FCSTD DOCUMENT  (FreeCAD 1.0R39319 (Git))
Label: MainAssembly
License: All rights reserved
LicenseURL: https://en.wikipedia.org/wiki/All_rights_reserved
objects: App::Link×59, App::FeaturePython×30, Assembly::AssemblyLink×1, App::DocumentObjectGroup×1, Assembly::JointGroup×1, Assembly::AssemblyObject×1
EXTERNAL_REF file=../Parts/Chassis.FCStd obj=Part
EXTERNAL_REF file=../Parts/MotorPlate.FCStd obj=Part
EXTERNAL_REF file=../Parts/MotorHolder.FCStd obj=Part
EXTERNAL_REF file=../Parts/N20Motor.FCStd obj=Part
EXTERNAL_REF file=../Parts/MotorGear.FCStd obj=Part
EXTERNAL_REF file=../Parts/AxleHolder.FCStd obj=Part
EXTERNAL_REF file=../Parts/LegoDifferentialGear.FCStd obj=Part
EXTERNAL_REF file=../Parts/LegoBevelGear.FCStd obj=Part
EXTERNAL_REF file=../Parts/BackWheelAxle.FCStd obj=Part
EXTERNAL_REF file=../Parts/BackWheelStopper.FCStd obj=Part
EXTERNAL_REF file=../Parts/BackWheelConnector.FCStd obj=Part
EXTERNAL_REF file=../Parts/Wheel.FCStd obj=Part
EXTERNAL_REF file=FrontAssembly.FCStd obj=Assembly
EXTERNAL_REF file=FrontAssembly.FCStd obj=FrontCoverPart
EXTERNAL_REF file=FrontAssembly.FCStd obj=WheelLinkageTopLeftBody
EXTERNAL_REF file=FrontAssembly.FCStd obj=WheelLinkageBottomLeftPart
EXTERNAL_REF file=FrontAssembly.FCStd obj=WheelLinkageTopRightPart
EXTERNAL_REF file=FrontAssembly.FCStd obj=WheelLinkageBottomRightPart
EXTERNAL_REF file=FrontAssembly.FCStd obj=FrontWheelAxleLeftPart
EXTERNAL_REF file=FrontAssembly.FCStd obj=FrontWheelAxleRightPart
EXTERNAL_REF file=FrontAssembly.FCStd obj=S0004mPart
EXTERNAL_REF file=FrontAssembly.FCStd obj=TBoneLinkageTopPart
EXTERNAL_REF file=FrontAssembly.FCStd obj=TBoneLinkageBottomPart
EXTERNAL_REF file=FrontAssembly.FCStd obj=TransferLinkageLeftPart
EXTERNAL_REF file=FrontAssembly.FCStd obj=TransferLinkageRightPart
EXTERNAL_REF file=FrontAssembly.FCStd obj=FrontWheelStopperPart
EXTERNAL_REF file=FrontAssembly.FCStd obj=FrontWheelStopperPart001
EXTERNAL_REF file=FrontAssembly.FCStd obj=WheelPart
EXTERNAL_REF file=FrontAssembly.FCStd obj=WheelPart001
EXTERNAL_REF file=FrontAssembly.FCStd obj=RpiCameraPart
EXTERNAL_REF file=../Parts/LidarPlate.FCStd obj=Part
EXTERNAL_REF file=../Parts/Chassis.FCStd obj=Body
EXTERNAL_REF file=../Parts/MotorPlate.FCStd obj=Body
EXTERNAL_REF file=../Parts/MotorHolder.FCStd obj=Body
EXTERNAL_REF file=../Parts/MotorGear.FCStd obj=Body
EXTERNAL_REF file=../Parts/AxleHolder.FCStd obj=Body
EXTERNAL_REF file=../Parts/BackWheelAxle.FCStd obj=Body
EXTERNAL_REF file=../Parts/BackWheelStopper.FCStd obj=Body
EXTERNAL_REF file=../Parts/BackWheelConnector.FCStd obj=Body
EXTERNAL_REF file=../Parts/LidarPlate.FCStd obj=Body
EXTERNAL_REF file=../Parts/FrontCover.FCStd obj=Body
EXTERNAL_REF file=../Parts/WheelLinkage/WheelLinkageBottomLeft.FCStd obj=Body
EXTERNAL_REF file=../Parts/WheelLinkage/WheelLinkageTopRight.FCStd obj=Part__Mirroring
EXTERNAL_REF file=../Parts/WheelLinkage/WheelLinkageBottomRight.FCStd obj=Part__Mirroring
EXTERNAL_REF file=../Parts/FrontWheelAxle/FrontWheelAxleLeft.FCStd obj=Body
EXTERNAL_REF file=../Parts/FrontWheelAxle/FrontWheelAxleRight.FCStd obj=Part__Mirroring
EXTERNAL_REF file=../Parts/TBoneLinkage/TBoneLinkageTop.FCStd obj=Body
EXTERNAL_REF file=../Parts/TBoneLinkage/TBoneLinkageBottom.FCStd obj=Body
EXTERNAL_REF file=../Parts/TransferLinkage/TransferLinkageLeft.FCStd obj=Body
EXTERNAL_REF file=../Parts/TransferLinkage/TransferLinkageRight.FCStd obj=Part__Mirroring
EXTERNAL_REF file=../Parts/FrontWheelStopper.FCStd obj=Body

FEATURE [App::Link] ChassisPart
  LinkedObject = -> <external ../Parts/Chassis.FCStd>#Part
FEATURE [App::FeaturePython] GroundedJoint  # Assembly grounded joint (typed FeaturePython)
  ObjectToGround = -> ChassisPart
FEATURE [App::Link] MotorPlatePart
  LinkPlacement = pos=(-5e-16,-200,64) rot=(0,0,1;0rad)
  LinkedObject = -> <external ../Parts/MotorPlate.FCStd>#Part
  Placement = pos=(-5e-16,-200,64) rot=(0,0,1;0rad)
FEATURE [App::Link] MotorHolderPart
  LinkPlacement = pos=(5,-200,64) rot=(0,0,1;0rad)
  LinkedObject = -> <external ../Parts/MotorHolder.FCStd>#Part
  Placement = pos=(5,-200,64) rot=(0,0,1;0rad)
FEATURE [App::Link] N20MotorPart
  LinkPlacement = pos=(3,-194,44) rot=(0,0,1;0rad)
  LinkedObject = -> <external ../Parts/N20Motor.FCStd>#Part
  Placement = pos=(3,-194,44) rot=(0,0,1;0rad)
FEATURE [App::Link] MotorGearPart
  LinkPlacement = pos=(-12.15,-194.077,44) rot=(0.57735,0.57735,0.57735;2.0944rad)
  LinkedObject = -> <external ../Parts/MotorGear.FCStd>#Part
  Placement = pos=(-12.15,-194.077,44) rot=(0.57735,0.57735,0.57735;2.0944rad)
FEATURE [App::FeaturePython] Joint  label="Fixed"  # Assembly joint (typed FeaturePython)
  Activated = true
  AngleMax = 0
  AngleMin = 0
  Detach1 = false
  Detach2 = false
  Distance = 0
  Distance2 = 0
  EnableAngleMax = false
  EnableAngleMin = false
  EnableLengthMax = false
  EnableLengthMin = false
  JointType = 0 (Fixed)
  LengthMax = 0
  LengthMin = 0
  Placement1 = pos=(19.5,-19,-5) rot=(0,0,1;0rad)
  Placement2 = pos=(19.5,-219,59) rot=(0,0,1;0rad)
  Reference1 = -> Assembly [MotorPlatePart.Body.Edge35,MotorPlatePart.Body.Edge35]
  Reference2 = -> Assembly [ChassisPart.Body.Edge276,ChassisPart.Body.Edge276]
FEATURE [App::FeaturePython] Joint001  label="Fixed001"  # Assembly joint (typed FeaturePython)
  Activated = true
  AngleMax = 0
  AngleMin = 0
  Detach1 = false
  Detach2 = false
  Distance = 0
  Distance2 = 0
  EnableAngleMax = false
  EnableAngleMin = false
  EnableLengthMax = false
  EnableLengthMin = false
  JointType = 0 (Fixed)
  LengthMax = 0
  LengthMin = 0
  Offset2 = pos=(0,0,0) rot=(0,0,1;1.5708rad)
  Placement1 = pos=(5,-6,-15) rot=(0,0,-1;1.5708rad)
  Placement2 = pos=(10,-6,-15) rot=(0.707107,-0.707107,0;3.14159rad)
  Reference1 = -> Assembly [MotorHolderPart.Body.Edge5,MotorHolderPart.Body.Edge5]
  Reference2 = -> Assembly [MotorPlatePart.Body.Edge43,MotorPlatePart.Body.Edge43]
FEATURE [App::FeaturePython] Joint002  label="Distance"  # Assembly joint (typed FeaturePython)
  Activated = true
  AngleMax = 0
  AngleMin = 0
  Detach1 = false
  Detach2 = false
  Distance = 0
  Distance2 = 0
  EnableAngleMax = false
  EnableAngleMin = false
  EnableLengthMax = false
  EnableLengthMin = false
  JointType = 5 (Distance)
  LengthMax = 0
  LengthMin = 0
  Placement1 = pos=(-7.38622,1.78864e-06,5) rot=(0,0,-1;3.14159rad)
  Placement2 = pos=(10,6,-15) rot=(0,0,1;0rad)
  Reference1 = -> Assembly [N20MotorPart.Compound.Face176,N20MotorPart.Compound.Vertex330]
  Reference2 = -> Assembly [MotorPlatePart.Body.Face8,MotorPlatePart.Body.Face8]
FEATURE [App::FeaturePython] Joint003  label="Distance001"  # Assembly joint (typed FeaturePython)
  Activated = true
  AngleMax = 0
  AngleMin = 0
  Detach1 = false
  Detach2 = false
  Distance = 0
  Distance2 = 0
  EnableAngleMax = false
  EnableAngleMin = false
  EnableLengthMax = false
  EnableLengthMin = false
  JointType = 5 (Distance)
  LengthMax = 0
  LengthMin = 0
  Placement1 = pos=(5,12,-20) rot=(0.57735,-0.57735,0.57735;2.0944rad)
  Placement2 = pos=(-7.4,2.6e-15,-1.9e-15) rot=(0.57735,-0.57735,-0.57735;2.0944rad)
  Reference1 = -> Assembly [MotorHolderPart.Body.Face9,MotorHolderPart.Body.Face9]
  Reference2 = -> Assembly [N20MotorPart.Compound.Face175,N20MotorPart.Compound.Face175]
FEATURE [App::FeaturePython] Joint004  label="Fixed002"  # Assembly joint (typed FeaturePython)
  Activated = true
  AngleMax = 0
  AngleMin = 0
  Detach1 = false
  Detach2 = false
  Distance = 0
  Distance2 = 0
  EnableAngleMax = false
  EnableAngleMin = false
  EnableLengthMax = false
  EnableLengthMin = false
  JointType = 0 (Fixed)
  LengthMax = 0
  LengthMin = 0
  Offset2 = pos=(0,0,-7.7) rot=(0,0,1;0rad)
  Placement1 = pos=(0,0,3.85) rot=(1,0,0;3.14159rad)
  Placement2 = pos=(11.3,0.0768482,2.70398e-05) rot=(-0.57735,0.57735,-0.57735;2.0944rad)
  Reference1 = -> Assembly [MotorGearPart.Body.Edge5,MotorGearPart.Body.Edge5]
  Reference2 = -> Assembly [N20MotorPart.Compound.Face1277,N20MotorPart.Compound.Face1277]
FEATURE [App::Link] AxleHolderPart
  LinkPlacement = pos=(-23,-194,44) rot=(0.57735,0.57735,0.57735;2.0944rad)
  LinkedObject = -> <external ../Parts/AxleHolder.FCStd>#Part
  Placement = pos=(-23,-194,44) rot=(0.57735,0.57735,0.57735;2.0944rad)
FEATURE [App::Link] AxleHolderPart001
  LinkPlacement = pos=(-23,-194,20) rot=(0.57735,0.57735,0.57735;2.0944rad)
  LinkedObject = -> <external ../Parts/AxleHolder.FCStd>#Part
  Placement = pos=(-23,-194,20) rot=(0.57735,0.57735,0.57735;2.0944rad)
FEATURE [App::Link] AxleHolderPart002
  LinkPlacement = pos=(23,-194,20) rot=(-0.57735,0.57735,0.57735;4.18879rad)
  LinkedObject = -> <external ../Parts/AxleHolder.FCStd>#Part
  Placement = pos=(23,-194,20) rot=(-0.57735,0.57735,0.57735;4.18879rad)
FEATURE [App::FeaturePython] Joint006  label="Distance003"  # Assembly joint (typed FeaturePython)
  Activated = true
  AngleMax = 0
  AngleMin = 0
  Detach1 = false
  Detach2 = false
  Distance = 0.2
  Distance2 = 0
  EnableAngleMax = false
  EnableAngleMin = false
  EnableLengthMax = false
  EnableLengthMin = false
  JointType = 5 (Distance)
  LengthMax = 0
  LengthMin = 0
  Placement1 = pos=(-1e-16,-4.3,3.04723) rot=(-0.57735,-0.57735,0.57735;4.18879rad)
  Placement2 = pos=(-19.9444,-194,39.5) rot=(0,0,1;0rad)
  Reference1 = -> Assembly [AxleHolderPart.Body.Face9,AxleHolderPart.Body.Face9]
  Reference2 = -> Assembly [ChassisPart.Body.Face80,ChassisPart.Body.Vertex222]
FEATURE [App::FeaturePython] Joint007  label="Distance004"  # Assembly joint (typed FeaturePython)
  Activated = true
  AngleMax = 0
  AngleMin = 0
  Detach1 = false
  Detach2 = false
  Distance = -0.2
  Distance2 = 0
  EnableAngleMax = false
  EnableAngleMin = false
  EnableLengthMax = false
  EnableLengthMin = false
  JointType = 5 (Distance)
  LengthMax = 0
  LengthMin = 0
  Placement1 = pos=(-7.3,-1e-16,1.3) rot=(0.57735,-0.57735,0.57735;4.18879rad)
  Placement2 = pos=(-21.5,-201.5,44) rot=(-0.57735,0.57735,0.57735;2.0944rad)
  Reference1 = -> Assembly [AxleHolderPart.Body.Face3,AxleHolderPart.Body.Vertex8]
  Reference2 = -> Assembly [ChassisPart.Body.Face82,ChassisPart.Body.Vertex107]
FEATURE [App::FeaturePython] Joint008  label="Distance005"  # Assembly joint (typed FeaturePython)
  Activated = true
  AngleMax = 0
  AngleMin = 0
  Detach1 = false
  Detach2 = false
  Distance = 0
  Distance2 = 0
  EnableAngleMax = false
  EnableAngleMin = false
  EnableLengthMax = false
  EnableLengthMin = false
  JointType = 5 (Distance)
  LengthMax = 0
  LengthMin = 0
  Placement1 = pos=(-1e-16,0,0) rot=(0,0,1;0rad)
  Placement2 = pos=(-23,-201.464,33.8054) rot=(-0.707107,0,0.707107;3.14159rad)
  Reference1 = -> Assembly [AxleHolderPart.Body.Face2,AxleHolderPart.Body.Vertex6]
  Reference2 = -> Assembly [ChassisPart.Body.Face21,ChassisPart.Body.Vertex107]
FEATURE [App::FeaturePython] Joint009  label="Distance006"  # Assembly joint (typed FeaturePython)
  Activated = true
  AngleMax = 0
  AngleMin = 0
  Detach1 = false
  Detach2 = false
  Distance = 0.2
  Distance2 = 0
  EnableAngleMax = false
  EnableAngleMin = false
  EnableLengthMax = false
  EnableLengthMin = false
  JointType = 5 (Distance)
  LengthMax = 0
  LengthMin = 0
  Placement1 = pos=(-1e-16,-4.3,3.04723) rot=(-0.57735,-0.57735,0.57735;4.18879rad)
  Placement2 = pos=(-19.9444,-194,15.5) rot=(0,0,1;0rad)
  Reference1 = -> Assembly [AxleHolderPart001.Body.Face9,AxleHolderPart001.Body.Face9]
  Reference2 = -> Assembly [ChassisPart.Body.Face83,ChassisPart.Body.Face83]
FEATURE [App::FeaturePython] Joint010  label="Distance007"  # Assembly joint (typed FeaturePython)
  Activated = true
  AngleMax = 0
  AngleMin = 0
  Detach1 = false
  Detach2 = false
  Distance = -0.2
  Distance2 = 0
  EnableAngleMax = false
  EnableAngleMin = false
  EnableLengthMax = false
  EnableLengthMin = false
  JointType = 5 (Distance)
  LengthMax = 0
  LengthMin = 0
  Placement1 = pos=(-7.3,-1e-16,1.3) rot=(0.57735,-0.57735,0.57735;4.18879rad)
  Placement2 = pos=(-21.5,-201.5,20) rot=(0.57735,-0.57735,0.57735;2.0944rad)
  Reference1 = -> Assembly [AxleHolderPart001.Body.Face3,AxleHolderPart001.Body.Vertex6]
  Reference2 = -> Assembly [ChassisPart.Body.Face85,ChassisPart.Body.Face85]
FEATURE [App::FeaturePython] Joint011  label="Distance008"  # Assembly joint (typed FeaturePython)
  Activated = true
  AngleMax = 0
  AngleMin = 0
  Detach1 = false
  Detach2 = false
  Distance = 0
  Distance2 = 0
  EnableAngleMax = false
  EnableAngleMin = false
  EnableLengthMax = false
  EnableLengthMin = false
  JointType = 5 (Distance)
  LengthMax = 0
  LengthMin = 0
  Placement1 = pos=(-1e-16,0,0) rot=(0,0,1;0rad)
  Placement2 = pos=(-23,-201.464,33.8054) rot=(-0.707107,0,0.707107;3.14159rad)
  Reference1 = -> Assembly [AxleHolderPart001.Body.Face2,AxleHolderPart001.Body.Vertex6]
  Reference2 = -> Assembly [ChassisPart.Body.Face21,ChassisPart.Body.Vertex112]
FEATURE [App::FeaturePython] Joint012  label="Distance009"  # Assembly joint (typed FeaturePython)
  Activated = true
  AngleMax = 0
  AngleMin = 0
  Detach1 = false
  Detach2 = false
  Distance = 0.2
  Distance2 = 0
  EnableAngleMax = false
  EnableAngleMin = false
  EnableLengthMax = false
  EnableLengthMin = false
  JointType = 5 (Distance)
  LengthMax = 0
  LengthMin = 0
  Placement1 = pos=(-1e-16,-4.3,3.04723) rot=(-0.57735,-0.57735,0.57735;4.18879rad)
  Placement2 = pos=(19.9444,-194,15.5) rot=(0,0,1;0rad)
  Reference1 = -> Assembly [AxleHolderPart002.Body.Face9,AxleHolderPart002.Body.Face9]
  Reference2 = -> Assembly [ChassisPart.Body.Face99,ChassisPart.Body.Face99]
FEATURE [App::FeaturePython] Joint013  label="Distance010"  # Assembly joint (typed FeaturePython)
  Activated = true
  AngleMax = 0
  AngleMin = 0
  Detach1 = false
  Detach2 = false
  Distance = -0.2
  Distance2 = 0
  EnableAngleMax = false
  EnableAngleMin = false
  EnableLengthMax = false
  EnableLengthMin = false
  JointType = 5 (Distance)
  LengthMax = 0
  LengthMin = 0
  Placement1 = pos=(7.3,1e-16,1.3) rot=(-0.57735,-0.57735,0.57735;2.0944rad)
  Placement2 = pos=(21.5,-201.5,20) rot=(-0.57735,-0.57735,0.57735;4.18879rad)
  Reference1 = -> Assembly [AxleHolderPart002.Body.Face1,AxleHolderPart002.Body.Face1]
  Reference2 = -> Assembly [ChassisPart.Body.Face100,ChassisPart.Body.Face100]
FEATURE [App::FeaturePython] Joint014  label="Distance011"  # Assembly joint (typed FeaturePython)
  Activated = true
  AngleMax = 0
  AngleMin = 0
  Detach1 = false
  Detach2 = false
  Distance = 0
  Distance2 = 0
  EnableAngleMax = false
  EnableAngleMin = false
  EnableLengthMax = false
  EnableLengthMin = false
  JointType = 5 (Distance)
  LengthMax = 0
  LengthMin = 0
  Placement1 = pos=(-1e-16,0,0) rot=(0,0,1;0rad)
  Placement2 = pos=(23,-202.313,31.8764) rot=(0.707107,0,0.707107;3.14159rad)
  Reference1 = -> Assembly [AxleHolderPart002.Body.Face2,AxleHolderPart002.Body.Vertex7]
  Reference2 = -> Assembly [ChassisPart.Body.Face29,ChassisPart.Body.Edge197]
FEATURE [App::Link] LegoDifferentialGearPart
  LinkPlacement = pos=(3.13e-14,-194,20) rot=(0.552363,0.624332,-0.552363;4.25783rad)
  LinkedObject = -> <external ../Parts/LegoDifferentialGear.FCStd>#Part
  Placement = pos=(3.13e-14,-194,20) rot=(0.552363,0.624332,-0.552363;4.25783rad)
FEATURE [App::FeaturePython] Joint015  label="Fixed003"  # Assembly joint (typed FeaturePython)
  Activated = true
  AngleMax = 0
  AngleMin = 0
  Detach1 = false
  Detach2 = false
  Distance = 0
  Distance2 = 0
  EnableAngleMax = false
  EnableAngleMin = false
  EnableLengthMax = false
  EnableLengthMin = false
  JointType = 0 (Fixed)
  LengthMax = 0
  LengthMin = 0
  Offset2 = pos=(0,0,0) rot=(0,0,1;1.69297rad)
  Placement1 = pos=(0,-3.7e-15,16) rot=(0,0,-1;1.5708rad)
  Placement2 = pos=(0,0,7) rot=(0,0,1;1.69297rad)
  Reference1 = -> Assembly [LegoDifferentialGearPart.Solid.Edge333,LegoDifferentialGearPart.Solid.Edge333]
  Reference2 = -> Assembly [AxleHolderPart001.Body.Edge26,AxleHolderPart001.Body.Edge26]
FEATURE [App::Link] LegoBevelGearPart
  LinkPlacement = pos=(5.02e-14,-193.147,13.0522) rot=(0.599465,0.530362,0.599465;2.16631rad)
  LinkedObject = -> <external ../Parts/LegoBevelGear.FCStd>#Part
  Placement = pos=(5.02e-14,-193.147,13.0522) rot=(0.599465,0.530362,0.599465;2.16631rad)
FEATURE [App::Link] LegoBevelGearPart001
  LinkPlacement = pos=(-7.05,-194,20) rot=(0.187428,0.187428,-0.964231;1.60721rad)
  LinkedObject = -> <external ../Parts/LegoBevelGear.FCStd>#Part
  Placement = pos=(-7.05,-194,20) rot=(0.187428,0.187428,-0.964231;1.60721rad)
FEATURE [App::Link] LegoBevelGearPart002
  LinkPlacement = pos=(7.05,-194,20) rot=(0.187428,-0.187428,0.964231;1.60721rad)
  LinkedObject = -> <external ../Parts/LegoBevelGear.FCStd>#Part
  Placement = pos=(7.05,-194,20) rot=(0.187428,-0.187428,0.964231;1.60721rad)
FEATURE [App::FeaturePython] Joint016  label="Fixed004"  # Assembly joint (typed FeaturePython)
  Activated = true
  AngleMax = 0
  AngleMin = 0
  Detach1 = false
  Detach2 = false
  Distance = 0
  Distance2 = 0
  EnableAngleMax = false
  EnableAngleMin = false
  EnableLengthMax = false
  EnableLengthMin = false
  JointType = 0 (Fixed)
  LengthMax = 0
  LengthMin = 0
  Placement1 = pos=(4e-16,-1.2,0) rot=(-0.57735,-0.57735,-0.57735;2.0944rad)
  Placement2 = pos=(0,8.2,0) rot=(0.57735,0.57735,-0.57735;2.0944rad)
  Reference1 = -> Assembly [LegoBevelGearPart.Part__Feature.Edge4,LegoBevelGearPart.Part__Feature.Edge4]
  Reference2 = -> Assembly [LegoDifferentialGearPart.Solid.Edge734,LegoDifferentialGearPart.Solid.Edge734]
FEATURE [App::FeaturePython] Joint017  label="Fixed005"  # Assembly joint (typed FeaturePython)
  Activated = true
  AngleMax = 0
  AngleMin = 0
  Detach1 = false
  Detach2 = false
  Distance = 0
  Distance2 = 0
  EnableAngleMax = false
  EnableAngleMin = false
  EnableLengthMax = false
  EnableLengthMin = false
  JointType = 0 (Fixed)
  LengthMax = 0
  LengthMin = 0
  Offset2 = pos=(0,0,0) rot=(0,0,-1;0.261799rad)
  Placement1 = pos=(4e-16,-1.2,0) rot=(-0.57735,-0.57735,-0.57735;2.0944rad)
  Placement2 = pos=(0,-1.4e-15,8.25) rot=(0,0,-1;1.8326rad)
  Reference1 = -> Assembly [LegoBevelGearPart001.Part__Feature.Edge4,LegoBevelGearPart001.Part__Feature.Edge4]
  Reference2 = -> Assembly [LegoDifferentialGearPart.Solid.Edge334,LegoDifferentialGearPart.Solid.Edge334]
FEATURE [App::FeaturePython] Joint018  label="Fixed006"  # Assembly joint (typed FeaturePython)
  Activated = true
  AngleMax = 0
  AngleMin = 0
  Detach1 = false
  Detach2 = false
  Distance = 0
  Distance2 = 0
  EnableAngleMax = false
  EnableAngleMin = false
  EnableLengthMax = false
  EnableLengthMin = false
  JointType = 0 (Fixed)
  LengthMax = 0
  LengthMin = 0
  Offset1 = pos=(0,0,0) rot=(1,0,0;3.14159rad)
  Offset2 = pos=(0,0,0) rot=(0,0,-1;0.261799rad)
  Placement1 = pos=(4e-16,-1.2,0) rot=(0.57735,-0.57735,0.57735;2.0944rad)
  Placement2 = pos=(0,3.6e-15,-8.25) rot=(0,0,-1;1.8326rad)
  Reference1 = -> Assembly [LegoBevelGearPart002.Part__Feature.Edge4,LegoBevelGearPart002.Part__Feature.Edge4]
  Reference2 = -> Assembly [LegoDifferentialGearPart.Solid.Edge343,LegoDifferentialGearPart.Solid.Edge343]
FEATURE [App::Link] BackWheelAxlePart
  LinkPlacement = pos=(-3.1,-194,20) rot=(0.519988,0.677661,-0.519988;4.33274rad)
  LinkedObject = -> <external ../Parts/BackWheelAxle.FCStd>#Part
  Placement = pos=(-3.1,-194,20) rot=(0.519988,0.677661,-0.519988;4.33274rad)
FEATURE [App::Link] BackWheelAxlePart001
  LinkPlacement = pos=(3.1,-194,20) rot=(-0.519988,0.677661,-0.519988;1.95044rad)
  LinkedObject = -> <external ../Parts/BackWheelAxle.FCStd>#Part
  Placement = pos=(3.1,-194,20) rot=(-0.519988,0.677661,-0.519988;1.95044rad)
FEATURE [App::FeaturePython] Joint019  label="Fixed007"  # Assembly joint (typed FeaturePython)
  Activated = true
  AngleMax = 0
  AngleMin = 0
  Detach1 = false
  Detach2 = false
  Distance = 0
  Distance2 = 0
  EnableAngleMax = false
  EnableAngleMin = false
  EnableLengthMax = false
  EnableLengthMin = false
  JointType = 0 (Fixed)
  LengthMax = 0
  LengthMin = 0
  Offset2 = pos=(0,0,0) rot=(0,0,1;0.261799rad)
  Placement1 = pos=(0,0,19.9) rot=(0,0,1;0rad)
  Placement2 = pos=(0,0,0) rot=(0,0,1;0.261799rad)
  Reference1 = -> Assembly [BackWheelAxlePart.Body.Edge26,BackWheelAxlePart.Body.Edge26]
  Reference2 = -> Assembly [AxleHolderPart001.Body.Edge8,AxleHolderPart001.Body.Edge8]
FEATURE [App::FeaturePython] Joint020  label="Fixed008"  # Assembly joint (typed FeaturePython)
  Activated = true
  AngleMax = 0
  AngleMin = 0
  Detach1 = false
  Detach2 = false
  Distance = 0
  Distance2 = 0
  EnableAngleMax = false
  EnableAngleMin = false
  EnableLengthMax = false
  EnableLengthMin = false
  JointType = 0 (Fixed)
  LengthMax = 0
  LengthMin = 0
  Offset2 = pos=(0,0,0) rot=(0,0,-1;0.261799rad)
  Placement1 = pos=(0,0,19.9) rot=(0,0,1;0rad)
  Placement2 = pos=(0,0,0) rot=(0,0,-1;0.261799rad)
  Reference1 = -> Assembly [BackWheelAxlePart001.Body.Edge26,BackWheelAxlePart001.Body.Edge26]
  Reference2 = -> Assembly [AxleHolderPart002.Body.Edge8,AxleHolderPart002.Body.Edge8]
FEATURE [App::Link] BackWheelStopperPart
  LinkPlacement = pos=(-26.6,-194,20) rot=(0.57735,-0.57735,0.57735;4.18879rad)
  LinkedObject = -> <external ../Parts/BackWheelStopper.FCStd>#Part
  Placement = pos=(-26.6,-194,20) rot=(0.57735,-0.57735,0.57735;4.18879rad)
FEATURE [App::Link] BackWheelStopperPart001
  LinkPlacement = pos=(26.6,-194,20) rot=(0.57735,0.57735,-0.57735;4.18879rad)
  LinkedObject = -> <external ../Parts/BackWheelStopper.FCStd>#Part
  Placement = pos=(26.6,-194,20) rot=(0.57735,0.57735,-0.57735;4.18879rad)
FEATURE [App::FeaturePython] Joint021  label="Fixed009"  # Assembly joint (typed FeaturePython)
  Activated = true
  AngleMax = 0
  AngleMin = 0
  Detach1 = false
  Detach2 = false
  Distance = 0
  Distance2 = 0
  EnableAngleMax = false
  EnableAngleMin = false
  EnableLengthMax = false
  EnableLengthMin = false
  JointType = 0 (Fixed)
  LengthMax = 0
  LengthMin = 0
  Placement1 = pos=(11,0,3.6) rot=(0,0,1;0rad)
  Placement2 = pos=(-23,-205,20) rot=(-0.57735,0.57735,0.57735;4.18879rad)
  Reference1 = -> Assembly [BackWheelStopperPart.Body.Edge35,BackWheelStopperPart.Body.Edge35]
  Reference2 = -> Assembly [ChassisPart.Body.Edge133,ChassisPart.Body.Edge133]
FEATURE [App::FeaturePython] Joint022  label="Fixed010"  # Assembly joint (typed FeaturePython)
  Activated = true
  AngleMax = 0
  AngleMin = 0
  Detach1 = false
  Detach2 = false
  Distance = 0
  Distance2 = 0
  EnableAngleMax = false
  EnableAngleMin = false
  EnableLengthMax = false
  EnableLengthMin = false
  JointType = 0 (Fixed)
  LengthMax = 0
  LengthMin = 0
  Placement1 = pos=(-11,0,3.6) rot=(0,0,1;0rad)
  Placement2 = pos=(23,-205,20) rot=(0.57735,0.57735,0.57735;2.0944rad)
  Reference1 = -> Assembly [BackWheelStopperPart001.Body.Edge37,BackWheelStopperPart001.Body.Edge37]
  Reference2 = -> Assembly [ChassisPart.Body.Edge161,ChassisPart.Body.Edge161]
FEATURE [App::Link] BackWheelConnectorPart
  LinkPlacement = pos=(-43,-194,20) rot=(0.621515,-0.476905,-0.621515;2.25159rad)
  LinkedObject = -> <external ../Parts/BackWheelConnector.FCStd>#Part
  Placement = pos=(-43,-194,20) rot=(0.621515,-0.476905,-0.621515;2.25159rad)
FEATURE [App::Link] BackWheelConnectorPart001
  LinkPlacement = pos=(43,-194,20) rot=(0.621515,0.476905,0.621515;2.25159rad)
  LinkedObject = -> <external ../Parts/BackWheelConnector.FCStd>#Part
  Placement = pos=(43,-194,20) rot=(0.621515,0.476905,0.621515;2.25159rad)
FEATURE [App::FeaturePython] Joint023  label="Fixed011"  # Assembly joint (typed FeaturePython)
  Activated = true
  AngleMax = 0
  AngleMin = 0
  Detach1 = false
  Detach2 = false
  Distance = 0
  Distance2 = 0
  EnableAngleMax = false
  EnableAngleMin = false
  EnableLengthMax = false
  EnableLengthMin = false
  JointType = 0 (Fixed)
  LengthMax = 0
  LengthMin = 0
  Offset2 = pos=(0,0,0.4) rot=(0,0,1;0rad)
  Placement1 = pos=(2.5,1.9,-3.5) rot=(0,0.707107,0.707107;3.14159rad)
  Placement2 = pos=(-2.5,-1.9,36.4) rot=(1,0,0;1.5708rad)
  Reference1 = -> Assembly [BackWheelConnectorPart.Body.Edge66,BackWheelConnectorPart.Body.Edge66]
  Reference2 = -> Assembly [BackWheelAxlePart.Body.Edge9,BackWheelAxlePart.Body.Edge9]
FEATURE [App::FeaturePython] Joint024  label="Fixed012"  # Assembly joint (typed FeaturePython)
  Activated = true
  AngleMax = 0
  AngleMin = 0
  Detach1 = false
  Detach2 = false
  Distance = 0
  Distance2 = 0
  EnableAngleMax = false
  EnableAngleMin = false
  EnableLengthMax = false
  EnableLengthMin = false
  JointType = 0 (Fixed)
  LengthMax = 0
  LengthMin = 0
  Offset2 = pos=(0,0,0.4) rot=(0,0,1;0rad)
  Placement1 = pos=(-2.5,1.9,-3.5) rot=(0,0.707107,0.707107;3.14159rad)
  Placement2 = pos=(2.5,-1.9,36.4) rot=(1,0,0;1.5708rad)
  Reference1 = -> Assembly [BackWheelConnectorPart001.Body.Edge67,BackWheelConnectorPart001.Body.Edge67]
  Reference2 = -> Assembly [BackWheelAxlePart001.Body.Edge10,BackWheelAxlePart001.Body.Edge10]
FEATURE [App::Link] WheelPart
  LinkPlacement = pos=(-35,-194,20) rot=(1,0,0;0.261799rad)
  LinkedObject = -> <external ../Parts/Wheel.FCStd>#Part
  Placement = pos=(-35,-194,20) rot=(1,0,0;0.261799rad)
FEATURE [App::Link] WheelPart001
  LinkPlacement = pos=(35,-194,20) rot=(0,-0.130526,0.991445;3.14159rad)
  LinkedObject = -> <external ../Parts/Wheel.FCStd>#Part
  Placement = pos=(35,-194,20) rot=(0,-0.130526,0.991445;3.14159rad)
FEATURE [App::FeaturePython] Joint025  label="Fixed013"  # Assembly joint (typed FeaturePython)
  Activated = true
  AngleMax = 0
  AngleMin = 0
  Detach1 = false
  Detach2 = false
  Distance = 0
  Distance2 = 0
  EnableAngleMax = false
  EnableAngleMin = false
  EnableLengthMax = false
  EnableLengthMin = false
  JointType = 0 (Fixed)
  LengthMax = 0
  LengthMin = 0
  Offset2 = pos=(0,0,0) rot=(0,0,1;3.14159rad)
  Placement1 = pos=(-11,7.8e-15,-3.9e-15) rot=(0.57735,0.57735,0.57735;2.0944rad)
  Placement2 = pos=(0,0,3) rot=(0,0,1;3.14159rad)
  Reference1 = -> Assembly [WheelPart.Body.Edge25,WheelPart.Body.Edge25]
  Reference2 = -> Assembly [BackWheelConnectorPart.Body.Edge3,BackWheelConnectorPart.Body.Edge3]
FEATURE [App::FeaturePython] Joint026  label="Fixed014"  # Assembly joint (typed FeaturePython)
  Activated = true
  AngleMax = 0
  AngleMin = 0
  Detach1 = false
  Detach2 = false
  Distance = 0
  Distance2 = 0
  EnableAngleMax = false
  EnableAngleMin = false
  EnableLengthMax = false
  EnableLengthMin = false
  JointType = 0 (Fixed)
  LengthMax = 0
  LengthMin = 0
  Offset2 = pos=(0,0,0) rot=(0,0,1;3.14159rad)
  Placement1 = pos=(-11,7.8e-15,-3.9e-15) rot=(0.57735,0.57735,0.57735;2.0944rad)
  Placement2 = pos=(0,0,3) rot=(0,0,1;3.14159rad)
  Reference1 = -> Assembly [WheelPart001.Body.Edge25,WheelPart001.Body.Edge25]
  Reference2 = -> Assembly [BackWheelConnectorPart001.Body.Edge3,BackWheelConnectorPart001.Body.Edge3]
FEATURE [App::Link] FrontCoverPart
  LinkedObject = -> <external FrontAssembly.FCStd>#FrontCoverPart
FEATURE [App::Link] WheelLinkageTopLeftBody
  LinkPlacement = pos=(-34,-2e-16,0) rot=(0,0,1;0.017527rad)
  LinkedObject = -> <external FrontAssembly.FCStd>#WheelLinkageTopLeftBody
  Placement = pos=(-34,-2e-16,0) rot=(0,0,1;0.017527rad)
FEATURE [App::Link] WheelLinkageBottomLeftPart
  LinkPlacement = pos=(-34,-2e-16,-7) rot=(0,0,1;0.017527rad)
  LinkedObject = -> <external FrontAssembly.FCStd>#WheelLinkageBottomLeftPart
  Placement = pos=(-34,-2e-16,-7) rot=(0,0,1;0.017527rad)
FEATURE [App::Link] WheelLinkageTopRightPart
  LinkPlacement = pos=(34,0,0) rot=(0,0,1;0.017627rad)
  LinkedObject = -> <external FrontAssembly.FCStd>#WheelLinkageTopRightPart
  Placement = pos=(34,0,0) rot=(0,0,1;0.017627rad)
FEATURE [App::Link] WheelLinkageBottomRightPart
  LinkPlacement = pos=(34,0,-7) rot=(0,0,1;0.017627rad)
  LinkedObject = -> <external FrontAssembly.FCStd>#WheelLinkageBottomRightPart
  Placement = pos=(34,0,-7) rot=(0,0,1;0.017627rad)
FEATURE [App::Link] FrontWheelAxleLeftPart
  LinkPlacement = pos=(-31.0005,0.0525794,-3.5) rot=(0,0,1;0.017527rad)
  LinkedObject = -> <external FrontAssembly.FCStd>#FrontWheelAxleLeftPart
  Placement = pos=(-31.0005,0.0525794,-3.5) rot=(0,0,1;0.017527rad)
FEATURE [App::Link] FrontWheelAxleRightPart
  LinkPlacement = pos=(31.0005,-0.0528788,-3.5) rot=(0,0,1;0.017627rad)
  LinkedObject = -> <external FrontAssembly.FCStd>#FrontWheelAxleRightPart
  Placement = pos=(31.0005,-0.0528788,-3.5) rot=(0,0,1;0.017627rad)
FEATURE [App::Link] S0004mPart
  LinkPlacement = pos=(0,-9.55,24.5) rot=(1,0,0;3.14159rad)
  LinkedObject = -> <external FrontAssembly.FCStd>#S0004mPart
  Placement = pos=(0,-9.55,24.5) rot=(1,0,0;3.14159rad)
FEATURE [App::Link] TBoneLinkageTopPart
  LinkPlacement = pos=(0,-4,1e-16) rot=(0,0,1;0.016716rad)
  LinkedObject = -> <external FrontAssembly.FCStd>#TBoneLinkageTopPart
  Placement = pos=(0,-4,1e-16) rot=(0,0,1;0.016716rad)
FEATURE [App::Link] TBoneLinkageBottomPart
  LinkPlacement = pos=(2e-16,-4,-7) rot=(0,0,1;0.016716rad)
  LinkedObject = -> <external FrontAssembly.FCStd>#TBoneLinkageBottomPart
  Placement = pos=(2e-16,-4,-7) rot=(0,0,1;0.016716rad)
FEATURE [App::Link] TransferLinkageLeftPart
  LinkPlacement = pos=(-4.79872,-16.0819,-4.5) rot=(0,0,-1;0.136224rad)
  LinkedObject = -> <external FrontAssembly.FCStd>#TransferLinkageLeftPart
  Placement = pos=(-4.79872,-16.0819,-4.5) rot=(0,0,-1;0.136224rad)
FEATURE [App::Link] TransferLinkageRightPart
  LinkPlacement = pos=(5.19989,-15.9147,-4.5) rot=(0,0,1;0.133954rad)
  LinkedObject = -> <external FrontAssembly.FCStd>#TransferLinkageRightPart
  Placement = pos=(5.19989,-15.9147,-4.5) rot=(0,0,1;0.133954rad)
FEATURE [App::Link] FrontWheelStopperPart
  LinkPlacement = pos=(-42.9986,-0.157738,-3.5) rot=(0,0,1;0.017527rad)
  LinkedObject = -> <external FrontAssembly.FCStd>#FrontWheelStopperPart
  Placement = pos=(-42.9986,-0.157738,-3.5) rot=(0,0,1;0.017527rad)
FEATURE [App::Link] FrontWheelStopperPart001
  LinkPlacement = pos=(42.9986,0.158636,-3.5) rot=(0,0,1;3.15922rad)
  LinkedObject = -> <external FrontAssembly.FCStd>#FrontWheelStopperPart001
  Placement = pos=(42.9986,0.158636,-3.5) rot=(0,0,1;3.15922rad)
FEATURE [App::Link] WheelPart002
  LinkPlacement = pos=(-35.9997,-0.035053,-3.5) rot=(0,0,1;0.017527rad)
  LinkedObject = -> <external FrontAssembly.FCStd>#WheelPart
  Placement = pos=(-35.9997,-0.035053,-3.5) rot=(0,0,1;0.017527rad)
FEATURE [App::Link] WheelPart003
  LinkPlacement = pos=(35.9997,0.0352525,-3.5) rot=(0,0,1;3.15922rad)
  LinkedObject = -> <external FrontAssembly.FCStd>#WheelPart001
  Placement = pos=(35.9997,0.0352525,-3.5) rot=(0,0,1;3.15922rad)
FEATURE [App::Link] RpiCameraPart
  LinkPlacement = pos=(-3.5e-15,11.25,15.75) rot=(0,0,1;0rad)
  LinkedObject = -> <external FrontAssembly.FCStd>#RpiCameraPart
  Placement = pos=(-3.5e-15,11.25,15.75) rot=(0,0,1;0rad)
FEATURE [Assembly::AssemblyLink] FrontAssembly
  Group = -> [FrontCoverPart,WheelLinkageTopLeftBody,WheelLinkageBottomLeftPart,WheelLinkageTopRightPart,WheelLinkageBottomRightPart,FrontWheelAxleLeftPart,FrontWheelAxleRightPart,S0004mPart,TBoneLinkageTopPart,TBoneLinkageBottomPart,TransferLinkageLeftPart,TransferLinkageRightPart,FrontWheelStopperPart,FrontWheelStopperPart001,WheelPart002,WheelPart003,RpiCameraPart]
  LinkedObject = -> <external FrontAssembly.FCStd>#Assembly
  Origin = -> Origin001
  Placement = pos=(0,0,23.5) rot=(0,0,1;0rad)
  Rigid = true
FEATURE [App::FeaturePython] Joint027  label="Fixed015"  # Assembly joint (typed FeaturePython)
  Activated = true
  AngleMax = 0
  AngleMin = 0
  Detach1 = false
  Detach2 = false
  Distance = 0
  Distance2 = 0
  EnableAngleMax = false
  EnableAngleMin = false
  EnableLengthMax = false
  EnableLengthMin = false
  JointType = 0 (Fixed)
  LengthMax = 0
  LengthMin = 0
  Placement1 = pos=(-11.3195,16,0) rot=(0,0,1;0rad)
  Placement2 = pos=(-11.3195,16,23.5) rot=(0,0,1;0rad)
  Reference1 = -> Assembly [FrontAssembly.FrontCoverPart.Body.Edge110,FrontAssembly.FrontCoverPart.Body.Edge110]
  Reference2 = -> Assembly [ChassisPart.Body.Edge253,ChassisPart.Body.Edge253]
FEATURE [App::Link] LidarPlatePart
  LinkPlacement = pos=(0,-135,42) rot=(0,0,1;0rad)
  LinkedObject = -> <external ../Parts/LidarPlate.FCStd>#Part
  Placement = pos=(0,-135,42) rot=(0,0,1;0rad)
FEATURE [App::Link] ChassisBody_export  label="Chassis_1x"
  LinkedObject = -> <external ../Parts/Chassis.FCStd>#Body
FEATURE [App::Link] MotorPlateBody_export  label="MotorPlate_1x"
  LinkedObject = -> <external ../Parts/MotorPlate.FCStd>#Body
FEATURE [App::Link] MotorHolderBody_export  label="MotorHolder_1x"
  LinkedObject = -> <external ../Parts/MotorHolder.FCStd>#Body
FEATURE [App::Link] MotorGearBody_export  label="MotorGear_1x"
  LinkedObject = -> <external ../Parts/MotorGear.FCStd>#Body
FEATURE [App::Link] AxleHolderBody_export  label="AxleHolder_3x"
  LinkedObject = -> <external ../Parts/AxleHolder.FCStd>#Body
FEATURE [App::Link] BackWheelAxleBody_export  label="BackWheelAxle_2x"
  LinkedObject = -> <external ../Parts/BackWheelAxle.FCStd>#Body
FEATURE [App::Link] BackWheelStopperBody_export  label="BackWheelStopper_2x"
  LinkedObject = -> <external ../Parts/BackWheelStopper.FCStd>#Body
FEATURE [App::Link] BackWheelConnectorBody_export  label="BackWheelConnector_2x"
  LinkedObject = -> <external ../Parts/BackWheelConnector.FCStd>#Body
FEATURE [App::Link] LidarPlateBody_export  label="LidarPlate_1x"
  LinkedObject = -> <external ../Parts/LidarPlate.FCStd>#Body
FEATURE [App::Link] FrontCoverBody_export  label="FrontCover_1x"
  LinkedObject = -> <external ../Parts/FrontCover.FCStd>#Body
FEATURE [App::Link] WheelLinkageTopLeftBody_export  label="WheelLinkageTopLeft_1x"
  LinkedObject = -> WheelLinkageTopLeftBody
FEATURE [App::Link] WheelLinkageBottomBody_export  label="WheelLinkageBottomLeft_1x"
  LinkedObject = -> <external ../Parts/WheelLinkage/WheelLinkageBottomLeft.FCStd>#Body
FEATURE [App::Link] WheelLinkageTopRightBody_export  label="WheelLinkageTopRight_1x"
  LinkedObject = -> <external ../Parts/WheelLinkage/WheelLinkageTopRight.FCStd>#Part__Mirroring
FEATURE [App::Link] WheelLinkageBottomRightBody_export  label="WheelLinkageBottomRight_1x"
  LinkedObject = -> <external ../Parts/WheelLinkage/WheelLinkageBottomRight.FCStd>#Part__Mirroring
FEATURE [App::Link] FrontWheelAxleLeftBody_export  label="FrontWheelAxleLeft_1x"
  LinkedObject = -> <external ../Parts/FrontWheelAxle/FrontWheelAxleLeft.FCStd>#Body
FEATURE [App::Link] FrontWheelAxleRightBody_export  label="FrontWheelAxleRight_1x"
  LinkedObject = -> <external ../Parts/FrontWheelAxle/FrontWheelAxleRight.FCStd>#Part__Mirroring
FEATURE [App::Link] TBoneLinkageTopBody_export  label="TBoneLinkageTop_1x"
  LinkedObject = -> <external ../Parts/TBoneLinkage/TBoneLinkageTop.FCStd>#Body
FEATURE [App::Link] TBoneLinkageBottomBody_export  label="TBoneLinkageBottom_1x"
  LinkedObject = -> <external ../Parts/TBoneLinkage/TBoneLinkageBottom.FCStd>#Body
FEATURE [App::Link] TransferLinkageLeftBody_export  label="TransferLinkageLeft_1x"
  LinkedObject = -> <external ../Parts/TransferLinkage/TransferLinkageLeft.FCStd>#Body
FEATURE [App::Link] TransferLinkageRightBody_export  label="TransferLinkageRight_1x"
  LinkedObject = -> <external ../Parts/TransferLinkage/TransferLinkageRight.FCStd>#Part__Mirroring
FEATURE [App::Link] FrontWheelStopperBody_export  label="FrontWheelStopper_2x"
  LinkedObject = -> <external ../Parts/FrontWheelStopper.FCStd>#Body
FEATURE [App::DocumentObjectGroup] mesh_input
  ExportSTL = true
  Group = -> [ChassisBody_export,MotorPlateBody_export,MotorHolderBody_export,MotorGearBody_export,AxleHolderBody_export,BackWheelAxleBody_export,BackWheelStopperBody_export,BackWheelConnectorBody_export,LidarPlateBody_export,FrontCoverBody_export,WheelLinkageTopLeftBody_export,WheelLinkageBottomBody_export,WheelLinkageTopRightBody_export,WheelLinkageBottomRightBody_export,FrontWheelAxleLeftBody_export,+6 more]
  MeshAngularDeflection = 0.05
  MeshLinearDeflection = 0.01
FEATURE [App::FeaturePython] Joint029  label="Distance012"  # Assembly joint (typed FeaturePython)
  Activated = true
  AngleMax = 0
  AngleMin = 0
  Detach1 = false
  Detach2 = false
  Distance = 0
  Distance2 = 0
  EnableAngleMax = false
  EnableAngleMin = false
  EnableLengthMax = false
  EnableLengthMin = false
  JointType = 5 (Distance)
  LengthMax = 0
  LengthMin = 0
  Placement1 = pos=(9e-16,-7e-16,-3.85) rot=(0,0,1;0rad)
  Placement2 = pos=(-16,-200.313,30.5508) rot=(0.707107,0,0.707107;3.14159rad)
  Reference1 = -> Assembly [MotorGearPart.Body.Face1455,MotorGearPart.Body.Edge1]
  Reference2 = -> Assembly [ChassisPart.Body.Face75,ChassisPart.Body.Vertex203]
FEATURE [App::FeaturePython] Joint030  label="Fixed016"  # Assembly joint (typed FeaturePython)
  Activated = true
  AngleMax = 0
  AngleMin = 0
  Detach1 = false
  Detach2 = false
  Distance = 0
  Distance2 = 0
  EnableAngleMax = false
  EnableAngleMin = false
  EnableLengthMax = false
  EnableLengthMin = false
  JointType = 0 (Fixed)
  LengthMax = 0
  LengthMin = 0
  Offset2 = pos=(0,0,30) rot=(0,0,1;0rad)
  Placement1 = pos=(40,-22,-4) rot=(1,0,0;3.14159rad)
  Placement2 = pos=(40,-157,38) rot=(0,0,1;0rad)
  Reference1 = -> Assembly [LidarPlatePart.Body.Edge57,LidarPlatePart.Body.Edge57]
  Reference2 = -> Assembly [ChassisPart.Body.Edge47,ChassisPart.Body.Edge47]
FEATURE [Assembly::JointGroup] Joints
  Group = -> [GroundedJoint,Joint,Joint001,Joint002,Joint003,Joint004,Joint006,Joint007,Joint008,Joint009,Joint010,Joint011,Joint012,Joint013,Joint014,Joint015,Joint016,Joint017,Joint018,Joint019,Joint020,Joint021,Joint022,Joint023,Joint024,Joint025,Joint026,Joint027,Joint029,Joint030]
FEATURE [Assembly::AssemblyObject] Assembly  label="MainAssembly"
  Group = -> [Joints,ChassisPart,GroundedJoint,MotorPlatePart,MotorHolderPart,N20MotorPart,MotorGearPart,Joint,Joint001,Joint002,Joint003,Joint004,AxleHolderPart,AxleHolderPart001,AxleHolderPart002,Joint006,Joint007,Joint008,Joint009,Joint010,Joint011,Joint012,Joint013,Joint014,LegoDifferentialGearPart,Joint015,LegoBevelGearPart,LegoBevelGearPart001,LegoBevelGearPart002,Joint016,Joint017,Joint018,+21 more]
  Origin = -> Origin
  Type = Assembly

RESOLVED EXTERNAL PARTS (link-assembly join: the EXTERNAL_REF files above that resolve inside this repo's crawl, each included once):
---- part ../Parts/AxleHolder.FCStd = doc fcstd_25b0f78b8c3b ----
FCSTD DOCUMENT  (FreeCAD 1.0R39109 (Git))
Label: AxleHolder
License: All rights reserved
LicenseURL: https://en.wikipedia.org/wiki/All_rights_reserved
objects: Sketcher::SketchObject×2, PartDesign::Pad×2, PartDesign::Body×1, App::Part×1
note: 11 computed .brp shape members not serialized (recipe doc carries the construction recipe); baked Part::Feature solids carry a one-line shape summary decoded from their .brp

FEATURE [Sketcher::SketchObject] Sketch
  ArcFitTolerance = 1e-06
  AttachmentSupport = -> [XY_Plane001]
  FullyConstrained = true
  MakeInternals = false
  MapMode = 5
  sketch-geometry (6):
    g0: LineSegment StartX=-7.3 StartY=-4.3 StartZ=0 EndX=7.3 EndY=-4.3 EndZ=0
    g1: LineSegment StartX=7.3 StartY=-4.3 StartZ=0 EndX=7.3 EndY=4.3 EndZ=0
    g2: LineSegment StartX=7.3 StartY=4.3 StartZ=0 EndX=-7.3 EndY=4.3 EndZ=0
    g3: LineSegment StartX=-7.3 StartY=4.3 StartZ=0 EndX=-7.3 EndY=-4.3 EndZ=0
    g4: GeomPoint [constr] X=0 Y=0 Z=0
    g5: Circle CenterX=0 CenterY=0 CenterZ=0 NormalX=0 NormalY=0 NormalZ=1 AngleXU=0 Radius=3.2
  constraints (14):
    c: Coincident(g0,g1)
    c: Coincident(g1,g2)
    c: Coincident(g2,g3)
    c: Coincident(g3,g0)
    c: Horizontal(g0)
    c: Horizontal(g2)
    c: Vertical(g1)
    c: Vertical(g3)
    c: Symmetric(g2,g0,g4)
    c: Distance(g1,g3) = 14.6
    c: Distance(g0,g2) = 8.6
    c: Coincident(g4,g-1)
    c: Diameter(g5) = 6.4
    c: Coincident(g5,g4)
FEATURE [PartDesign::Pad] Pad
  Direction = (0,0,1)
  Length = 2.6
  Length2 = 10
  Profile = -> Sketch
  ReferenceAxis = -> Sketch [N_Axis]
  Refine = true
  Suppressed = false
  Type = 0
FEATURE [Sketcher::SketchObject] Sketch001
  ArcFitTolerance = 1e-06
  AttachmentSupport = -> [Pad]
  ExternalGeometry = -> [Sketch]
  FullyConstrained = true
  MakeInternals = false
  MapMode = 5
  Placement = pos=(0,0,2.6) rot=(0,0,1;0rad)
  sketch-geometry (6):
    g0: Circle CenterX=0 CenterY=0 CenterZ=0 NormalX=0 NormalY=0 NormalZ=1 AngleXU=0 Radius=3.2
    g1: LineSegment StartX=-4.3 StartY=-4.3 StartZ=0 EndX=4.3 EndY=-4.3 EndZ=0
    g2: LineSegment StartX=4.3 StartY=-4.3 StartZ=0 EndX=4.3 EndY=4.3 EndZ=0
    g3: LineSegment StartX=4.3 StartY=4.3 StartZ=0 EndX=-4.3 EndY=4.3 EndZ=0
    g4: LineSegment StartX=-4.3 StartY=4.3 StartZ=0 EndX=-4.3 EndY=-4.3 EndZ=0
    g5: GeomPoint [constr] X=0 Y=0 Z=0
  constraints (14):
    c: Coincident(g0,g-1)
    c: Equal(g0,g-3)
    c: Coincident(g1,g2)
    c: Coincident(g2,g3)
    c: Coincident(g3,g4)
    c: Coincident(g4,g1)
    c: Horizontal(g1)
    c: Horizontal(g3)
    c: Vertical(g2)
    c: Vertical(g4)
    c: Symmetric(g3,g1,g5)
    c: Coincident(g5,g0)
    c: PointOnObject(g2,g-4)
    c: Equal(g3,g2)
FEATURE [PartDesign::Pad] Pad001
  BaseFeature = -> Pad
  Direction = (0,0,1)
  Length = 4.4
  Length2 = 10
  Profile = -> Sketch001
  ReferenceAxis = -> Sketch001 [N_Axis]
  Refine = true
  Suppressed = false
  Type = 0
FEATURE [PartDesign::Body] Body  label="AxleHolderBody"
  AllowCompound = false
  Group = -> [Sketch,Pad,Sketch001,Pad001]
  Origin = -> Origin001
  Tip = -> Pad001
FEATURE [App::Part] Part  label="AxleHolderPart"
  Group = -> [Body]
  Origin = -> Origin
---- part ../Parts/BackWheelAxle.FCStd = doc fcstd_1796f26ff270 ----
FCSTD DOCUMENT  (FreeCAD 1.0R39109 (Git))
Label: BackWheelAxle
License: All rights reserved
LicenseURL: https://en.wikipedia.org/wiki/All_rights_reserved
objects: Sketcher::SketchObject×6, PartDesign::Pad×5, PartDesign::Pocket×1, PartDesign::Body×1, App::Part×1
note: 31 computed .brp shape members not serialized (recipe doc carries the construction recipe); baked Part::Feature solids carry a one-line shape summary decoded from their .brp

FEATURE [Sketcher::SketchObject] Sketch
  ArcFitTolerance = 1e-06
  AttachmentSupport = -> [XY_Plane001]
  FullyConstrained = true
  MakeInternals = false
  MapMode = 5
  sketch-geometry (16):
    g0: ArcOfCircle CenterX=-1.3 CenterY=-1.3 CenterZ=0 NormalX=0 NormalY=0 NormalZ=1 AngleXU=0 Radius=0.5 StartAngle=0 EndAngle=1.5708
    g1: ArcOfCircle CenterX=1.3 CenterY=-1.3 CenterZ=0 NormalX=0 NormalY=0 NormalZ=1 AngleXU=0 Radius=0.5 StartAngle=1.5708 EndAngle=3.14159
    g2: ArcOfCircle CenterX=-1.3 CenterY=1.3 CenterZ=0 NormalX=0 NormalY=0 NormalZ=1 AngleXU=0 Radius=0.5 StartAngle=4.71239 EndAngle=6.28319
    g3: ArcOfCircle CenterX=1.3 CenterY=1.3 CenterZ=0 NormalX=0 NormalY=0 NormalZ=1 AngleXU=0 Radius=0.5 StartAngle=3.14159 EndAngle=4.71239
    g4: LineSegment StartX=-0.8 StartY=2.10297 StartZ=0 EndX=-0.8 EndY=1.3 EndZ=0
    g5: LineSegment StartX=-1.3 StartY=0.8 StartZ=0 EndX=-2.10297 EndY=0.8 EndZ=0
    g6: LineSegment StartX=-2.10297 StartY=-0.8 StartZ=0 EndX=-1.3 EndY=-0.8 EndZ=0
    g7: LineSegment StartX=-0.8 StartY=-1.3 StartZ=0 EndX=-0.8 EndY=-2.10297 EndZ=0
    g8: LineSegment StartX=0.8 StartY=-2.10297 StartZ=0 EndX=0.8 EndY=-1.3 EndZ=0
    g9: LineSegment StartX=1.3 StartY=-0.8 StartZ=0 EndX=2.10297 EndY=-0.8 EndZ=0
    g10: LineSegment StartX=2.10297 StartY=0.8 StartZ=0 EndX=1.3 EndY=0.8 EndZ=0
    g11: LineSegment StartX=0.8 StartY=1.3 StartZ=0 EndX=0.8 EndY=2.10297 EndZ=0
    g12: ArcOfCircle CenterX=0 CenterY=0 CenterZ=0 NormalX=0 NormalY=0 NormalZ=1 AngleXU=0 Radius=2.25 StartAngle=1.20729 EndAngle=1.9343
    g13: ArcOfCircle CenterX=0 CenterY=0 CenterZ=0 NormalX=0 NormalY=0 NormalZ=1 AngleXU=0 Radius=2.25 StartAngle=5.91968 EndAngle=6.64669
    g14: ArcOfCircle CenterX=0 CenterY=0 CenterZ=0 NormalX=0 NormalY=0 NormalZ=1 AngleXU=0 Radius=2.25 StartAngle=4.34888 EndAngle=5.0759
    g15: ArcOfCircle CenterX=0 CenterY=0 CenterZ=0 NormalX=0 NormalY=0 NormalZ=1 AngleXU=0 Radius=2.25 StartAngle=2.77808 EndAngle=3.5051
  constraints (44):
    c: Vertical(g4)
    c: Vertical(g11)
    c: Vertical(g7)
    c: Vertical(g8)
    c: Horizontal(g5)
    c: Horizontal(g10)
    c: Horizontal(g9)
    c: Horizontal(g6)
    c: Tangent(g5,g2) = 1.5708
    c: Tangent(g4,g2) = 1.5708
    c: Tangent(g11,g3) = 1.5708
    c: Tangent(g10,g3) = 1.5708
    c: Tangent(g6,g0) = 1.5708
    c: Tangent(g7,g0) = 1.5708
    c: Tangent(g8,g1) = 1.5708
    c: Tangent(g9,g1) = 1.5708
    c: Radius(g2) = 0.5
    c: Equal(g2,g3)
    c: Equal(g2,g1)
    c: Equal(g2,g0)
    c: Coincident(g12,g-1)
    c: Coincident(g12,g4)
    c: Coincident(g12,g11)
    c: Coincident(g13,g12)
    c: Coincident(g13,g10)
    c: Coincident(g13,g9)
    c: Coincident(g14,g12)
    c: Coincident(g14,g8)
    c: Coincident(g14,g7)
    c: Coincident(g15,g12)
    c: Coincident(g15,g6)
    c: Coincident(g15,g5)
    c: Diameter(g12) = 4.5
    c: Equal(g12,g13)
    c: Equal(g12,g14)
    c: Equal(g12,g15)
    c: Equal(g4,g11)
    c: Equal(g4,g8)
    c: Equal(g4,g7)
    c: Equal(g5,g10)
    c: Equal(g5,g6)
    c: Equal(g5,g9)
    c: DistanceY(g6,g5) = 1.6
    c: DistanceX(g4,g11) = 1.6
FEATURE [PartDesign::Pad] Pad
  Direction = (0,0,1)
  Length = 13
  Length2 = 10
  Profile = -> Sketch
  ReferenceAxis = -> Sketch [N_Axis]
  Refine = true
  Suppressed = false
  Type = 0
FEATURE [Sketcher::SketchObject] Sketch001
  ArcFitTolerance = 1e-06
  AttachmentSupport = -> [Pad]
  FullyConstrained = true
  MakeInternals = false
  MapMode = 5
  Placement = pos=(0,0,13) rot=(0,0,1;0rad)
  sketch-geometry (1):
    g0: Circle CenterX=0 CenterY=0 CenterZ=0 NormalX=0 NormalY=0 NormalZ=1 AngleXU=0 Radius=2.9
  constraints (2):
    c: Diameter(g0) = 5.8
    c: Coincident(g0,g-1)
FEATURE [PartDesign::Pad] Pad001
  BaseFeature = -> Pad
  Direction = (0,0,1)
  Length = 6.9
  Length2 = 10
  Profile = -> Sketch001
  ReferenceAxis = -> Sketch001 [N_Axis]
  Refine = true
  Suppressed = false
  Type = 0
FEATURE [Sketcher::SketchObject] Sketch002
  ArcFitTolerance = 1e-06
  AttachmentSupport = -> [Pad001]
  FullyConstrained = true
  MakeInternals = false
  MapMode = 5
  Placement = pos=(0,0,19.9) rot=(0,0,1;0rad)
  sketch-geometry (1):
    g0: Circle CenterX=0 CenterY=0 CenterZ=0 NormalX=0 NormalY=0 NormalZ=1 AngleXU=0 Radius=7
  constraints (2):
    c: Diameter(g0) = 14
    c: Coincident(g0,g-1)
FEATURE [PartDesign::Pad] Pad002
  BaseFeature = -> Pad001
  Direction = (0,0,1)
  Length = 2
  Length2 = 10
  Profile = -> Sketch002
  ReferenceAxis = -> Sketch002 [N_Axis]
  Refine = true
  Suppressed = false
  Type = 0
FEATURE [Sketcher::SketchObject] Sketch003
  ArcFitTolerance = 1e-06
  AttachmentSupport = -> [Pad002]
  FullyConstrained = true
  MakeInternals = false
  MapMode = 5
  Placement = pos=(0,0,21.9) rot=(0,0,1;0rad)
  sketch-geometry (1):
    g0: Circle CenterX=0 CenterY=0 CenterZ=0 NormalX=0 NormalY=0 NormalZ=1 AngleXU=0 Radius=5.5
  constraints (2):
    c: Diameter(g0) = 11
    c: Coincident(g0,g-1)
FEATURE [PartDesign::Pad] Pad003
  BaseFeature = -> Pad002
  Direction = (0,0,1)
  Length = 11
  Length2 = 10
  Profile = -> Sketch003
  ReferenceAxis = -> Sketch003 [N_Axis]
  Refine = true
  Suppressed = false
  Type = 0
FEATURE [Sketcher::SketchObject] Sketch004
  ArcFitTolerance = 1e-06
  AttachmentSupport = -> [Pad003]
  ExternalGeometry = -> [Sketch003]
  FullyConstrained = true
  MakeInternals = false
  MapMode = 5
  Placement = pos=(0,0,32.9) rot=(0,0,1;0rad)
  sketch-geometry (4):
    g0: LineSegment StartX=-5.2915 StartY=-1.5 StartZ=0 EndX=5.2915 EndY=-1.5 EndZ=0
    g1: LineSegment StartX=-5.2915 StartY=1.5 StartZ=0 EndX=5.2915 EndY=1.5 EndZ=0
    g2: ArcOfCircle CenterX=-3e-16 CenterY=-4e-16 CenterZ=0 NormalX=0 NormalY=0 NormalZ=1 AngleXU=0 Radius=5.5 StartAngle=2.86537 EndAngle=3.41782
    g3: ArcOfCircle CenterX=-2.19999e-05 CenterY=8e-16 CenterZ=0 NormalX=0 NormalY=0 NormalZ=1 AngleXU=0 Radius=5.50002 StartAngle=6.00696 EndAngle=6.55941
  constraints (13):
    c: Horizontal(g1)
    c: Horizontal(g0)
    c: Distance(g0,g1) = 3
    c: PointOnObject(g0,g-3)
    c: PointOnObject(g0,g-3)
    c: PointOnObject(g1,g-3)
    c: PointOnObject(g1,g-3)
    c: Coincident(g2,g1)
    c: Coincident(g2,g0)
    c: Symmetric(g1,g0,g2)
    c: Coincident(g3,g0)
    c: Coincident(g3,g1)
    c: Tangent(g3,g-3)
FEATURE [PartDesign::Pad] Pad004
  BaseFeature = -> Pad003
  Direction = (0,0,1)
  Length = 7
  Length2 = 10
  Profile = -> Sketch004
  ReferenceAxis = -> Sketch004 [N_Axis]
  Refine = true
  Suppressed = false
  Type = 0
FEATURE [Sketcher::SketchObject] Sketch005
  ArcFitTolerance = 1e-06
  AttachmentSupport = -> [Pad004]
  ExternalGeometry = -> [Pad004]
  FullyConstrained = true
  MakeInternals = false
  MapMode = 5
  Placement = pos=(0,-1.5,0) rot=(1,0,0;1.5708rad)
  sketch-geometry (2):
    g0: Circle CenterX=2.5 CenterY=36.4 CenterZ=0 NormalX=0 NormalY=0 NormalZ=1 AngleXU=0 Radius=1.5
    g1: Circle CenterX=-2.5 CenterY=36.4 CenterZ=0 NormalX=0 NormalY=0 NormalZ=1 AngleXU=0 Radius=1.5
  constraints (5):
    c: Diameter(g0) = 3
    c: Equal(g0,g1)
    c: Symmetric(g0,g1,g-2)
    c: DistanceX(g1,g0) = 5
    c: Distance(g0,g-3) = 3.5
FEATURE [PartDesign::Pocket] Pocket
  BaseFeature = -> Pad004
  Direction = (0,1,-2e-16)
  Length = 0
  Length2 = 5
  Profile = -> Sketch005
  ReferenceAxis = -> Sketch005 [N_Axis]
  Refine = true
  Suppressed = false
  Type = 3
  UpToFace = -> Pad004 [Face4]
FEATURE [PartDesign::Body] Body  label="BackWheelAxleBody"
  AllowCompound = false
  Group = -> [Sketch,Pad,Sketch001,Pad001,Sketch002,Pad002,Sketch003,Pad003,Sketch004,Pad004,Sketch005,Pocket]
  Origin = -> Origin001
  Tip = -> Pocket
FEATURE [App::Part] Part  label="BackWheelAxlePart"
  Group = -> [Body]
  Origin = -> Origin
---- part ../Parts/BackWheelConnector.FCStd = doc fcstd_118d4a09c716 ----
FCSTD DOCUMENT  (FreeCAD 1.0R39109 (Git))
Label: BackWheelConnector
License: All rights reserved
LicenseURL: https://en.wikipedia.org/wiki/All_rights_reserved
objects: Sketcher::SketchObject×5, PartDesign::Pad×4, PartDesign::Pocket×1, PartDesign::Chamfer×1, PartDesign::Body×1, App::Part×1
note: 29 computed .brp shape members not serialized (recipe doc carries the construction recipe); baked Part::Feature solids carry a one-line shape summary decoded from their .brp

FEATURE [Sketcher::SketchObject] Sketch
  ArcFitTolerance = 1e-06
  AttachmentSupport = -> [XY_Plane001]
  FullyConstrained = true
  MakeInternals = false
  MapMode = 5
  sketch-geometry (13):
    g0: LineSegment [constr] StartX=0 StartY=10 StartZ=0 EndX=-8.66025 EndY=-5 EndZ=0
    g1: LineSegment [constr] StartX=-8.66025 StartY=-5 StartZ=0 EndX=8.66025 EndY=-5 EndZ=0
    g2: LineSegment [constr] StartX=8.66025 StartY=-5 StartZ=0 EndX=0 EndY=10 EndZ=0
    g3: Circle [constr] CenterX=0 CenterY=0 CenterZ=0 NormalX=0 NormalY=0 NormalZ=1 AngleXU=0 Radius=10
    g4: Circle CenterX=0 CenterY=10 CenterZ=0 NormalX=0 NormalY=0 NormalZ=1 AngleXU=0 Radius=1.45
    g5: Circle CenterX=8.66025 CenterY=-5 CenterZ=0 NormalX=0 NormalY=0 NormalZ=1 AngleXU=0 Radius=1.45
    g6: Circle CenterX=-8.66025 CenterY=-5 CenterZ=0 NormalX=0 NormalY=0 NormalZ=1 AngleXU=0 Radius=1.45
    g7: ArcOfCircle CenterX=0 CenterY=10 CenterZ=0 NormalX=0 NormalY=0 NormalZ=1 AngleXU=0 Radius=3.5 StartAngle=0.523599 EndAngle=2.61799
    g8: ArcOfCircle CenterX=8.66025 CenterY=-5 CenterZ=0 NormalX=0 NormalY=0 NormalZ=1 AngleXU=0 Radius=3.5 StartAngle=4.71239 EndAngle=6.80678
    g9: ArcOfCircle CenterX=-8.66025 CenterY=-5 CenterZ=0 NormalX=0 NormalY=0 NormalZ=1 AngleXU=0 Radius=3.5 StartAngle=2.61799 EndAngle=4.71239
    g10: LineSegment StartX=3.03109 StartY=11.75 StartZ=0 EndX=11.6913 EndY=-3.25 EndZ=0
    g11: LineSegment StartX=8.66025 StartY=-8.5 StartZ=0 EndX=-8.66025 EndY=-8.5 EndZ=0
    g12: LineSegment StartX=-11.6913 StartY=-3.25 StartZ=0 EndX=-3.03109 EndY=11.75 EndZ=0
  constraints (29):
    c: Coincident(g0,g1)
    c: Coincident(g1,g2)
    c: Coincident(g2,g0)
    c: Equal(g0,g1)
    c: Equal(g0,g2)
    c: PointOnObject(g0,g3)
    c: PointOnObject(g1,g3)
    c: PointOnObject(g2,g3)
    c: Radius(g3) = 10
    c: Coincident(g3,g-1)
    c: PointOnObject(g2,g-2)
    c: Diameter(g4) = 2.9
    c: Coincident(g4,g0)
    c: Coincident(g5,g1)
    c: Coincident(g6,g0)
    c: Equal(g4,g5)
    c: Equal(g5,g6)
    c: Coincident(g7,g0)
    c: Coincident(g8,g1)
    c: Coincident(g9,g0)
    c: Tangent(g10,g7) = 1.5708
    c: Tangent(g10,g8) = 1.5708
    c: Tangent(g11,g9) = 1.5708
    c: Tangent(g11,g8) = 1.5708
    c: Tangent(g12,g9) = 1.5708
    c: Tangent(g12,g7) = 1.5708
    c: Equal(g7,g8)
    c: Equal(g8,g9)
    c: Radius(g7) = 3.5
FEATURE [PartDesign::Pad] Pad
  Direction = (0,0,1)
  Length = 3
  Length2 = 10
  Profile = -> Sketch
  ReferenceAxis = -> Sketch [N_Axis]
  Refine = true
  Suppressed = false
  Type = 0
FEATURE [Sketcher::SketchObject] Sketch001
  ArcFitTolerance = 1e-06
  AttachmentSupport = -> [Pad]
  FullyConstrained = true
  MakeInternals = false
  MapMode = 5
  Placement = pos=(0,0,0) rot=(1,0,0;3.14159rad)
  sketch-geometry (10):
    g0: LineSegment StartX=-5.5 StartY=1.9 StartZ=0 EndX=5.5 EndY=1.9 EndZ=0
    g1: LineSegment StartX=5.5 StartY=1.9 StartZ=0 EndX=5.5 EndY=4.9 EndZ=0
    g2: LineSegment StartX=5.5 StartY=4.9 StartZ=0 EndX=-5.5 EndY=4.9 EndZ=0
    g3: LineSegment StartX=-5.5 StartY=4.9 StartZ=0 EndX=-5.5 EndY=1.9 EndZ=0
    g4: GeomPoint [constr] X=0 Y=3.4 Z=0
    g5: LineSegment StartX=-5.5 StartY=-4.9 StartZ=0 EndX=5.5 EndY=-4.9 EndZ=0
    g6: LineSegment StartX=5.5 StartY=-4.9 StartZ=0 EndX=5.5 EndY=-1.9 EndZ=0
    g7: LineSegment StartX=5.5 StartY=-1.9 StartZ=0 EndX=-5.5 EndY=-1.9 EndZ=0
    g8: LineSegment StartX=-5.5 StartY=-1.9 StartZ=0 EndX=-5.5 EndY=-4.9 EndZ=0
    g9: GeomPoint [constr] X=0 Y=-3.4 Z=0
  constraints (25):
    c: Coincident(g0,g1)
    c: Coincident(g1,g2)
    c: Coincident(g2,g3)
    c: Coincident(g3,g0)
    c: Horizontal(g0)
    c: Horizontal(g2)
    c: Vertical(g1)
    c: Vertical(g3)
    c: Symmetric(g2,g0,g4)
    c: Distance(g1,g3) = 11
    c: Distance(g0,g2) = 3
    c: PointOnObject(g4,g-2)
    c: Coincident(g5,g6)
    c: Coincident(g6,g7)
    c: Coincident(g7,g8)
    c: Coincident(g8,g5)
    c: Horizontal(g5)
    c: Horizontal(g7)
    c: Vertical(g6)
    c: Vertical(g8)
    c: Symmetric(g7,g5,g9)
    c: PointOnObject(g9,g-2)
    c: Equal(g3,g8)
    c: Symmetric(g7,g0,g-1)
    c: Distance(g7,g0) = 3.8
FEATURE [PartDesign::Pad] Pad001
  BaseFeature = -> Pad
  Direction = (0,0,-1)
  Length = 7
  Length2 = 10
  Profile = -> Sketch001
  ReferenceAxis = -> Sketch001 [N_Axis]
  Refine = true
  Suppressed = false
  Type = 0
FEATURE [Sketcher::SketchObject] Sketch002
  ArcFitTolerance = 1e-06
  AttachmentSupport = -> [Pad001]
  ExternalGeometry = -> [Pad001]
  FullyConstrained = true
  MakeInternals = false
  MapMode = 5
  Placement = pos=(0,4.9,0) rot=(0,0.707107,0.707107;3.14159rad)
  sketch-geometry (2):
    g0: Circle CenterX=-2.5 CenterY=-3.5 CenterZ=0 NormalX=0 NormalY=0 NormalZ=1 AngleXU=0 Radius=1.5
    g1: Circle CenterX=2.5 CenterY=-3.5 CenterZ=0 NormalX=0 NormalY=0 NormalZ=1 AngleXU=0 Radius=1.5
  constraints (5):
    c: Diameter(g0) = 3
    c: Equal(g0,g1)
    c: Symmetric(g0,g1,g-2)
    c: Distance(g0,g-3) = 3.5
    c: DistanceX(g0,g1) = 5
FEATURE [PartDesign::Pocket] Pocket
  BaseFeature = -> Pad001
  Direction = (0,-1,2e-16)
  Length = 0
  Length2 = 5
  Profile = -> Sketch002
  ReferenceAxis = -> Sketch002 [N_Axis]
  Refine = true
  Suppressed = false
  Type = 3
  UpToFace = -> Pad001 [Face11]
FEATURE [Sketcher::SketchObject] Sketch003
  ArcFitTolerance = 1e-06
  AttachmentSupport = -> [Pocket]
  ExternalGeometry = -> [Sketch]
  FullyConstrained = true
  MakeInternals = false
  MapMode = 5
  Placement = pos=(0,0,3) rot=(0,0,1;0rad)
  sketch-geometry (6):
    g0: Circle CenterX=0 CenterY=10 CenterZ=0 NormalX=0 NormalY=0 NormalZ=1 AngleXU=0 Radius=1.45
    g1: Circle CenterX=8.66025 CenterY=-5 CenterZ=0 NormalX=0 NormalY=0 NormalZ=1 AngleXU=0 Radius=1.45
    g2: Circle CenterX=-8.66025 CenterY=-5 CenterZ=0 NormalX=0 NormalY=0 NormalZ=1 AngleXU=0 Radius=1.45
    g3: Circle CenterX=0 CenterY=10 CenterZ=0 NormalX=0 NormalY=0 NormalZ=1 AngleXU=0 Radius=3.5
    g4: Circle CenterX=8.66025 CenterY=-5 CenterZ=0 NormalX=0 NormalY=0 NormalZ=1 AngleXU=0 Radius=3.5
    g5: Circle CenterX=-8.66025 CenterY=-5 CenterZ=0 NormalX=0 NormalY=0 NormalZ=1 AngleXU=0 Radius=3.5
  constraints (12):
    c: Coincident(g0,g-6)
    c: Coincident(g1,g-7)
    c: Coincident(g2,g-8)
    c: Equal(g0,g-3)
    c: Equal(g1,g-4)
    c: Equal(g2,g-5)
    c: Coincident(g3,g0)
    c: PointOnObject(g-6,g3)
    c: Coincident(g4,g1)
    c: PointOnObject(g-7,g4)
    c: Coincident(g5,g2)
    c: PointOnObject(g-8,g5)
FEATURE [PartDesign::Pad] Pad002
  BaseFeature = -> Pocket
  Direction = (0,0,1)
  Length = 2
  Length2 = 10
  Profile = -> Sketch003
  ReferenceAxis = -> Sketch003 [N_Axis]
  Refine = true
  Suppressed = false
  Type = 0
FEATURE [Sketcher::SketchObject] Sketch004
  ArcFitTolerance = 1e-06
  AttachmentSupport = -> [Pad002]
  FullyConstrained = true
  MakeInternals = false
  MapMode = 5
  Placement = pos=(0,0,3) rot=(0,0,1;0rad)
  sketch-geometry (1):
    g0: Circle CenterX=0 CenterY=0 CenterZ=0 NormalX=0 NormalY=0 NormalZ=1 AngleXU=0 Radius=4.525
  constraints (2):
    c: Diameter(g0) = 9.05
    c: Coincident(g0,g-1)
FEATURE [PartDesign::Pad] Pad003
  BaseFeature = -> Pad002
  Direction = (0,0,1)
  Length = 10
  Length2 = 10
  Profile = -> Sketch004
  ReferenceAxis = -> Sketch004 [N_Axis]
  Refine = true
  Suppressed = false
  Type = 0
FEATURE [PartDesign::Chamfer] Chamfer
  Angle = 20
  Base = -> Pad003 [Edge71]
  BaseFeature = -> Pad003
  ChamferType = 2
  FlipDirection = false
  Refine = true
  Size = 2
  Size2 = 1
  SupportTransform = false
  Suppressed = false
  UseAllEdges = false
FEATURE [PartDesign::Body] Body  label="BackWheelConnectorBody"
  AllowCompound = false
  Group = -> [Sketch,Pad,Sketch001,Pad001,Sketch002,Pocket,Sketch003,Pad002,Sketch004,Pad003,Chamfer]
  Origin = -> Origin001
  Tip = -> Chamfer
FEATURE [App::Part] Part  label="BackWheelConnectorPart"
  Group = -> [Body]
  Origin = -> Origin
---- part ../Parts/BackWheelStopper.FCStd = doc fcstd_dda1a90d7023 ----
FCSTD DOCUMENT  (FreeCAD 1.0R39285 (Git))
Label: BackWheelStopper
License: All rights reserved
LicenseURL: https://en.wikipedia.org/wiki/All_rights_reserved
objects: Sketcher::SketchObject×2, PartDesign::Pad×2, PartDesign::Fillet×1, PartDesign::Body×1, App::Part×1
note: 14 computed .brp shape members not serialized (recipe doc carries the construction recipe); baked Part::Feature solids carry a one-line shape summary decoded from their .brp

FEATURE [Sketcher::SketchObject] Sketch
  ArcFitTolerance = 1e-06
  AttachmentSupport = -> [XY_Plane001]
  FullyConstrained = true
  MakeInternals = false
  MapMode = 5
  sketch-geometry (8):
    g0: LineSegment StartX=-14 StartY=-7.5 StartZ=0 EndX=14 EndY=-7.5 EndZ=0
    g1: LineSegment StartX=14 StartY=-7.5 StartZ=0 EndX=14 EndY=7.5 EndZ=0
    g2: LineSegment StartX=14 StartY=7.5 StartZ=0 EndX=-14 EndY=7.5 EndZ=0
    g3: LineSegment StartX=-14 StartY=7.5 StartZ=0 EndX=-14 EndY=-7.5 EndZ=0
    g4: GeomPoint [constr] X=0 Y=0 Z=0
    g5: Circle CenterX=0 CenterY=0 CenterZ=0 NormalX=0 NormalY=0 NormalZ=1 AngleXU=0 Radius=5.9
    g6: Circle CenterX=-11 CenterY=0 CenterZ=0 NormalX=0 NormalY=0 NormalZ=1 AngleXU=0 Radius=1.64
    g7: Circle CenterX=11 CenterY=0 CenterZ=0 NormalX=0 NormalY=0 NormalZ=1 AngleXU=0 Radius=1.64
  constraints (19):
    c: Coincident(g0,g1)
    c: Coincident(g1,g2)
    c: Coincident(g2,g3)
    c: Coincident(g3,g0)
    c: Horizontal(g0)
    c: Horizontal(g2)
    c: Vertical(g1)
    c: Vertical(g3)
    c: Symmetric(g2,g0,g4)
    c: Distance(g1,g3) = 28
    c: Distance(g0,g2) = 15
    c: Coincident(g4,g-1)
    c: Diameter(g5) = 11.8
    c: Coincident(g5,g4)
    c: Diameter(g6) = 3.28
    c: PointOnObject(g6,g-1)
    c: Equal(g6,g7)
    c: DistanceX(g6,g4) = 11
    c: Symmetric(g6,g7,g4)
FEATURE [PartDesign::Pad] Pad
  Direction = (0,0,1)
  Length = 2
  Length2 = 10
  Profile = -> Sketch
  ReferenceAxis = -> Sketch [N_Axis]
  Refine = true
  Suppressed = false
  Type = 0
FEATURE [Sketcher::SketchObject] Sketch001
  ArcFitTolerance = 1e-06
  AttachmentSupport = -> [Pad]
  ExternalGeometry = -> [Sketch]
  FullyConstrained = true
  MakeInternals = false
  MapMode = 5
  Placement = pos=(0,0,2) rot=(0,0,1;0rad)
  sketch-geometry (4):
    g0: Circle CenterX=-11 CenterY=0 CenterZ=0 NormalX=0 NormalY=0 NormalZ=1 AngleXU=0 Radius=1.64
    g1: Circle CenterX=11 CenterY=0 CenterZ=0 NormalX=0 NormalY=0 NormalZ=1 AngleXU=0 Radius=1.64
    g2: Circle CenterX=-11 CenterY=0 CenterZ=0 NormalX=0 NormalY=0 NormalZ=1 AngleXU=0 Radius=3
    g3: Circle CenterX=11 CenterY=0 CenterZ=0 NormalX=0 NormalY=0 NormalZ=1 AngleXU=0 Radius=3
  constraints (8):
    c: Coincident(g0,g-3)
    c: Coincident(g1,g-4)
    c: Equal(g0,g-3)
    c: Equal(g1,g-4)
    c: Diameter(g2) = 6
    c: Coincident(g2,g0)
    c: Coincident(g3,g1)
    c: Equal(g2,g3)
FEATURE [PartDesign::Pad] Pad001
  BaseFeature = -> Pad
  Direction = (0,0,1)
  Length = 1.6
  Length2 = 10
  Profile = -> Sketch001
  ReferenceAxis = -> Sketch001 [N_Axis]
  Refine = true
  Suppressed = false
  Type = 0
FEATURE [PartDesign::Fillet] Fillet
  Base = -> Pad001 [Edge2,Edge9,Edge5,Edge1]
  BaseFeature = -> Pad001
  Radius = 4
  Refine = true
  SupportTransform = false
  Suppressed = false
  UseAllEdges = false
FEATURE [PartDesign::Body] Body  label="BackWheelStopperBody"
  AllowCompound = false
  Group = -> [Sketch,Pad,Sketch001,Pad001,Fillet]
  Origin = -> Origin001
  Tip = -> Fillet
FEATURE [App::Part] Part  label="BackWheelStopperPart"
  Group = -> [Body]
  Origin = -> Origin
---- part ../Parts/Chassis.FCStd = doc fcstd_131cc8b1b5c8 ----
FCSTD DOCUMENT  (FreeCAD 1.0R39319 (Git))
Label: Chassis
License: All rights reserved
LicenseURL: https://en.wikipedia.org/wiki/All_rights_reserved
objects: Sketcher::SketchObject×18, PartDesign::Pocket×11, PartDesign::Pad×7, PartDesign::Fillet×2, App::Link×1, PartDesign::SubShapeBinder×1, PartDesign::Body×1, App::Part×1
note: 98 computed .brp shape members not serialized (recipe doc carries the construction recipe); baked Part::Feature solids carry a one-line shape summary decoded from their .brp
EXTERNAL_REF file=../Models/SteeringAckermannModel.FCStd obj=Spreadsheet
EXTERNAL_REF file=../Models/SteeringAckermannModel.FCStd obj=Part

FEATURE [App::Link] Link  label="SteeringAckermannSpreadsheet"
  LinkedObject = -> <external ../Models/SteeringAckermannModel.FCStd>#Spreadsheet
FEATURE [PartDesign::SubShapeBinder] Binder  label="SteeringAckermannModel"
  BindCopyOnChange = 0
  BindMode = 0
  ClaimChildren = false
  Context = -> Part [Body.Binder.]
  Fuse = false
  MakeFace = true
  OffsetFill = false
  OffsetIntersection = false
  OffsetJoinType = 0
  OffsetOpenResult = false
  PartialLoad = false
  Refine = true
  Relative = true
  Support = -> [<external ../Models/SteeringAckermannModel.FCStd>#Part[Sketch001.]]
  _Version = 2
FEATURE [Sketcher::SketchObject] Sketch
  ArcFitTolerance = 1e-06
  AttachmentSupport = -> [XY_Plane001]
  ExternalGeometry = -> [Binder]
  FullyConstrained = true
  MakeInternals = false
  MapMode = 5
  expr: Constraints[31] = <<SteeringAckermannSpreadsheet>>.wheeldepth / 2 + 4
  expr: Constraints[33] = <<SteeringAckermannSpreadsheet>>.wheeldia / 2 + 2
  expr: Constraints[34] = <<SteeringAckermannSpreadsheet>>.wheeldia / 2
  expr: Constraints[43] = <<SteeringAckermannSpreadsheet>>.bodywidth
  sketch-geometry (22):
    g0: LineSegment StartX=-26 StartY=4 StartZ=0 EndX=-26 EndY=-4 EndZ=0
    g1: LineSegment StartX=-26 StartY=4 StartZ=0 EndX=-10 EndY=22 EndZ=0
    g2: LineSegment StartX=-10 StartY=22 StartZ=0 EndX=10 EndY=22 EndZ=0
    g3: LineSegment StartX=-26 StartY=-4 StartZ=0 EndX=-14 EndY=-13 EndZ=0
    g4: LineSegment StartX=-14 StartY=-13 StartZ=0 EndX=-14 EndY=-41 EndZ=0
    g5: LineSegment StartX=10 StartY=22 StartZ=0 EndX=26 EndY=4 EndZ=0
    g6: LineSegment StartX=26 StartY=4 StartZ=0 EndX=26 EndY=-4 EndZ=0
    g7: LineSegment StartX=26 StartY=-4 StartZ=0 EndX=14 EndY=-13 EndZ=0
    g8: LineSegment StartX=14 StartY=-13 StartZ=0 EndX=14 EndY=-41 EndZ=0
    g9: LineSegment StartX=-14 StartY=-41 StartZ=0 EndX=-60 EndY=-41 EndZ=0
    g10: LineSegment StartX=-60 StartY=-41 StartZ=0 EndX=-60 EndY=-164 EndZ=0
    g11: LineSegment StartX=-60 StartY=-164 StartZ=0 EndX=-32 EndY=-164 EndZ=0
    g12: LineSegment StartX=-32 StartY=-164 StartZ=0 EndX=-32 EndY=-222 EndZ=0
    g13: LineSegment StartX=-32 StartY=-222 StartZ=0 EndX=32 EndY=-222 EndZ=0
    g14: LineSegment StartX=14 StartY=-41 StartZ=0 EndX=60 EndY=-41 EndZ=0
    g15: LineSegment StartX=60 StartY=-41 StartZ=0 EndX=60 EndY=-164 EndZ=0
    g16: LineSegment StartX=60 StartY=-164 StartZ=0 EndX=32 EndY=-164 EndZ=0
    g17: LineSegment StartX=32 StartY=-164 StartZ=0 EndX=32 EndY=-222 EndZ=0
    g18: Circle CenterX=-22 CenterY=0 CenterZ=0 NormalX=0 NormalY=0 NormalZ=1 AngleXU=0 Radius=1.5
    g19: Circle CenterX=22 CenterY=0 CenterZ=0 NormalX=0 NormalY=0 NormalZ=1 AngleXU=0 Radius=1.5
    g20: Circle CenterX=-11.3195 CenterY=16 CenterZ=0 NormalX=0 NormalY=0 NormalZ=1 AngleXU=0 Radius=1.5
    g21: Circle CenterX=11.3195 CenterY=16 CenterZ=0 NormalX=0 NormalY=0 NormalZ=1 AngleXU=0 Radius=1.5
  constraints (54):
    c: Distance(g0,g0) = 8
    c: Symmetric(g0,g0,g-1)
    c: Distance(g-3,g0) = 8
    c: Coincident(g1,g0)
    c: Coincident(g2,g1)
    c: DistanceX(g2,g2) = 20
    c: Distance(g-1,g2) = 22
    c: Symmetric(g1,g2,g-2)
    c: Coincident(g3,g0)
    c: Coincident(g4,g3)
    c: Vertical(g4)
    c: DistanceY(g4,g4) = 28
    c: Coincident(g5,g2)
    c: Coincident(g6,g5)
    c: Coincident(g7,g6)
    c: Coincident(g8,g7)
    c: Symmetric(g0,g5,g-2)
    c: Symmetric(g0,g6,g-2)
    c: Symmetric(g3,g7,g-2)
    c: Symmetric(g4,g8,g-2)
    c: Distance(g8,g4) = 28
    c: Coincident(g9,g4)
    c: Horizontal(g9)
    c: Coincident(g10,g9)
    c: Vertical(g10)
    c: Coincident(g11,g10)
    c: Horizontal(g11)
    c: Coincident(g12,g11)
    c: Vertical(g12)
    c: Coincident(g13,g12)
    c: DistanceY(g10,g10) = 123
    c: Distance(g-5,g12) = 16
    c: Symmetric(g12,g13,g-2)
    c: DistanceY(g-7,g11) = 30
    c: DistanceY(g12,g-7) = 28
    c: Coincident(g14,g8)
    c: Coincident(g15,g14)
    c: Coincident(g16,g15)
    c: Coincident(g17,g16)
    c: Coincident(g17,g13)
    c: Symmetric(g9,g14,g-2)
    c: Symmetric(g10,g15,g-2)
    c: Symmetric(g11,g16,g-2)
    c: Distance(g15,g10) = 120
    c: Diameter(g18) = 3
    c: PointOnObject(g18,g-1)
    c: Distance(g18,g0) = 4
    c: Symmetric(g18,g19,g-2)
    c: Diameter(g20) = 3
    c: Equal(g18,g19)
    c: Distance(g20,g1) = 3
    c: DistanceY(g20,g1) = 6
    c: Symmetric(g20,g21,g-2)
    c: Equal(g20,g21)
FEATURE [PartDesign::Pad] Pad
  Direction = (0,0,1)
  Length = 8
  Length2 = 10
  Profile = -> Sketch
  ReferenceAxis = -> Sketch [N_Axis]
  Refine = true
  Suppressed = false
  Type = 0
FEATURE [Sketcher::SketchObject] Sketch001
  ArcFitTolerance = 1e-06
  AttachmentSupport = -> [Pad]
  ExternalGeometry = -> [Sketch]
  FullyConstrained = true
  MakeInternals = false
  MapMode = 5
  Placement = pos=(0,0,8) rot=(0,0,1;0rad)
  sketch-geometry (16):
    g0: LineSegment StartX=-26 StartY=-4 StartZ=0 EndX=-26 EndY=4 EndZ=0
    g1: LineSegment StartX=-26 StartY=4 StartZ=0 EndX=-10 EndY=22 EndZ=0
    g2: LineSegment StartX=10 StartY=22 StartZ=0 EndX=26 EndY=4 EndZ=0
    g3: LineSegment StartX=26 StartY=4 StartZ=0 EndX=26 EndY=-4 EndZ=0
    g4: Circle CenterX=-22 CenterY=0 CenterZ=0 NormalX=0 NormalY=0 NormalZ=1 AngleXU=0 Radius=1.5
    g5: Circle CenterX=-11.3195 CenterY=16 CenterZ=0 NormalX=0 NormalY=0 NormalZ=1 AngleXU=0 Radius=1.5
    g6: Circle CenterX=11.3195 CenterY=16 CenterZ=0 NormalX=0 NormalY=0 NormalZ=1 AngleXU=0 Radius=1.5
    g7: Circle CenterX=22 CenterY=0 CenterZ=0 NormalX=0 NormalY=0 NormalZ=1 AngleXU=0 Radius=1.5
    g8: LineSegment StartX=-10 StartY=22 StartZ=0 EndX=-8 EndY=22 EndZ=0
    g9: LineSegment StartX=-26 StartY=-4 StartZ=0 EndX=-11.3 EndY=-4 EndZ=0
    g10: LineSegment StartX=-11.3 StartY=-4 StartZ=0 EndX=-8 EndY=-2.75 EndZ=0
    g11: LineSegment StartX=-8 StartY=22 StartZ=0 EndX=-8 EndY=-2.75 EndZ=0
    g12: LineSegment StartX=10 StartY=22 StartZ=0 EndX=8 EndY=22 EndZ=0
    g13: LineSegment StartX=8 StartY=22 StartZ=0 EndX=8 EndY=-2.75 EndZ=0
    g14: LineSegment StartX=8 StartY=-2.75 StartZ=0 EndX=11.3 EndY=-4 EndZ=0
    g15: LineSegment StartX=11.3 StartY=-4 StartZ=0 EndX=26 EndY=-4 EndZ=0
  constraints (35):
    c: Coincident(g0,g-4)
    c: Coincident(g0,g-5)
    c: Coincident(g1,g0)
    c: Coincident(g1,g-6)
    c: Coincident(g2,g-8)
    c: Coincident(g3,g2)
    c: Coincident(g3,g-8)
    c: Coincident(g4,g-3)
    c: Equal(g4,g-3)
    c: Coincident(g5,g-9)
    c: Equal(g5,g-9)
    c: Coincident(g6,g-10)
    c: Equal(g6,g-10)
    c: Coincident(g7,g-11)
    c: Equal(g7,g-11)
    c: Coincident(g2,g-7)
    c: Coincident(g8,g1)
    c: PointOnObject(g8,g-6)
    c: Coincident(g9,g0)
    c: Horizontal(g9)
    c: Coincident(g10,g9)
    c: Coincident(g11,g8)
    c: Coincident(g11,g10)
    c: Vertical(g11)
    c: DistanceY(g11,g11) = 24.75
    c: DistanceX(g9,g9) = 14.7
    c: Coincident(g12,g2)
    c: Coincident(g13,g12)
    c: Coincident(g14,g13)
    c: Coincident(g15,g14)
    c: Coincident(g15,g3)
    c: Symmetric(g8,g12,g-2)
    c: Symmetric(g10,g13,g-2)
    c: Symmetric(g9,g14,g-2)
    c: DistanceX(g10,g13) = 16
FEATURE [PartDesign::Pad] Pad001
  BaseFeature = -> Pad
  Direction = (0,0,1)
  Length = 5.5
  Length2 = 10
  Profile = -> Sketch001
  ReferenceAxis = -> Sketch001 [N_Axis]
  Refine = true
  Suppressed = false
  Type = 0
  expr: Length = <<SteeringAckermannSpreadsheet>>.wheeldia / 2 - 8 - 8 - 3 - 7 / 2
FEATURE [Sketcher::SketchObject] Sketch002
  ArcFitTolerance = 1e-06
  AttachmentSupport = -> [Pad001]
  ExternalGeometry = -> [Sketch001,Binder]
  FullyConstrained = true
  MakeInternals = false
  MapMode = 5
  Placement = pos=(0,0,13.5) rot=(0,0,1;0rad)
  sketch-geometry (22):
    g0: LineSegment StartX=-26 StartY=4 StartZ=0 EndX=-10 EndY=22 EndZ=0
    g1: LineSegment StartX=-10 StartY=22 StartZ=0 EndX=-8 EndY=22 EndZ=0
    g2: LineSegment StartX=-8 StartY=22 StartZ=0 EndX=-8 EndY=-2.75 EndZ=0
    g3: LineSegment StartX=-8 StartY=-2.75 StartZ=0 EndX=-11.3 EndY=-4 EndZ=0
    g4: LineSegment StartX=-11.3 StartY=-4 StartZ=0 EndX=-26 EndY=-4 EndZ=0
    g5: LineSegment StartX=26 StartY=4 StartZ=0 EndX=10 EndY=22 EndZ=0
    g6: LineSegment StartX=10 StartY=22 StartZ=0 EndX=8 EndY=22 EndZ=0
    g7: LineSegment StartX=8 StartY=22 StartZ=0 EndX=8 EndY=-2.75 EndZ=0
    g8: LineSegment StartX=8 StartY=-2.75 StartZ=0 EndX=11.3 EndY=-4 EndZ=0
    g9: LineSegment StartX=11.3 StartY=-4 StartZ=0 EndX=26 EndY=-4 EndZ=0
    g10: Circle CenterX=-22 CenterY=0 CenterZ=0 NormalX=0 NormalY=0 NormalZ=1 AngleXU=0 Radius=1.5
    g11: Circle CenterX=-11.3195 CenterY=16 CenterZ=0 NormalX=0 NormalY=0 NormalZ=1 AngleXU=0 Radius=1.5
    g12: Circle CenterX=22 CenterY=0 CenterZ=0 NormalX=0 NormalY=0 NormalZ=1 AngleXU=0 Radius=1.5
    g13: Circle CenterX=11.3195 CenterY=16 CenterZ=0 NormalX=0 NormalY=0 NormalZ=1 AngleXU=0 Radius=1.5
    g14: Circle CenterX=-34 CenterY=0 CenterZ=0 NormalX=0 NormalY=0 NormalZ=1 AngleXU=0 Radius=1.5
    g15: Circle CenterX=34 CenterY=0 CenterZ=0 NormalX=0 NormalY=0 NormalZ=1 AngleXU=0 Radius=1.5
    g16: ArcOfCircle CenterX=-34 CenterY=0 CenterZ=0 NormalX=0 NormalY=0 NormalZ=1 AngleXU=0 Radius=4 StartAngle=1.5708 EndAngle=4.71239
    g17: LineSegment StartX=-26 StartY=-4 StartZ=0 EndX=-34 EndY=-4 EndZ=0
    g18: LineSegment StartX=-26 StartY=4 StartZ=0 EndX=-34 EndY=4 EndZ=0
    g19: ArcOfCircle CenterX=34 CenterY=0 CenterZ=0 NormalX=0 NormalY=0 NormalZ=1 AngleXU=0 Radius=4 StartAngle=4.71239 EndAngle=7.85398
    g20: LineSegment StartX=26 StartY=-4 StartZ=0 EndX=34 EndY=-4 EndZ=0
    g21: LineSegment StartX=26 StartY=4 StartZ=0 EndX=34 EndY=4 EndZ=0
  constraints (44):
    c: Coincident(g0,g-3)
    c: Coincident(g0,g-4)
    c: Coincident(g1,g0)
    c: Coincident(g1,g-5)
    c: Coincident(g2,g1)
    c: Coincident(g2,g-6)
    c: Coincident(g3,g2)
    c: Coincident(g3,g-7)
    c: Coincident(g4,g3)
    c: Coincident(g4,g-7)
    c: Coincident(g5,g-12)
    c: Coincident(g5,g-12)
    c: Coincident(g6,g5)
    c: Coincident(g6,g-11)
    c: Coincident(g7,g6)
    c: Coincident(g7,g-13)
    c: Coincident(g8,g7)
    c: Coincident(g8,g-14)
    c: Coincident(g9,g8)
    c: Coincident(g9,g-14)
    c: Coincident(g10,g-8)
    c: Equal(g10,g-8)
    c: Coincident(g11,g-9)
    c: Equal(g11,g-9)
    c: Coincident(g12,g-15)
    c: Equal(g12,g-15)
    c: Coincident(g13,g-16)
    c: Equal(g13,g-16)
    c: Diameter(g14) = 3
    c: Coincident(g14,g-17)
    c: Coincident(g15,g-18)
    c: Equal(g14,g15)
    c: Coincident(g16,g14)
    c: Coincident(g17,g4)
    c: Coincident(g18,g0)
    c: Tangent(g18,g16) = -1.5708
    c: Tangent(g17,g16) = 1.5708
    c: Horizontal(g17)
    c: Coincident(g19,g15)
    c: Coincident(g20,g9)
    c: Coincident(g21,g5)
    c: Tangent(g20,g19) = -1.5708
    c: Tangent(g21,g19) = 1.5708
    c: Horizontal(g20)
FEATURE [PartDesign::Pad] Pad002
  BaseFeature = -> Pad001
  Direction = (0,0,1)
  Length = 3
  Length2 = 10
  Profile = -> Sketch002
  ReferenceAxis = -> Sketch002 [N_Axis]
  Refine = true
  Suppressed = false
  Type = 0
FEATURE [Sketcher::SketchObject] Sketch003
  ArcFitTolerance = 1e-06
  AttachmentSupport = -> [Pad002]
  ExternalGeometry = -> [Sketch]
  FullyConstrained = true
  MakeInternals = false
  MapMode = 5
  Placement = pos=(0,0,16.5) rot=(0,0,1;0rad)
  expr: Constraints[24] = Sketch001.Constraints[24]
  expr: Constraints[25] = Sketch001.Constraints[25]
  expr: Constraints[34] = Sketch001.Constraints[34]
  sketch-geometry (16):
    g0: LineSegment StartX=-26 StartY=-4 StartZ=0 EndX=-26 EndY=4 EndZ=0
    g1: LineSegment StartX=-26 StartY=4 StartZ=0 EndX=-10 EndY=22 EndZ=0
    g2: LineSegment StartX=10 StartY=22 StartZ=0 EndX=26 EndY=4 EndZ=0
    g3: LineSegment StartX=26 StartY=4 StartZ=0 EndX=26 EndY=-4 EndZ=0
    g4: Circle CenterX=-22 CenterY=0 CenterZ=0 NormalX=0 NormalY=0 NormalZ=1 AngleXU=0 Radius=1.5
    g5: Circle CenterX=-11.3195 CenterY=16 CenterZ=0 NormalX=0 NormalY=0 NormalZ=1 AngleXU=0 Radius=1.5
    g6: Circle CenterX=11.3195 CenterY=16 CenterZ=0 NormalX=0 NormalY=0 NormalZ=1 AngleXU=0 Radius=1.5
    g7: Circle CenterX=22 CenterY=0 CenterZ=0 NormalX=0 NormalY=0 NormalZ=1 AngleXU=0 Radius=1.5
    g8: LineSegment StartX=-10 StartY=22 StartZ=0 EndX=-8 EndY=22 EndZ=0
    g9: LineSegment StartX=-26 StartY=-4 StartZ=0 EndX=-11.3 EndY=-4 EndZ=0
    g10: LineSegment StartX=-11.3 StartY=-4 StartZ=0 EndX=-8 EndY=-2.75 EndZ=0
    g11: LineSegment StartX=-8 StartY=22 StartZ=0 EndX=-8 EndY=-2.75 EndZ=0
    g12: LineSegment StartX=10 StartY=22 StartZ=0 EndX=8 EndY=22 EndZ=0
    g13: LineSegment StartX=8 StartY=22 StartZ=0 EndX=8 EndY=-2.75 EndZ=0
    g14: LineSegment StartX=8 StartY=-2.75 StartZ=0 EndX=11.3 EndY=-4 EndZ=0
    g15: LineSegment StartX=11.3 StartY=-4 StartZ=0 EndX=26 EndY=-4 EndZ=0
  constraints (35):
    c: Coincident(g0,g-4)
    c: Coincident(g0,g-5)
    c: Coincident(g1,g0)
    c: Coincident(g1,g-6)
    c: Coincident(g2,g-8)
    c: Coincident(g3,g2)
    c: Coincident(g3,g-8)
    c: Coincident(g4,g-3)
    c: Equal(g4,g-3)
    c: Coincident(g5,g-9)
    c: Equal(g5,g-9)
    c: Coincident(g6,g-10)
    c: Equal(g6,g-10)
    c: Coincident(g7,g-11)
    c: Equal(g7,g-11)
    c: Coincident(g2,g-7)
    c: Coincident(g8,g1)
    c: PointOnObject(g8,g-6)
    c: Coincident(g9,g0)
    c: Horizontal(g9)
    c: Coincident(g10,g9)
    c: Coincident(g11,g8)
    c: Coincident(g11,g10)
    c: Vertical(g11)
    c: DistanceY(g11,g11) = 24.75
    c: DistanceX(g9,g9) = 14.7
    c: Coincident(g12,g2)
    c: Coincident(g13,g12)
    c: Coincident(g14,g13)
    c: Coincident(g15,g14)
    c: Coincident(g15,g3)
    c: Symmetric(g8,g12,g-2)
    c: Symmetric(g10,g13,g-2)
    c: Symmetric(g9,g14,g-2)
    c: DistanceX(g10,g13) = 16
FEATURE [PartDesign::Pad] Pad003
  BaseFeature = -> Pad002
  Direction = (0,0,1)
  Length = 7
  Length2 = 10
  Profile = -> Sketch003
  ReferenceAxis = -> Sketch003 [N_Axis]
  Refine = true
  Suppressed = false
  Type = 0
FEATURE [Sketcher::SketchObject] Sketch004
  ArcFitTolerance = 1e-06
  AttachmentSupport = -> [Pad003]
  ExternalGeometry = -> [Binder,Pad003]
  FullyConstrained = true
  MakeInternals = false
  MapMode = 5
  Placement = pos=(0,0,8) rot=(0,0,1;0rad)
  sketch-geometry (14):
    g0: LineSegment StartX=-23 StartY=-179 StartZ=0 EndX=-23 EndY=-209 EndZ=0
    g1: LineSegment [constr] StartX=-23 StartY=-209 StartZ=0 EndX=-16 EndY=-209 EndZ=0
    g2: LineSegment StartX=-16 StartY=-209 StartZ=0 EndX=-16 EndY=-179 EndZ=0
    g3: LineSegment StartX=-16 StartY=-179 StartZ=0 EndX=-23 EndY=-179 EndZ=0
    g4: LineSegment StartX=-23 StartY=-222 StartZ=0 EndX=-16 EndY=-222 EndZ=0
    g5: LineSegment StartX=-23 StartY=-222 StartZ=0 EndX=-23 EndY=-209 EndZ=0
    g6: LineSegment StartX=-16 StartY=-222 StartZ=0 EndX=-16 EndY=-209 EndZ=0
    g7: LineSegment StartX=23 StartY=-179 StartZ=0 EndX=23 EndY=-209 EndZ=0
    g8: LineSegment [constr] StartX=23 StartY=-209 StartZ=0 EndX=16 EndY=-209 EndZ=0
    g9: LineSegment StartX=16 StartY=-209 StartZ=0 EndX=16 EndY=-179 EndZ=0
    g10: LineSegment StartX=16 StartY=-179 StartZ=0 EndX=23 EndY=-179 EndZ=0
    g11: LineSegment StartX=23 StartY=-222 StartZ=0 EndX=16 EndY=-222 EndZ=0
    g12: LineSegment StartX=23 StartY=-222 StartZ=0 EndX=23 EndY=-209 EndZ=0
    g13: LineSegment StartX=16 StartY=-222 StartZ=0 EndX=16 EndY=-209 EndZ=0
  constraints (33):
    c: Coincident(g0,g1)
    c: Coincident(g1,g2)
    c: Coincident(g2,g3)
    c: Coincident(g3,g0)
    c: Vertical(g2)
    c: Horizontal(g1)
    c: Horizontal(g3)
    c: Symmetric(g0,g0,g-3)
    c: PointOnObject(g4,g-4)
    c: PointOnObject(g4,g-4)
    c: Coincident(g5,g4)
    c: Coincident(g5,g0)
    c: Vertical(g5)
    c: Coincident(g6,g4)
    c: Coincident(g6,g1)
    c: Vertical(g6)
    c: DistanceY(g0,g0) = 30
    c: DistanceX(g3,g3) = 7
    c: Coincident(g7,g8)
    c: Coincident(g8,g9)
    c: Coincident(g9,g10)
    c: Coincident(g10,g7)
    c: Coincident(g12,g11)
    c: Coincident(g12,g7)
    c: Coincident(g13,g11)
    c: Coincident(g13,g8)
    c: Symmetric(g4,g11,g-2)
    c: Symmetric(g4,g11,g-2)
    c: Symmetric(g1,g8,g-2)
    c: Symmetric(g0,g7,g-2)
    c: Symmetric(g2,g9,g-2)
    c: Symmetric(g0,g7,g-2)
    c: DistanceX(g2,g9) = 32
FEATURE [PartDesign::Pad] Pad004
  BaseFeature = -> Pad003
  Direction = (0,0,1)
  Length = 51
  Length2 = 10
  Profile = -> Sketch004
  ReferenceAxis = -> Sketch004 [N_Axis]
  Refine = true
  Suppressed = false
  Type = 0
FEATURE [Sketcher::SketchObject] Sketch005
  ArcFitTolerance = 1e-06
  AttachmentSupport = -> [Pad004]
  ExternalGeometry = -> [Pad004,Sketch004]
  FullyConstrained = true
  MakeInternals = false
  MapMode = 5
  Placement = pos=(-23,0,0) rot=(0.57735,-0.57735,-0.57735;2.0944rad)
  expr: Constraints[3] = <<SteeringAckermannSpreadsheet>>.wheeldia / 2 - 8 - 8 + 24 / 2
  sketch-geometry (12):
    g0: LineSegment [constr] StartX=194 StartY=59 StartZ=0 EndX=194 EndY=8 EndZ=0
    g1: LineSegment [constr] StartX=179 StartY=32 StartZ=0 EndX=222 EndY=32 EndZ=0
    g2: LineSegment StartX=186.5 StartY=15.5 StartZ=0 EndX=201.5 EndY=15.5 EndZ=0
    g3: LineSegment StartX=201.5 StartY=15.5 StartZ=0 EndX=201.5 EndY=24.5 EndZ=0
    g4: LineSegment StartX=201.5 StartY=24.5 StartZ=0 EndX=186.5 EndY=24.5 EndZ=0
    g5: LineSegment StartX=186.5 StartY=24.5 StartZ=0 EndX=186.5 EndY=15.5 EndZ=0
    g6: GeomPoint [constr] X=194 Y=20 Z=0
    g7: LineSegment StartX=186.5 StartY=48.5 StartZ=0 EndX=201.5 EndY=48.5 EndZ=0
    g8: LineSegment StartX=201.5 StartY=48.5 StartZ=0 EndX=201.5 EndY=39.5 EndZ=0
    g9: LineSegment StartX=201.5 StartY=39.5 StartZ=0 EndX=186.5 EndY=39.5 EndZ=0
    g10: LineSegment StartX=186.5 StartY=39.5 StartZ=0 EndX=186.5 EndY=48.5 EndZ=0
    g11: LineSegment [constr] StartX=209 StartY=8 StartZ=0 EndX=209 EndY=59 EndZ=0
  constraints (30):
    c: PointOnObject(g1,g-5)
    c: PointOnObject(g1,g-6)
    c: Horizontal(g1)
    c: DistanceY(g-5,g1) = 24
    c: Coincident(g2,g3)
    c: Coincident(g3,g4)
    c: Coincident(g4,g5)
    c: Coincident(g5,g2)
    c: Horizontal(g2)
    c: Horizontal(g4)
    c: Vertical(g3)
    c: Vertical(g5)
    c: Symmetric(g4,g2,g6)
    c: PointOnObject(g6,g0)
    c: DistanceX(g2,g2) = 15
    c: DistanceY(g5,g5) = 9
    c: Distance(g6,g1) = 12
    c: Coincident(g7,g8)
    c: Coincident(g8,g9)
    c: Coincident(g9,g10)
    c: Coincident(g10,g7)
    c: Symmetric(g4,g9,g1)
    c: Symmetric(g7,g2,g1)
    c: Symmetric(g8,g3,g1)
    c: Symmetric(g7,g2,g1)
    c: Coincident(g11,g-7)
    c: PointOnObject(g11,g-4)
    c: Vertical(g11)
    c: Symmetric(g-5,g11,g0)
    c: Symmetric(g-5,g11,g0)
FEATURE [PartDesign::Pocket] Pocket
  BaseFeature = -> Pad004
  Direction = (1,0,0)
  Length = 3
  Length2 = 5
  Profile = -> Sketch005
  ReferenceAxis = -> Sketch005 [N_Axis]
  Refine = true
  Suppressed = false
  Type = 0
FEATURE [Sketcher::SketchObject] Sketch006
  ArcFitTolerance = 1e-06
  AttachmentSupport = -> [Pocket]
  ExternalGeometry = -> [Sketch005]
  FullyConstrained = true
  MakeInternals = false
  MapMode = 5
  Placement = pos=(-20,0,0) rot=(0.57735,-0.57735,-0.57735;2.0944rad)
  sketch-geometry (9):
    g0: LineSegment [constr] StartX=194 StartY=15.5 StartZ=0 EndX=194 EndY=48.5 EndZ=0
    g1: LineSegment StartX=189.5 StartY=15.5 StartZ=0 EndX=198.5 EndY=15.5 EndZ=0
    g2: LineSegment StartX=198.5 StartY=15.5 StartZ=0 EndX=198.5 EndY=24.5 EndZ=0
    g3: LineSegment StartX=198.5 StartY=24.5 StartZ=0 EndX=189.5 EndY=24.5 EndZ=0
    g4: LineSegment StartX=189.5 StartY=24.5 StartZ=0 EndX=189.5 EndY=15.5 EndZ=0
    g5: LineSegment StartX=189.5 StartY=48.5 StartZ=0 EndX=189.5 EndY=39.5 EndZ=0
    g6: LineSegment StartX=189.5 StartY=39.5 StartZ=0 EndX=198.5 EndY=39.5 EndZ=0
    g7: LineSegment StartX=198.5 StartY=39.5 StartZ=0 EndX=198.5 EndY=48.5 EndZ=0
    g8: LineSegment StartX=198.5 StartY=48.5 StartZ=0 EndX=189.5 EndY=48.5 EndZ=0
  constraints (24):
    c: Symmetric(g-3,g-3,g0)
    c: Symmetric(g-6,g-6,g0)
    c: Coincident(g1,g2)
    c: Coincident(g2,g3)
    c: Coincident(g3,g4)
    c: Coincident(g4,g1)
    c: Horizontal(g1)
    c: Vertical(g2)
    c: Vertical(g4)
    c: PointOnObject(g1,g-3)
    c: PointOnObject(g2,g-4)
    c: Symmetric(g3,g2,g0)
    c: Equal(g3,g4)
    c: Coincident(g5,g6)
    c: Coincident(g6,g7)
    c: Coincident(g7,g8)
    c: Coincident(g8,g5)
    c: Vertical(g5)
    c: Vertical(g7)
    c: Horizontal(g8)
    c: PointOnObject(g5,g-6)
    c: PointOnObject(g6,g-5)
    c: Symmetric(g5,g6,g0)
    c: Equal(g6,g5)
FEATURE [PartDesign::Pocket] Pocket001
  BaseFeature = -> Pocket
  Direction = (1,0,0)
  Length = 0
  Length2 = 5
  Profile = -> Sketch006
  ReferenceAxis = -> Sketch006 [N_Axis]
  Refine = true
  Suppressed = false
  Type = 3
  UpToFace = -> Pocket [Face35]
FEATURE [Sketcher::SketchObject] Sketch007
  ArcFitTolerance = 1e-06
  AttachmentSupport = -> [Pocket001]
  ExternalGeometry = -> [Sketch005]
  FullyConstrained = true
  MakeInternals = false
  MapMode = 5
  Placement = pos=(-23,0,0) rot=(0.57735,-0.57735,-0.57735;2.0944rad)
  sketch-geometry (6):
    g0: Circle CenterX=183 CenterY=20 CenterZ=0 NormalX=0 NormalY=0 NormalZ=1 AngleXU=0 Radius=1.45
    g1: Circle CenterX=205 CenterY=20 CenterZ=0 NormalX=0 NormalY=0 NormalZ=1 AngleXU=0 Radius=1.45
    g2: LineSegment [constr] StartX=183 StartY=20 StartZ=0 EndX=205 EndY=20 EndZ=0
    g3: GeomPoint X=186.5 Y=20 Z=0
    g4: GeomPoint X=201.5 Y=20 Z=0
    g5: GeomPoint X=194 Y=20 Z=0
  constraints (11):
    c: Diameter(g0) = 2.9
    c: Equal(g0,g1)
    c: Coincident(g2,g0)
    c: Coincident(g2,g1)
    c: Symmetric(g-3,g-3,g2)
    c: PointOnObject(g3,g2)
    c: PointOnObject(g3,g-3)
    c: PointOnObject(g4,g-4)
    c: Symmetric(g3,g4,g5)
    c: Symmetric(g0,g1,g5)
    c: Distance(g0,g-3) = 3.5
FEATURE [PartDesign::Pocket] Pocket002
  BaseFeature = -> Pocket001
  Direction = (1,0,0)
  Length = 0
  Length2 = 5
  Profile = -> Sketch007
  ReferenceAxis = -> Sketch007 [N_Axis]
  Refine = true
  Suppressed = false
  Type = 3
  UpToFace = -> Pocket001 [Face35]
FEATURE [Sketcher::SketchObject] Sketch008
  ArcFitTolerance = 1e-06
  AttachmentSupport = -> [Pocket002]
  ExternalGeometry = -> [Pad004,Sketch004]
  FullyConstrained = true
  MakeInternals = false
  MapMode = 5
  Placement = pos=(23,0,0) rot=(0.57735,0.57735,0.57735;2.0944rad)
  expr: Constraints[14] = Sketch005.Constraints[14]
  expr: Constraints[15] = Sketch005.Constraints[15]
  expr: Constraints[16] = Sketch005.Constraints[16]
  expr: Constraints[3] = Sketch005.Constraints[3]
  sketch-geometry (8):
    g0: LineSegment [constr] StartX=-194 StartY=59 StartZ=0 EndX=-194 EndY=8 EndZ=0
    g1: LineSegment [constr] StartX=-179 StartY=32 StartZ=0 EndX=-222 EndY=32 EndZ=0
    g2: LineSegment StartX=-201.5 StartY=15.5 StartZ=0 EndX=-186.5 EndY=15.5 EndZ=0
    g3: LineSegment StartX=-186.5 StartY=15.5 StartZ=0 EndX=-186.5 EndY=24.5 EndZ=0
    g4: LineSegment StartX=-186.5 StartY=24.5 StartZ=0 EndX=-201.5 EndY=24.5 EndZ=0
    g5: LineSegment StartX=-201.5 StartY=24.5 StartZ=0 EndX=-201.5 EndY=15.5 EndZ=0
    g6: GeomPoint [constr] X=-194 Y=20 Z=0
    g7: LineSegment [constr] StartX=-209 StartY=8 StartZ=0 EndX=-209 EndY=59 EndZ=0
  constraints (22):
    c: PointOnObject(g1,g-5)
    c: PointOnObject(g1,g-6)
    c: Horizontal(g1)
    c: DistanceY(g-5,g1) = 24
    c: Coincident(g2,g3)
    c: Coincident(g3,g4)
    c: Coincident(g4,g5)
    c: Coincident(g5,g2)
    c: Horizontal(g2)
    c: Horizontal(g4)
    c: Vertical(g3)
    c: Vertical(g5)
    c: Symmetric(g4,g2,g6)
    c: PointOnObject(g6,g0)
    c: DistanceX(g2,g2) = 15
    c: DistanceY(g5,g5) = 9
    c: Distance(g6,g1) = 12
    c: Coincident(g7,g-7)
    c: PointOnObject(g7,g-4)
    c: Vertical(g7)
    c: Symmetric(g-5,g7,g0)
    c: Symmetric(g-5,g7,g0)
FEATURE [PartDesign::Pocket] Pocket003
  BaseFeature = -> Pocket002
  Direction = (-1,0,0)
  Length = 3
  Length2 = 5
  Profile = -> Sketch008
  ReferenceAxis = -> Sketch008 [N_Axis]
  Refine = true
  Suppressed = false
  Type = 0
FEATURE [Sketcher::SketchObject] Sketch009
  ArcFitTolerance = 1e-06
  AttachmentSupport = -> [Pocket003]
  ExternalGeometry = -> [Sketch005]
  FullyConstrained = true
  MakeInternals = false
  MapMode = 5
  Placement = pos=(20,0,0) rot=(0.57735,0.57735,0.57735;2.0944rad)
  sketch-geometry (5):
    g0: LineSegment [constr] StartX=-194 StartY=15.5 StartZ=0 EndX=-194 EndY=48.5 EndZ=0
    g1: LineSegment StartX=-198.5 StartY=15.5 StartZ=0 EndX=-189.5 EndY=15.5 EndZ=0
    g2: LineSegment StartX=-189.5 StartY=15.5 StartZ=0 EndX=-189.5 EndY=24.5 EndZ=0
    g3: LineSegment StartX=-189.5 StartY=24.5 StartZ=0 EndX=-198.5 EndY=24.5 EndZ=0
    g4: LineSegment StartX=-198.5 StartY=24.5 StartZ=0 EndX=-198.5 EndY=15.5 EndZ=0
  constraints (13):
    c: Symmetric(g-3,g-3,g0)
    c: Symmetric(g-6,g-6,g0)
    c: Coincident(g1,g2)
    c: Coincident(g2,g3)
    c: Coincident(g3,g4)
    c: Coincident(g4,g1)
    c: Horizontal(g1)
    c: Vertical(g2)
    c: Vertical(g4)
    c: PointOnObject(g1,g-3)
    c: PointOnObject(g2,g-4)
    c: Symmetric(g3,g2,g0)
    c: Equal(g3,g4)
FEATURE [PartDesign::Pocket] Pocket004
  BaseFeature = -> Pocket003
  Direction = (-1,0,0)
  Length = 0
  Length2 = 5
  Profile = -> Sketch009
  ReferenceAxis = -> Sketch009 [N_Axis]
  Refine = true
  Suppressed = false
  Type = 3
  UpToFace = -> Pocket003 [Face34]
FEATURE [Sketcher::SketchObject] Sketch010
  ArcFitTolerance = 1e-06
  AttachmentSupport = -> [Pocket004]
  ExternalGeometry = -> [Sketch005]
  FullyConstrained = true
  MakeInternals = false
  MapMode = 5
  Placement = pos=(23,0,0) rot=(0.57735,0.57735,0.57735;2.0944rad)
  expr: Constraints[0] = Sketch007.Constraints[0]
  expr: Constraints[10] = Sketch007.Constraints[10]
  sketch-geometry (6):
    g0: Circle CenterX=-183 CenterY=20 CenterZ=0 NormalX=0 NormalY=0 NormalZ=1 AngleXU=0 Radius=1.45
    g1: Circle CenterX=-205 CenterY=20 CenterZ=0 NormalX=0 NormalY=0 NormalZ=1 AngleXU=0 Radius=1.45
    g2: LineSegment [constr] StartX=-183 StartY=20 StartZ=0 EndX=-205 EndY=20 EndZ=0
    g3: GeomPoint X=-186.5 Y=20 Z=0
    g4: GeomPoint X=-201.5 Y=20 Z=0
    g5: GeomPoint X=-194 Y=20 Z=0
  constraints (11):
    c: Diameter(g0) = 2.9
    c: Equal(g0,g1)
    c: Coincident(g2,g0)
    c: Coincident(g2,g1)
    c: Symmetric(g-3,g-3,g2)
    c: PointOnObject(g3,g2)
    c: PointOnObject(g3,g-3)
    c: PointOnObject(g4,g-4)
    c: Symmetric(g3,g4,g5)
    c: Symmetric(g0,g1,g5)
    c: Distance(g0,g-3) = 3.5
FEATURE [PartDesign::Pocket] Pocket005
  BaseFeature = -> Pocket004
  Direction = (-1,0,0)
  Length = 0
  Length2 = 5
  Profile = -> Sketch010
  ReferenceAxis = -> Sketch010 [N_Axis]
  Refine = true
  Suppressed = false
  Type = 3
  UpToFace = -> Pocket004 [Face34]
FEATURE [Sketcher::SketchObject] Sketch011
  ArcFitTolerance = 1e-06
  AttachmentSupport = -> [Pocket005]
  ExternalGeometry = -> [Pad004,Sketch004]
  FullyConstrained = true
  MakeInternals = false
  MapMode = 5
  Placement = pos=(23,0,0) rot=(0.57735,0.57735,0.57735;2.0944rad)
  expr: Constraints[3] = Sketch005.Constraints[3]
  sketch-geometry (8):
    g0: LineSegment [constr] StartX=-194 StartY=59 StartZ=0 EndX=-194 EndY=8 EndZ=0
    g1: LineSegment [constr] StartX=-179 StartY=32 StartZ=0 EndX=-222 EndY=32 EndZ=0
    g2: LineSegment [constr] StartX=-209 StartY=8 StartZ=0 EndX=-209 EndY=59 EndZ=0
    g3: GeomPoint X=-194 Y=44 Z=0
    g4: LineSegment StartX=-201.5 StartY=37 StartZ=0 EndX=-186.5 EndY=37 EndZ=0
    g5: LineSegment StartX=-186.5 StartY=37 StartZ=0 EndX=-186.5 EndY=59 EndZ=0
    g6: LineSegment StartX=-186.5 StartY=59 StartZ=0 EndX=-201.5 EndY=59 EndZ=0
    g7: LineSegment StartX=-201.5 StartY=59 StartZ=0 EndX=-201.5 EndY=37 EndZ=0
  constraints (21):
    c: PointOnObject(g1,g-5)
    c: PointOnObject(g1,g-6)
    c: Horizontal(g1)
    c: DistanceY(g-5,g1) = 24
    c: Coincident(g2,g-7)
    c: PointOnObject(g2,g-4)
    c: Vertical(g2)
    c: Symmetric(g-5,g2,g0)
    c: Symmetric(g-5,g2,g0)
    c: PointOnObject(g3,g0)
    c: Distance(g3,g1) = 12
    c: Coincident(g4,g5)
    c: Coincident(g5,g6)
    c: Coincident(g6,g7)
    c: Coincident(g7,g4)
    c: Vertical(g5)
    c: PointOnObject(g5,g-4)
    c: Symmetric(g4,g4,g0)
    c: Symmetric(g5,g6,g0)
    c: DistanceX(g4,g4) = 15
    c: Distance(g3,g4) = 7
FEATURE [PartDesign::Pocket] Pocket006
  BaseFeature = -> Pocket005
  Direction = (-1,0,0)
  Length = 0
  Length2 = 5
  Profile = -> Sketch011
  ReferenceAxis = -> Sketch011 [N_Axis]
  Refine = true
  Suppressed = false
  Type = 3
  UpToFace = -> Pocket005 [Face34]
FEATURE [Sketcher::SketchObject] Sketch012
  ArcFitTolerance = 1e-06
  AttachmentSupport = -> [Pocket006]
  ExternalGeometry = -> [Sketch004]
  FullyConstrained = true
  MakeInternals = false
  MapMode = 5
  Placement = pos=(0,0,59) rot=(0,0,1;0rad)
  sketch-geometry (6):
    g0: Circle CenterX=-19.5 CenterY=-182 CenterZ=0 NormalX=0 NormalY=0 NormalZ=1 AngleXU=0 Radius=1.5
    g1: Circle CenterX=-19.5 CenterY=-219 CenterZ=0 NormalX=0 NormalY=0 NormalZ=1 AngleXU=0 Radius=1.5
    g2: LineSegment [constr] StartX=-19.5 StartY=-179 StartZ=0 EndX=-19.5 EndY=-222 EndZ=0
    g3: GeomPoint X=-19.5 Y=-200.5 Z=0
    g4: Circle CenterX=19.5 CenterY=-182 CenterZ=0 NormalX=0 NormalY=0 NormalZ=1 AngleXU=0 Radius=1.5
    g5: Circle CenterX=19.5 CenterY=-219 CenterZ=0 NormalX=0 NormalY=0 NormalZ=1 AngleXU=0 Radius=1.5
  constraints (12):
    c: Diameter(g0) = 3
    c: Diameter(g1) = 3
    c: Symmetric(g-3,g-3,g2)
    c: Symmetric(g-8,g-8,g2)
    c: PointOnObject(g0,g2)
    c: Symmetric(g2,g2,g3)
    c: Symmetric(g0,g1,g3)
    c: Distance(g0,g-3) = 3
    c: Equal(g0,g4)
    c: Symmetric(g0,g4,g-2)
    c: Equal(g5,g1)
    c: Symmetric(g1,g5,g-2)
FEATURE [PartDesign::Pocket] Pocket007
  BaseFeature = -> Pocket006
  Direction = (0,0,-1)
  Length = 27
  Length2 = 5
  Profile = -> Sketch012
  ReferenceAxis = -> Sketch012 [N_Axis]
  Refine = true
  Suppressed = false
  Type = 0
FEATURE [Sketcher::SketchObject] Sketch013
  ArcFitTolerance = 1e-06
  AttachmentSupport = -> [Pocket007]
  ExternalGeometry = -> [Sketch004]
  FullyConstrained = true
  MakeInternals = false
  MapMode = 5
  Placement = pos=(0,0,8) rot=(0,0,1;0rad)
  sketch-geometry (4):
    g0: LineSegment StartX=16 StartY=-179 StartZ=0 EndX=-16 EndY=-179 EndZ=0
    g1: LineSegment StartX=-16 StartY=-179 StartZ=0 EndX=-16 EndY=-209 EndZ=0
    g2: LineSegment StartX=-16 StartY=-209 StartZ=0 EndX=16 EndY=-209 EndZ=0
    g3: LineSegment StartX=16 StartY=-209 StartZ=0 EndX=16 EndY=-179 EndZ=0
  constraints (10):
    c: Coincident(g0,g1)
    c: Coincident(g1,g2)
    c: Coincident(g2,g3)
    c: Coincident(g3,g0)
    c: Horizontal(g0)
    c: Horizontal(g2)
    c: Vertical(g1)
    c: Vertical(g3)
    c: Coincident(g0,g-4)
    c: Coincident(g1,g-3)
FEATURE [PartDesign::Pocket] Pocket008
  BaseFeature = -> Pocket007
  Direction = (0,0,-1)
  Length = 0
  Length2 = 5
  Profile = -> Sketch013
  ReferenceAxis = -> Sketch013 [N_Axis]
  Refine = true
  Suppressed = false
  Type = 3
  UpToFace = -> Pocket007 [Face4]
FEATURE [Sketcher::SketchObject] Sketch014
  ArcFitTolerance = 1e-06
  AttachmentSupport = -> [Pocket008]
  ExternalGeometry = -> [Pocket008]
  FullyConstrained = true
  MakeInternals = false
  MapMode = 5
  Placement = pos=(0,0,8) rot=(0,0,1;0rad)
  sketch-geometry (17):
    g0: LineSegment StartX=-39 StartY=-90.5 StartZ=0 EndX=-39 EndY=-48.5 EndZ=0
    g1: LineSegment StartX=39 StartY=-48.5 StartZ=0 EndX=39 EndY=-90.5 EndZ=0
    g2: GeomPoint [constr] X=0 Y=-69.5 Z=0
    g3: Circle CenterX=-22.5 CenterY=-94 CenterZ=0 NormalX=0 NormalY=0 NormalZ=1 AngleXU=0 Radius=1.5
    g4: Circle CenterX=35.5 CenterY=-94 CenterZ=0 NormalX=0 NormalY=0 NormalZ=1 AngleXU=0 Radius=1.5
    g5: LineSegment [constr] StartX=-22.5 StartY=-94 StartZ=0 EndX=35.5 EndY=-94 EndZ=0
    g6: Circle CenterX=-22.5 CenterY=-45 CenterZ=0 NormalX=0 NormalY=0 NormalZ=1 AngleXU=0 Radius=1.5
    g7: Circle CenterX=35.5 CenterY=-45 CenterZ=0 NormalX=0 NormalY=0 NormalZ=1 AngleXU=0 Radius=1.5
    g8: LineSegment [constr] StartX=-22.5 StartY=-94 StartZ=0 EndX=-22.5 EndY=-45 EndZ=0
    g9: LineSegment [constr] StartX=-22.5 StartY=-45 StartZ=0 EndX=35.5 EndY=-45 EndZ=0
    g10: LineSegment [constr] StartX=35.5 StartY=-94 StartZ=0 EndX=35.5 EndY=-45 EndZ=0
    g11: LineSegment StartX=-39 StartY=-90.5 StartZ=0 EndX=-15.5 EndY=-90.5 EndZ=0
    g12: LineSegment StartX=-15.5 StartY=-90.5 StartZ=0 EndX=-15.5 EndY=-97.5 EndZ=0
    g13: LineSegment StartX=-15.5 StartY=-97.5 StartZ=0 EndX=5 EndY=-97.5 EndZ=0
    g14: LineSegment StartX=5 StartY=-97.5 StartZ=0 EndX=5 EndY=-90.5 EndZ=0
    g15: LineSegment StartX=5 StartY=-90.5 StartZ=0 EndX=39 EndY=-90.5 EndZ=0
    g16: LineSegment StartX=-39 StartY=-48.5 StartZ=0 EndX=39 EndY=-48.5 EndZ=0
  constraints (45):
    c: Vertical(g0)
    c: Vertical(g1)
    c: Symmetric(g1,g0,g2)
    c: PointOnObject(g2,g-2)
    c: Distance(g0) = 42
    c: Equal(g0,g1)
    c: Diameter(g3) = 3
    c: DistanceY(g3,g0) = 3.5
    c: Equal(g3,g4)
    c: DistanceX(g3,g4) = 58
    c: Coincident(g5,g3)
    c: Coincident(g5,g4)
    c: Horizontal(g5)
    c: Equal(g3,g6)
    c: Equal(g6,g7)
    c: Coincident(g8,g3)
    c: Coincident(g8,g6)
    c: Vertical(g8)
    c: DistanceY(g3,g6) = 49
    c: Coincident(g9,g6)
    c: Coincident(g9,g7)
    c: Horizontal(g9)
    c: Coincident(g10,g4)
    c: Coincident(g10,g7)
    c: Vertical(g10)
    c: Distance(g6,g-3) = 4
    c: Coincident(g11,g0)
    c: Horizontal(g11)
    c: Coincident(g12,g11)
    c: Vertical(g12)
    c: Coincident(g13,g12)
    c: Horizontal(g13)
    c: Coincident(g14,g13)
    c: Vertical(g14)
    c: Coincident(g15,g14)
    c: Coincident(g15,g1)
    c: Horizontal(g15)
    c: DistanceX(g13,g13) = 20.5
    c: Coincident(g16,g0)
    c: Coincident(g16,g1)
    c: Horizontal(g16)
    c: DistanceX(g15,g15) = 34
    c: DistanceY(g12,g12) = 7
    c: DistanceX(g16,g16) = 78
    c: Distance(g0,g8) = 16.5
FEATURE [PartDesign::Pocket] Pocket009
  BaseFeature = -> Pocket008
  Direction = (0,0,-1)
  Length = 0
  Length2 = 5
  Profile = -> Sketch014
  ReferenceAxis = -> Sketch014 [N_Axis]
  Refine = true
  Suppressed = false
  Type = 3
  UpToFace = -> Pocket008 [Face4]
FEATURE [Sketcher::SketchObject] Sketch015
  ArcFitTolerance = 1e-06
  AttachmentSupport = -> [Pocket009]
  ExternalGeometry = -> [Pocket009]
  FullyConstrained = true
  MakeInternals = false
  MapMode = 5
  Placement = pos=(0,0,8) rot=(0,0,1;0rad)
  sketch-geometry (8):
    g0: LineSegment StartX=-25.5 StartY=-122 StartZ=0 EndX=-20.5 EndY=-122 EndZ=0
    g1: LineSegment StartX=-20.5 StartY=-122 StartZ=0 EndX=-20.5 EndY=-134 EndZ=0
    g2: LineSegment StartX=-20.5 StartY=-134 StartZ=0 EndX=-25.5 EndY=-134 EndZ=0
    g3: LineSegment StartX=-25.5 StartY=-134 StartZ=0 EndX=-25.5 EndY=-122 EndZ=0
    g4: LineSegment StartX=20.5 StartY=-122 StartZ=0 EndX=25.5 EndY=-122 EndZ=0
    g5: LineSegment StartX=25.5 StartY=-122 StartZ=0 EndX=25.5 EndY=-134 EndZ=0
    g6: LineSegment StartX=25.5 StartY=-134 StartZ=0 EndX=20.5 EndY=-134 EndZ=0
    g7: LineSegment StartX=20.5 StartY=-134 StartZ=0 EndX=20.5 EndY=-122 EndZ=0
  constraints (22):
    c: Coincident(g0,g1)
    c: Coincident(g1,g2)
    c: Coincident(g2,g3)
    c: Coincident(g3,g0)
    c: Horizontal(g0)
    c: Horizontal(g2)
    c: Vertical(g1)
    c: Vertical(g3)
    c: Distance(g3) = 12
    c: Distance(g0) = 5
    c: Coincident(g4,g5)
    c: Coincident(g5,g6)
    c: Coincident(g6,g7)
    c: Coincident(g7,g4)
    c: Horizontal(g4)
    c: Horizontal(g6)
    c: Vertical(g5)
    c: Vertical(g7)
    c: Symmetric(g0,g4,g-2)
    c: Symmetric(g1,g6,g-2)
    c: Distance(g2,g5) = 51
    c: DistanceY(g-3,g2) = 30
FEATURE [PartDesign::Pad] Pad005
  BaseFeature = -> Pocket009
  Direction = (0,0,1)
  Length = 19
  Length2 = 10
  Profile = -> Sketch015
  ReferenceAxis = -> Sketch015 [N_Axis]
  Refine = true
  Suppressed = false
  Type = 0
FEATURE [Sketcher::SketchObject] Sketch016
  ArcFitTolerance = 1e-06
  AttachmentSupport = -> [Pad005]
  ExternalGeometry = -> [Sketch015]
  FullyConstrained = true
  MakeInternals = false
  MapMode = 5
  Placement = pos=(0,0,27) rot=(0,0,1;0rad)
  sketch-geometry (4):
    g0: LineSegment StartX=25.5 StartY=-122 StartZ=0 EndX=-25.5 EndY=-122 EndZ=0
    g1: LineSegment StartX=-25.5 StartY=-122 StartZ=0 EndX=-25.5 EndY=-134 EndZ=0
    g2: LineSegment StartX=-25.5 StartY=-134 StartZ=0 EndX=25.5 EndY=-134 EndZ=0
    g3: LineSegment StartX=25.5 StartY=-134 StartZ=0 EndX=25.5 EndY=-122 EndZ=0
  constraints (10):
    c: Coincident(g0,g1)
    c: Coincident(g1,g2)
    c: Coincident(g2,g3)
    c: Coincident(g3,g0)
    c: Horizontal(g0)
    c: Horizontal(g2)
    c: Vertical(g1)
    c: Vertical(g3)
    c: Coincident(g0,g-4)
    c: Coincident(g1,g-3)
FEATURE [PartDesign::Pad] Pad006
  BaseFeature = -> Pad005
  Direction = (0,0,1)
  Length = 3
  Length2 = 10
  Profile = -> Sketch016
  ReferenceAxis = -> Sketch016 [N_Axis]
  Refine = true
  Suppressed = false
  Type = 0
FEATURE [Sketcher::SketchObject] Sketch017
  ArcFitTolerance = 1e-06
  AttachmentSupport = -> [Pad006]
  ExternalGeometry = -> [Pad006]
  FullyConstrained = true
  MakeInternals = false
  MapMode = 5
  Placement = pos=(0,0,8) rot=(0,0,1;0rad)
  sketch-geometry (5):
    g0: Circle CenterX=-40 CenterY=-114 CenterZ=0 NormalX=0 NormalY=0 NormalZ=1 AngleXU=0 Radius=1.3
    g1: Circle CenterX=40 CenterY=-114 CenterZ=0 NormalX=0 NormalY=0 NormalZ=1 AngleXU=0 Radius=1.3
    g2: Circle CenterX=-40 CenterY=-157 CenterZ=0 NormalX=0 NormalY=0 NormalZ=1 AngleXU=0 Radius=1.3
    g3: Circle CenterX=40 CenterY=-157 CenterZ=0 NormalX=0 NormalY=0 NormalZ=1 AngleXU=0 Radius=1.3
    g4: LineSegment [constr] StartX=-40 StartY=-114 StartZ=0 EndX=-40 EndY=-157 EndZ=0
  constraints (12):
    c: Diameter(g0) = 2.6
    c: Equal(g0,g1)
    c: Equal(g1,g2)
    c: Equal(g2,g3)
    c: Symmetric(g0,g1,g-2)
    c: Symmetric(g2,g3,g-2)
    c: Coincident(g4,g0)
    c: Coincident(g4,g2)
    c: Vertical(g4)
    c: DistanceX(g0,g1) = 80
    c: DistanceY(g2,g0) = 43
    c: DistanceY(g-3,g2) = 7
FEATURE [PartDesign::Pocket] Pocket010
  BaseFeature = -> Pad006
  Direction = (0,0,-1)
  Length = 0
  Length2 = 5
  Profile = -> Sketch017
  ReferenceAxis = -> Sketch017 [N_Axis]
  Refine = true
  Suppressed = false
  Type = 3
  UpToFace = -> Pad006 [Face6]
FEATURE [PartDesign::Fillet] Fillet
  Base = -> Pocket010 [Edge89,Edge87,Edge81,Edge85]
  BaseFeature = -> Pocket010
  Radius = 1
  Refine = true
  SupportTransform = false
  Suppressed = false
  UseAllEdges = false
FEATURE [PartDesign::Fillet] Fillet001
  Base = -> Fillet [Edge77,Edge111,Edge81,Edge125,Edge85,Edge129,Edge89,Edge134,Edge97,Edge103,Edge192,Edge179]
  BaseFeature = -> Fillet
  Radius = 3
  Refine = true
  SupportTransform = false
  Suppressed = false
  UseAllEdges = false
FEATURE [PartDesign::Body] Body  label="ChassisBody"
  AllowCompound = false
  Group = -> [Binder,Sketch,Pad,Sketch001,Pad001,Sketch002,Pad002,Sketch003,Pad003,Sketch004,Pad004,Sketch005,Pocket,Sketch006,Pocket001,Sketch007,Pocket002,Sketch008,Pocket003,Sketch009,Pocket004,Sketch010,Pocket005,Sketch011,Pocket006,Sketch012,Pocket007,Sketch013,Pocket008,Sketch014,Pocket009,Sketch015,Pad005,Sketch016,Pad006,Sketch017,Pocket010,Fillet,Fillet001]
  Origin = -> Origin001
  Tip = -> Fillet001
FEATURE [App::Part] Part  label="ChassisPart"
  Group = -> [Body]
  Origin = -> Origin
---- part ../Parts/FrontCover.FCStd = doc fcstd_34d13ded4ae3 ----
FCSTD DOCUMENT  (FreeCAD 1.0R39319 (Git))
Label: FrontCover
License: All rights reserved
LicenseURL: https://en.wikipedia.org/wiki/All_rights_reserved
objects: Sketcher::SketchObject×5, PartDesign::Pad×3, PartDesign::SubShapeBinder×2, PartDesign::Pocket×2, PartDesign::Chamfer×1, PartDesign::Body×1, App::Part×1
note: 31 computed .brp shape members not serialized (recipe doc carries the construction recipe); baked Part::Feature solids carry a one-line shape summary decoded from their .brp
EXTERNAL_REF file=../Models/SteeringAckermannModel.FCStd obj=Part
EXTERNAL_REF file=Chassis.FCStd obj=Part

FEATURE [PartDesign::SubShapeBinder] Binder  label="SteeringAckermannModel"
  BindCopyOnChange = 0
  BindMode = 0
  ClaimChildren = false
  Context = -> Part [Body.Binder.]
  Fuse = false
  MakeFace = true
  OffsetFill = false
  OffsetIntersection = false
  OffsetJoinType = 0
  OffsetOpenResult = false
  PartialLoad = false
  Refine = true
  Relative = true
  Support = -> [<external ../Models/SteeringAckermannModel.FCStd>#Part[Sketch001.]]
  _Version = 2
FEATURE [PartDesign::SubShapeBinder] Binder001  label="ChassisSketch002"
  BindCopyOnChange = 0
  BindMode = 0
  ClaimChildren = false
  Context = -> Part [Body.Binder001.]
  Fuse = false
  MakeFace = true
  OffsetFill = false
  OffsetIntersection = false
  OffsetJoinType = 0
  OffsetOpenResult = false
  PartialLoad = false
  Refine = true
  Relative = true
  Support = -> [<external Chassis.FCStd>#Part[Body.Sketch002.]]
  _Version = 2
FEATURE [Sketcher::SketchObject] Sketch
  ArcFitTolerance = 1e-06
  AttachmentSupport = -> [XY_Plane001]
  ExternalGeometry = -> [Binder001,Binder]
  FullyConstrained = true
  MakeInternals = false
  MapMode = 5
  sketch-geometry (27):
    g0: LineSegment StartX=-11.3 StartY=-4 StartZ=0 EndX=-26 EndY=-4 EndZ=0
    g1: LineSegment StartX=-26 StartY=-4 StartZ=0 EndX=-34 EndY=-4 EndZ=0
    g2: LineSegment StartX=-34 StartY=4 StartZ=0 EndX=-26 EndY=4 EndZ=0
    g3: LineSegment StartX=-26 StartY=4 StartZ=0 EndX=-10 EndY=22 EndZ=0
    g4: ArcOfCircle CenterX=-34 CenterY=-2e-16 CenterZ=0 NormalX=0 NormalY=0 NormalZ=1 AngleXU=0 Radius=4 StartAngle=1.5708 EndAngle=4.71239
    g5: LineSegment StartX=11.3 StartY=-4 StartZ=0 EndX=26 EndY=-4 EndZ=0
    g6: LineSegment StartX=26 StartY=4 StartZ=0 EndX=10 EndY=22 EndZ=0
    g7: LineSegment StartX=26 StartY=-4 StartZ=0 EndX=34 EndY=-4 EndZ=0
    g8: LineSegment StartX=26 StartY=4 StartZ=0 EndX=34 EndY=4 EndZ=0
    g9: ArcOfCircle CenterX=34 CenterY=0 CenterZ=0 NormalX=0 NormalY=0 NormalZ=1 AngleXU=0 Radius=4 StartAngle=4.71239 EndAngle=7.85398
    g10: LineSegment StartX=-10 StartY=22 StartZ=0 EndX=10 EndY=22 EndZ=0
    g11: LineSegment StartX=-11.3 StartY=-4 StartZ=0 EndX=-6 EndY=-23.75 EndZ=0
    g12: LineSegment StartX=-6 StartY=-23.75 StartZ=0 EndX=6 EndY=-23.75 EndZ=0
    g13: LineSegment StartX=6 StartY=-23.75 StartZ=0 EndX=11.3 EndY=-4 EndZ=0
    g14: LineSegment StartX=-4.35 StartY=0.65 StartZ=0 EndX=-4.35 EndY=-19.75 EndZ=0
    g15: LineSegment StartX=-4.35 StartY=-19.75 StartZ=0 EndX=4.35 EndY=-19.75 EndZ=0
    g16: LineSegment StartX=4.35 StartY=-19.75 StartZ=0 EndX=4.35 EndY=0.65 EndZ=0
    g17: LineSegment StartX=4.35 StartY=0.65 StartZ=0 EndX=-4.35 EndY=0.65 EndZ=0
    g18: GeomPoint X=4e-16 Y=-9.55 Z=0
    g19: Circle CenterX=0 CenterY=2.25 CenterZ=0 NormalX=0 NormalY=0 NormalZ=1 AngleXU=0 Radius=0.86
    g20: Circle CenterX=-7.473e-13 CenterY=-21.35 CenterZ=0 NormalX=0 NormalY=0 NormalZ=1 AngleXU=0 Radius=0.86
    g21: Circle CenterX=-34 CenterY=-2e-16 CenterZ=0 NormalX=0 NormalY=0 NormalZ=1 AngleXU=0 Radius=1.5
    g22: Circle CenterX=34 CenterY=0 CenterZ=0 NormalX=0 NormalY=0 NormalZ=1 AngleXU=0 Radius=1.5
    g23: Circle CenterX=-22 CenterY=0 CenterZ=0 NormalX=0 NormalY=0 NormalZ=1 AngleXU=0 Radius=1.65
    g24: Circle CenterX=-11.3195 CenterY=16 CenterZ=0 NormalX=0 NormalY=0 NormalZ=1 AngleXU=0 Radius=1.65
    g25: Circle CenterX=11.3195 CenterY=16 CenterZ=0 NormalX=0 NormalY=0 NormalZ=1 AngleXU=0 Radius=1.65
    g26: Circle CenterX=22 CenterY=0 CenterZ=0 NormalX=0 NormalY=0 NormalZ=1 AngleXU=0 Radius=1.65
  constraints (58):
    c: Coincident(g0,g-3)
    c: Coincident(g0,g-4)
    c: Coincident(g1,g0)
    c: Coincident(g2,g-7)
    c: Coincident(g3,g2)
    c: Coincident(g3,g-8)
    c: Tangent(g1,g4) = 1.5708
    c: Tangent(g2,g4) = 1.5708
    c: Coincident(g1,g-5)
    c: Horizontal(g2)
    c: Coincident(g5,g-12)
    c: Coincident(g5,g-13)
    c: Coincident(g6,g-16)
    c: Coincident(g6,g-17)
    c: Coincident(g7,g5)
    c: Coincident(g8,g6)
    c: Tangent(g7,g9) = -1.5708
    c: Tangent(g9,g8) = 1.5708
    c: Horizontal(g8)
    c: Coincident(g7,g-14)
    c: Coincident(g10,g3)
    c: Coincident(g10,g6)
    c: Coincident(g11,g0)
    c: Coincident(g12,g11)
    c: Coincident(g13,g12)
    c: Coincident(g13,g5)
    c: Symmetric(g11,g12,g-2)
    c: DistanceX(g12,g12) = 12
    c: Coincident(g14,g15)
    c: Coincident(g15,g16)
    c: Coincident(g16,g17)
    c: Coincident(g17,g14)
    c: Vertical(g14)
    c: Vertical(g16)
    c: Horizontal(g17)
    c: Symmetric(g14,g15,g-2)
    c: DistanceX(g15,g15) = 8.7
    c: DistanceY(g14,g14) = 20.4
    c: Distance(g-21,g17) = 4.65
    c: Distance(g12,g15) = 4
    c: Symmetric(g14,g16,g18)
    c: Diameter(g19) = 1.72
    c: PointOnObject(g19,g-2)
    c: Equal(g19,g20)
    c: Symmetric(g19,g20,g18)
    c: Distance(g19,g17) = 1.6
    c: Coincident(g21,g4)
    c: Equal(g21,g-9)
    c: Coincident(g22,g9)
    c: Equal(g22,g-18)
    c: Coincident(g23,g-10)
    c: Coincident(g24,g-11)
    c: Coincident(g25,g-20)
    c: Coincident(g26,g-19)
    c: Equal(g23,g26)
    c: Equal(g24,g25)
    c: Diameter(g23) = 3.3
    c: Diameter(g24) = 3.3
FEATURE [PartDesign::Pad] Pad
  Direction = (0,0,1)
  Length = 3
  Length2 = 10
  Profile = -> Sketch
  ReferenceAxis = -> Sketch [N_Axis]
  Refine = true
  Suppressed = false
  Type = 0
FEATURE [Sketcher::SketchObject] Sketch001
  ArcFitTolerance = 1e-06
  AttachmentSupport = -> [Pad]
  ExternalGeometry = -> [Sketch]
  FullyConstrained = true
  MakeInternals = false
  MapMode = 5
  Placement = pos=(0,0,3) rot=(0,0,1;0rad)
  sketch-geometry (13):
    g0: LineSegment StartX=-4.35 StartY=-19.75 StartZ=0 EndX=4.35 EndY=-19.75 EndZ=0
    g1: LineSegment StartX=4.35 StartY=-19.75 StartZ=0 EndX=4.35 EndY=0.65 EndZ=0
    g2: LineSegment StartX=4.35 StartY=0.65 StartZ=0 EndX=-4.35 EndY=0.65 EndZ=0
    g3: LineSegment StartX=-4.35 StartY=0.65 StartZ=0 EndX=-4.35 EndY=-19.75 EndZ=0
    g4: Circle CenterX=0 CenterY=-21.35 CenterZ=0 NormalX=0 NormalY=0 NormalZ=1 AngleXU=0 Radius=0.86
    g5: Circle CenterX=0 CenterY=2.25 CenterZ=0 NormalX=0 NormalY=0 NormalZ=1 AngleXU=0 Radius=0.86
    g6: LineSegment StartX=-6 StartY=-23.75 StartZ=0 EndX=6 EndY=-23.75 EndZ=0
    g7: LineSegment [constr] StartX=-9.81063 StartY=-9.55 StartZ=0 EndX=9.81063 EndY=-9.55 EndZ=0
    g8: LineSegment StartX=-6 StartY=-23.75 StartZ=0 EndX=-9.81063 EndY=-9.55 EndZ=0
    g9: LineSegment StartX=6 StartY=-23.75 StartZ=0 EndX=9.81063 EndY=-9.55 EndZ=0
    g10: LineSegment StartX=-6 StartY=4.65 StartZ=0 EndX=-9.81063 EndY=-9.55 EndZ=0
    g11: LineSegment StartX=-6 StartY=4.65 StartZ=0 EndX=6 EndY=4.65 EndZ=0
    g12: LineSegment StartX=6 StartY=4.65 StartZ=0 EndX=9.81063 EndY=-9.55 EndZ=0
  constraints (27):
    c: Coincident(g0,g-10)
    c: Coincident(g0,g-11)
    c: Coincident(g1,g0)
    c: Coincident(g1,g-12)
    c: Coincident(g2,g1)
    c: Coincident(g2,g-12)
    c: Coincident(g3,g2)
    c: Coincident(g3,g0)
    c: Coincident(g4,g-7)
    c: Equal(g4,g-7)
    c: Coincident(g5,g-8)
    c: Equal(g5,g-8)
    c: Coincident(g6,g-5)
    c: Coincident(g6,g-6)
    c: Horizontal(g7)
    c: Symmetric(g7,g7,g-3)
    c: PointOnObject(g7,g-4)
    c: Coincident(g8,g6)
    c: Coincident(g8,g7)
    c: Coincident(g9,g6)
    c: Coincident(g9,g7)
    c: Coincident(g10,g11)
    c: Coincident(g12,g11)
    c: Symmetric(g6,g10,g7)
    c: Symmetric(g6,g11,g7)
    c: Coincident(g10,g7)
    c: Coincident(g12,g7)
FEATURE [PartDesign::Pad] Pad001
  BaseFeature = -> Pad
  Direction = (0,0,1)
  Length = 5.5
  Length2 = 10
  Profile = -> Sketch001
  ReferenceAxis = -> Sketch001 [N_Axis]
  Refine = true
  Suppressed = false
  Type = 0
FEATURE [Sketcher::SketchObject] Sketch002
  ArcFitTolerance = 1e-06
  AttachmentSupport = -> [Pad001]
  ExternalGeometry = -> [Sketch001]
  FullyConstrained = true
  MakeInternals = false
  MapMode = 5
  Placement = pos=(0,0,3) rot=(0,0,1;0rad)
  sketch-geometry (8):
    g0: LineSegment StartX=-12 StartY=6.65 StartZ=0 EndX=-12 EndY=-1.35 EndZ=0
    g1: LineSegment StartX=-12 StartY=-1.35 StartZ=0 EndX=-13.5 EndY=-1.35 EndZ=0
    g2: LineSegment StartX=-13.5 StartY=-1.35 StartZ=0 EndX=-13.5 EndY=9.65 EndZ=0
    g3: LineSegment StartX=-12 StartY=6.65 StartZ=0 EndX=12 EndY=6.65 EndZ=0
    g4: LineSegment StartX=-13.5 StartY=9.65 StartZ=0 EndX=13.5 EndY=9.65 EndZ=0
    g5: LineSegment StartX=12 StartY=6.65 StartZ=0 EndX=12 EndY=-1.35 EndZ=0
    g6: LineSegment StartX=12 StartY=-1.35 StartZ=0 EndX=13.5 EndY=-1.35 EndZ=0
    g7: LineSegment StartX=13.5 StartY=-1.35 StartZ=0 EndX=13.5 EndY=9.65 EndZ=0
  constraints (20):
    c: Vertical(g0)
    c: Coincident(g1,g0)
    c: Horizontal(g1)
    c: Coincident(g2,g1)
    c: Vertical(g2)
    c: Coincident(g3,g0)
    c: Coincident(g4,g2)
    c: Symmetric(g2,g4,g-2)
    c: Symmetric(g0,g3,g-2)
    c: Coincident(g5,g3)
    c: Coincident(g6,g5)
    c: Coincident(g7,g6)
    c: Coincident(g7,g4)
    c: Symmetric(g1,g6,g-2)
    c: Symmetric(g0,g5,g-2)
    c: DistanceX(g1,g1) = 1.5
    c: DistanceY(g0,g0) = 8
    c: Distance(g4,g3) = 3
    c: Distance(g-3,g3) = 2
    c: DistanceX(g4,g4) = 27
FEATURE [PartDesign::Pad] Pad002
  BaseFeature = -> Pad001
  Direction = (0,0,1)
  Length = 36
  Length2 = 10
  Profile = -> Sketch002
  ReferenceAxis = -> Sketch002 [N_Axis]
  Refine = true
  Suppressed = false
  Type = 0
FEATURE [PartDesign::Chamfer] Chamfer
  Angle = 15
  Base = -> Pad002 [Edge107,Edge99]
  BaseFeature = -> Pad002
  ChamferType = 2
  FlipDirection = false
  Refine = true
  Size = 29.85
  Size2 = 1
  SupportTransform = false
  Suppressed = false
  UseAllEdges = false
FEATURE [Sketcher::SketchObject] Sketch003
  ArcFitTolerance = 1e-06
  AttachmentSupport = -> [Chamfer]
  ExternalGeometry = -> [Chamfer]
  FullyConstrained = true
  MakeInternals = false
  MapMode = 5
  Placement = pos=(0,9.65,0) rot=(0,0.707107,0.707107;3.14159rad)
  sketch-geometry (14):
    g0: LineSegment [constr] StartX=-10.25 StartY=6 StartZ=0 EndX=10.25 EndY=6 EndZ=0
    g1: LineSegment [constr] StartX=10.25 StartY=6 StartZ=0 EndX=10.25 EndY=19.5 EndZ=0
    g2: LineSegment [constr] StartX=10.25 StartY=19.5 StartZ=0 EndX=-10.25 EndY=19.5 EndZ=0
    g3: LineSegment [constr] StartX=-10.25 StartY=19.5 StartZ=0 EndX=-10.25 EndY=6 EndZ=0
    g4: GeomPoint [constr] X=0 Y=12.75 Z=0
    g5: Circle CenterX=-10.25 CenterY=6 CenterZ=0 NormalX=0 NormalY=0 NormalZ=1 AngleXU=0 Radius=1.05
    g6: Circle CenterX=-10.25 CenterY=19.5 CenterZ=0 NormalX=0 NormalY=0 NormalZ=1 AngleXU=0 Radius=1.05
    g7: Circle CenterX=10.25 CenterY=6 CenterZ=0 NormalX=0 NormalY=0 NormalZ=1 AngleXU=0 Radius=1.05
    g8: Circle CenterX=10.25 CenterY=19.5 CenterZ=0 NormalX=0 NormalY=0 NormalZ=1 AngleXU=0 Radius=1.05
    g9: LineSegment StartX=-10 StartY=33.5 StartZ=0 EndX=10 EndY=33.5 EndZ=0
    g10: LineSegment StartX=10 StartY=33.5 StartZ=0 EndX=10 EndY=36.5 EndZ=0
    g11: LineSegment StartX=10 StartY=36.5 StartZ=0 EndX=-10 EndY=36.5 EndZ=0
    g12: LineSegment StartX=-10 StartY=36.5 StartZ=0 EndX=-10 EndY=33.5 EndZ=0
    g13: GeomPoint [constr] X=0 Y=35 Z=0
  constraints (34):
    c: Coincident(g0,g1)
    c: Coincident(g1,g2)
    c: Coincident(g2,g3)
    c: Coincident(g3,g0)
    c: Horizontal(g0)
    c: Horizontal(g2)
    c: Vertical(g1)
    c: Vertical(g3)
    c: Symmetric(g2,g0,g4)
    c: PointOnObject(g4,g-2)
    c: Diameter(g5) = 2.1
    c: Coincident(g6,g2)
    c: Coincident(g7,g0)
    c: Coincident(g8,g1)
    c: Equal(g5,g6)
    c: Equal(g5,g7)
    c: Equal(g6,g8)
    c: DistanceX(g0,g0) = 20.5
    c: DistanceY(g3,g3) = 13.5
    c: Distance(g0,g-3) = 3
    c: Coincident(g5,g0)
    c: Coincident(g9,g10)
    c: Coincident(g10,g11)
    c: Coincident(g11,g12)
    c: Coincident(g12,g9)
    c: Horizontal(g9)
    c: Horizontal(g11)
    c: Vertical(g10)
    c: Vertical(g12)
    c: Symmetric(g11,g9,g13)
    c: PointOnObject(g13,g-2)
    c: DistanceX(g9,g9) = 20
    c: DistanceY(g12,g12) = 3
    c: DistanceY(g2,g9) = 14
FEATURE [PartDesign::Pocket] Pocket
  BaseFeature = -> Chamfer
  Direction = (0,-1,2e-16)
  Length = 0
  Length2 = 5
  Profile = -> Sketch003
  ReferenceAxis = -> Sketch003 [N_Axis]
  Refine = true
  Suppressed = false
  Type = 3
  UpToFace = -> Chamfer [Face6]
FEATURE [Sketcher::SketchObject] Sketch004
  ArcFitTolerance = 1e-06
  AttachmentSupport = -> [Pocket]
  ExternalGeometry = -> [Binder001,Sketch,Sketch001]
  FullyConstrained = true
  MakeInternals = false
  MapMode = 5
  Placement = pos=(0,0,0) rot=(1,0,0;3.14159rad)
  sketch-geometry (8):
    g0: LineSegment StartX=-8 StartY=2.75 StartZ=0 EndX=-11.3 EndY=4 EndZ=0
    g1: LineSegment StartX=-11.3 StartY=4 StartZ=0 EndX=-6 EndY=23.75 EndZ=0
    g2: LineSegment StartX=-6 StartY=23.75 StartZ=0 EndX=6 EndY=23.75 EndZ=0
    g3: LineSegment StartX=6 StartY=23.75 StartZ=0 EndX=11.3 EndY=4 EndZ=0
    g4: LineSegment StartX=11.3 StartY=4 StartZ=0 EndX=8 EndY=2.75 EndZ=0
    g5: LineSegment StartX=-8 StartY=2.75 StartZ=0 EndX=-6 EndY=-4.65 EndZ=0
    g6: LineSegment StartX=-6 StartY=-4.65 StartZ=0 EndX=6 EndY=-4.65 EndZ=0
    g7: LineSegment StartX=6 StartY=-4.65 StartZ=0 EndX=8 EndY=2.75 EndZ=0
  constraints (16):
    c: Coincident(g0,g-7)
    c: Coincident(g1,g0)
    c: Coincident(g1,g-8)
    c: Coincident(g2,g1)
    c: Coincident(g2,g-9)
    c: Coincident(g3,g2)
    c: Coincident(g3,g-9)
    c: Coincident(g4,g3)
    c: Coincident(g4,g-6)
    c: Coincident(g0,g-4)
    c: Coincident(g5,g0)
    c: Coincident(g5,g-11)
    c: Coincident(g6,g5)
    c: Coincident(g6,g-12)
    c: Coincident(g7,g6)
    c: Coincident(g7,g4)
FEATURE [PartDesign::Pocket] Pocket001
  BaseFeature = -> Pocket
  Direction = (0,0,1)
  Length = 1
  Length2 = 5
  Profile = -> Sketch004
  ReferenceAxis = -> Sketch004 [N_Axis]
  Refine = true
  Suppressed = false
  Type = 0
FEATURE [PartDesign::Body] Body  label="FrontCoverBody"
  AllowCompound = false
  Group = -> [Binder,Binder001,Sketch,Pad,Sketch001,Pad001,Sketch002,Pad002,Chamfer,Sketch003,Pocket,Sketch004,Pocket001]
  Origin = -> Origin001
  Tip = -> Pocket001
FEATURE [App::Part] Part  label="FrontCoverPart"
  Group = -> [Body]
  Origin = -> Origin
---- part ../Parts/FrontWheelAxle/FrontWheelAxleLeft.FCStd = doc fcstd_68c86e5070d7 ----
FCSTD DOCUMENT  (FreeCAD 1.0R39285 (Git))
Label: FrontWheelAxleLeft
License: All rights reserved
LicenseURL: https://en.wikipedia.org/wiki/All_rights_reserved
objects: Sketcher::SketchObject×5, PartDesign::Pad×4, PartDesign::Chamfer×3, PartDesign::Pocket×1, PartDesign::Body×1, App::Part×1
note: 35 computed .brp shape members not serialized (recipe doc carries the construction recipe); baked Part::Feature solids carry a one-line shape summary decoded from their .brp

FEATURE [Sketcher::SketchObject] Sketch
  ArcFitTolerance = 1e-06
  AttachmentSupport = -> [YZ_Plane001]
  FullyConstrained = true
  MakeInternals = false
  MapMode = 5
  Placement = pos=(0,0,0) rot=(0.57735,0.57735,0.57735;2.0944rad)
  sketch-geometry (4):
    g0: ArcOfCircle CenterX=0 CenterY=0 CenterZ=0 NormalX=0 NormalY=0 NormalZ=1 AngleXU=0 Radius=4.525 StartAngle=2.80371 EndAngle=3.47948
    g1: ArcOfCircle CenterX=0 CenterY=0 CenterZ=0 NormalX=0 NormalY=0 NormalZ=1 AngleXU=0 Radius=4.525 StartAngle=5.9453 EndAngle=6.62107
    g2: LineSegment StartX=-4.26915 StartY=1.5 StartZ=0 EndX=4.26915 EndY=1.5 EndZ=0
    g3: LineSegment StartX=4.26915 StartY=-1.5 StartZ=0 EndX=-4.26915 EndY=-1.5 EndZ=0
  constraints (12):
    c: Coincident(g0,g-1)
    c: Coincident(g1,g0)
    c: Coincident(g2,g0)
    c: Coincident(g2,g1)
    c: Horizontal(g2)
    c: Coincident(g3,g1)
    c: Coincident(g3,g0)
    c: Horizontal(g3)
    c: Equal(g0,g1)
    c: Equal(g3,g2)
    c: Diameter(g0) = 9.05
    c: Distance(g2,g3) = 3
FEATURE [PartDesign::Pad] Pad
  Direction = (1,0,0)
  Length = 11
  Length2 = 10
  Placement = pos=(0,0,0) rot=(1,1,1;2.0944rad)
  Profile = -> Sketch
  ReferenceAxis = -> Sketch [N_Axis]
  Refine = true
  Reversed = true
  Suppressed = false
  Type = 0
FEATURE [Sketcher::SketchObject] Sketch001
  ArcFitTolerance = 1e-06
  AttachmentSupport = -> [Pad]
  ExternalGeometry = -> [Sketch]
  FullyConstrained = true
  MakeInternals = false
  MapMode = 5
  Placement = pos=(-11,0,0) rot=(0.57735,0.57735,-0.57735;4.18879rad)
  sketch-geometry (1):
    g0: Circle CenterX=0 CenterY=0 CenterZ=0 NormalX=0 NormalY=0 NormalZ=1 AngleXU=0 Radius=4.525
  constraints (2):
    c: Coincident(g0,g-1)
    c: Equal(g0,g-3)
FEATURE [PartDesign::Pad] Pad001
  BaseFeature = -> Pad
  Direction = (-1,0,0)
  Length = 3
  Length2 = 10
  Placement = pos=(0,0,0) rot=(1,1,1;2.0944rad)
  Profile = -> Sketch001
  ReferenceAxis = -> Sketch001 [N_Axis]
  Refine = true
  Suppressed = false
  Type = 0
FEATURE [Sketcher::SketchObject] Sketch002
  ArcFitTolerance = 1e-06
  AttachmentSupport = -> [Pad001]
  FullyConstrained = true
  MakeInternals = false
  MapMode = 5
  Placement = pos=(-14,0,0) rot=(0.57735,0.57735,-0.57735;4.18879rad)
  sketch-geometry (1):
    g0: Circle CenterX=0 CenterY=0 CenterZ=0 NormalX=0 NormalY=0 NormalZ=1 AngleXU=0 Radius=6.5
  constraints (2):
    c: Coincident(g0,g-1)
    c: Diameter(g0) = 13
FEATURE [PartDesign::Pad] Pad002
  BaseFeature = -> Pad001
  Direction = (-1,0,0)
  Length = 2
  Length2 = 10
  Placement = pos=(0,0,0) rot=(1,1,1;2.0944rad)
  Profile = -> Sketch002
  ReferenceAxis = -> Sketch002 [N_Axis]
  Refine = true
  Suppressed = false
  Type = 0
FEATURE [Sketcher::SketchObject] Sketch003
  ArcFitTolerance = 1e-06
  AttachmentSupport = -> [Pad002]
  ExternalGeometry = -> [Sketch]
  FullyConstrained = true
  MakeInternals = false
  MapMode = 5
  Placement = pos=(-16,0,0) rot=(0.57735,0.57735,-0.57735;4.18879rad)
  sketch-geometry (1):
    g0: Circle CenterX=0 CenterY=0 CenterZ=0 NormalX=0 NormalY=0 NormalZ=1 AngleXU=0 Radius=4.525
  constraints (2):
    c: Coincident(g0,g-1)
    c: Equal(g0,g-3)
FEATURE [PartDesign::Pad] Pad003
  BaseFeature = -> Pad002
  Direction = (-1,0,0)
  Length = 10
  Length2 = 10
  Placement = pos=(0,0,0) rot=(1,1,1;2.0944rad)
  Profile = -> Sketch003
  ReferenceAxis = -> Sketch003 [N_Axis]
  Refine = true
  Suppressed = false
  Type = 0
FEATURE [Sketcher::SketchObject] Sketch004
  ArcFitTolerance = 1e-06
  AttachmentSupport = -> [Pad003]
  FullyConstrained = true
  MakeInternals = false
  MapMode = 5
  Placement = pos=(0,3e-16,1.5) rot=(0,0,-1;1.5708rad)
  sketch-geometry (2):
    g0: Circle CenterX=0 CenterY=-3 CenterZ=0 NormalX=0 NormalY=0 NormalZ=1 AngleXU=0 Radius=1.62
    g1: Circle CenterX=0 CenterY=-8 CenterZ=0 NormalX=0 NormalY=0 NormalZ=1 AngleXU=0 Radius=1.68
  constraints (6):
    c: Diameter(g0) = 3.24
    c: PointOnObject(g0,g-2)
    c: DistanceY(g0,g-1) = 3
    c: Diameter(g1) = 3.36
    c: PointOnObject(g1,g-2)
    c: DistanceY(g1,g0) = 5
FEATURE [PartDesign::Pocket] Pocket
  BaseFeature = -> Pad003
  Direction = (0,0,-1)
  Length = 0
  Length2 = 5
  Placement = pos=(0,0,0) rot=(1,1,1;2.0944rad)
  Profile = -> Sketch004
  ReferenceAxis = -> Sketch004 [N_Axis]
  Refine = true
  Suppressed = false
  Type = 3
  UpToFace = -> Pad003 [Face5]
FEATURE [PartDesign::Chamfer] Chamfer
  Angle = 45
  Base = -> Pocket [Edge27]
  BaseFeature = -> Pocket
  ChamferType = 1
  FlipDirection = false
  Placement = pos=(0,0,0) rot=(1,1,1;2.0944rad)
  Refine = true
  Size = 2
  Size2 = 1
  SupportTransform = false
  Suppressed = false
  UseAllEdges = false
FEATURE [PartDesign::Chamfer] Chamfer001
  Angle = 45
  Base = -> Chamfer [Edge10]
  BaseFeature = -> Chamfer
  ChamferType = 1
  FlipDirection = false
  Placement = pos=(0,0,0) rot=(1,1,1;2.0944rad)
  Refine = true
  Size = 9
  Size2 = 2.2
  SupportTransform = false
  Suppressed = false
  UseAllEdges = false
FEATURE [PartDesign::Chamfer] Chamfer002
  Angle = 45
  Base = -> Chamfer001 [Edge10,Edge7]
  BaseFeature = -> Chamfer001
  ChamferType = 1
  FlipDirection = false
  Placement = pos=(0,0,0) rot=(1,1,1;2.0944rad)
  Refine = true
  Size = 3
  Size2 = 2
  SupportTransform = false
  Suppressed = false
  UseAllEdges = false
FEATURE [PartDesign::Body] Body  label="FrontWheelAxleLeftBody"
  AllowCompound = false
  Group = -> [Sketch,Pad,Sketch001,Pad001,Sketch002,Pad002,Sketch003,Pad003,Sketch004,Pocket,Chamfer,Chamfer001,Chamfer002]
  Origin = -> Origin001
  Tip = -> Chamfer002
FEATURE [App::Part] Part  label="FrontWheelAxleLeftPart"
  Group = -> [Body]
  Origin = -> Origin
---- part ../Parts/FrontWheelAxle/FrontWheelAxleRight.FCStd = doc fcstd_31e5d270f517 ----
FCSTD DOCUMENT  (FreeCAD 1.0R39285 (Git))
Label: FrontWheelAxleRight
License: All rights reserved
LicenseURL: https://en.wikipedia.org/wiki/All_rights_reserved
objects: PartDesign::SubShapeBinder×1, Part::Mirroring×1, App::Part×1
note: 2 computed .brp shape members not serialized (recipe doc carries the construction recipe); baked Part::Feature solids carry a one-line shape summary decoded from their .brp
EXTERNAL_REF file=FrontWheelAxleLeft.FCStd obj=Part

FEATURE [PartDesign::SubShapeBinder] Binder  label="FrontWheelAxleLeftBody"
  BindCopyOnChange = 0
  BindMode = 0
  ClaimChildren = false
  Context = -> Part [Binder.]
  Fuse = false
  MakeFace = true
  OffsetFill = false
  OffsetIntersection = false
  OffsetJoinType = 0
  OffsetOpenResult = false
  PartialLoad = false
  Refine = true
  Relative = true
  Support = -> [<external FrontWheelAxleLeft.FCStd>#Part[Body.]]
  _Version = 2
FEATURE [Part::Mirroring] Part__Mirroring  label="FrontWheelAxleRightBody"
  Base = (0,0,0)
  Normal = (1,0,0)
  Source = -> Binder
FEATURE [App::Part] Part  label="FrontWheelAxleRightPart"
  Group = -> [Binder,Part__Mirroring]
  Origin = -> Origin
---- part ../Parts/FrontWheelStopper.FCStd = doc fcstd_769df6a6616b ----
FCSTD DOCUMENT  (FreeCAD 1.0R39109 (Git))
Label: FrontWheelStopper
License: All rights reserved
LicenseURL: https://en.wikipedia.org/wiki/All_rights_reserved
objects: Sketcher::SketchObject×2, PartDesign::Pad×2, PartDesign::Fillet×1, PartDesign::Body×1, App::Part×1
note: 14 computed .brp shape members not serialized (recipe doc carries the construction recipe); baked Part::Feature solids carry a one-line shape summary decoded from their .brp

FEATURE [Sketcher::SketchObject] Sketch
  ArcFitTolerance = 1e-06
  AttachmentSupport = -> [YZ_Plane001]
  FullyConstrained = true
  MakeInternals = false
  MapMode = 5
  Placement = pos=(0,0,0) rot=(0.57735,0.57735,0.57735;2.0944rad)
  sketch-geometry (12):
    g0: LineSegment [constr] StartX=0 StartY=10 StartZ=0 EndX=-8.66025 EndY=-5 EndZ=0
    g1: LineSegment [constr] StartX=-8.66025 StartY=-5 StartZ=0 EndX=8.66025 EndY=-5 EndZ=0
    g2: LineSegment [constr] StartX=8.66025 StartY=-5 StartZ=0 EndX=0 EndY=10 EndZ=0
    g3: Circle [constr] CenterX=0 CenterY=0 CenterZ=0 NormalX=0 NormalY=0 NormalZ=1 AngleXU=0 Radius=10
    g4: LineSegment StartX=0 StartY=20.2073 StartZ=0 EndX=-17.5 EndY=-10.1036 EndZ=0
    g5: LineSegment StartX=-17.5 StartY=-10.1036 StartZ=0 EndX=17.5 EndY=-10.1036 EndZ=0
    g6: LineSegment StartX=17.5 StartY=-10.1036 StartZ=0 EndX=0 EndY=20.2073 EndZ=0
    g7: Circle [constr] CenterX=0 CenterY=0 CenterZ=0 NormalX=0 NormalY=0 NormalZ=1 AngleXU=0 Radius=20.2073
    g8: Circle CenterX=0 CenterY=0 CenterZ=0 NormalX=0 NormalY=0 NormalZ=1 AngleXU=0 Radius=4.725
    g9: Circle CenterX=0 CenterY=10 CenterZ=0 NormalX=0 NormalY=0 NormalZ=1 AngleXU=0 Radius=1.5
    g10: Circle CenterX=-8.66025 CenterY=-5 CenterZ=0 NormalX=0 NormalY=0 NormalZ=1 AngleXU=0 Radius=1.5
    g11: Circle CenterX=8.66025 CenterY=-5 CenterZ=0 NormalX=0 NormalY=0 NormalZ=1 AngleXU=0 Radius=1.5
  constraints (30):
    c: Coincident(g0,g1)
    c: Coincident(g1,g2)
    c: Coincident(g2,g0)
    c: Equal(g0,g1)
    c: Equal(g0,g2)
    c: PointOnObject(g0,g3)
    c: PointOnObject(g1,g3)
    c: PointOnObject(g2,g3)
    c: Coincident(g3,g-1)
    c: PointOnObject(g2,g-2)
    c: DistanceY(g3,g0) = 10
    c: Coincident(g4,g5)
    c: Coincident(g5,g6)
    c: Coincident(g6,g4)
    c: Equal(g4,g5)
    c: Equal(g4,g6)
    c: PointOnObject(g4,g7)
    c: PointOnObject(g5,g7)
    c: PointOnObject(g6,g7)
    c: Coincident(g7,g3)
    c: PointOnObject(g6,g-2)
    c: DistanceX(g5,g5) = 35
    c: Diameter(g8) = 9.45
    c: Coincident(g8,g3)
    c: Diameter(g9) = 3
    c: Coincident(g9,g0)
    c: Coincident(g10,g0)
    c: Coincident(g11,g1)
    c: Diameter(g10) = 3
    c: Diameter(g11) = 3
FEATURE [PartDesign::Pad] Pad
  Direction = (1,0,0)
  Length = 2
  Length2 = 10
  Placement = pos=(0,0,0) rot=(1,1,1;2.0944rad)
  Profile = -> Sketch
  ReferenceAxis = -> Sketch [N_Axis]
  Refine = true
  Reversed = true
  Suppressed = false
  Type = 0
FEATURE [Sketcher::SketchObject] Sketch001
  ArcFitTolerance = 1e-06
  AttachmentSupport = -> [Pad]
  ExternalGeometry = -> [Sketch]
  FullyConstrained = true
  MakeInternals = false
  MapMode = 5
  Placement = pos=(-2,4e-16,-2e-16) rot=(0.57735,0.57735,-0.57735;4.18879rad)
  sketch-geometry (6):
    g0: Circle CenterX=-8.66025 CenterY=5 CenterZ=0 NormalX=0 NormalY=0 NormalZ=1 AngleXU=0 Radius=1.5
    g1: Circle CenterX=8.66025 CenterY=5 CenterZ=0 NormalX=0 NormalY=0 NormalZ=1 AngleXU=0 Radius=1.5
    g2: Circle CenterX=0 CenterY=-10 CenterZ=0 NormalX=0 NormalY=0 NormalZ=1 AngleXU=0 Radius=1.5
    g3: Circle CenterX=8.66025 CenterY=5 CenterZ=0 NormalX=0 NormalY=0 NormalZ=1 AngleXU=0 Radius=3
    g4: Circle CenterX=-8.66025 CenterY=5 CenterZ=0 NormalX=0 NormalY=0 NormalZ=1 AngleXU=0 Radius=3
    g5: Circle CenterX=0 CenterY=-10 CenterZ=0 NormalX=0 NormalY=0 NormalZ=1 AngleXU=0 Radius=3
  constraints (12):
    c: Coincident(g0,g-5)
    c: Coincident(g1,g-4)
    c: Coincident(g2,g-3)
    c: Equal(g1,g-4)
    c: Equal(g0,g-5)
    c: Equal(g2,g-3)
    c: Coincident(g3,g1)
    c: Coincident(g4,g0)
    c: Coincident(g5,g2)
    c: Diameter(g3) = 6
    c: Diameter(g4) = 6
    c: Diameter(g5) = 6
FEATURE [PartDesign::Pad] Pad001
  BaseFeature = -> Pad
  Direction = (-1,0,0)
  Length = 4
  Length2 = 10
  Placement = pos=(0,0,0) rot=(1,1,1;2.0944rad)
  Profile = -> Sketch001
  ReferenceAxis = -> Sketch001 [N_Axis]
  Refine = true
  Suppressed = false
  Type = 0
FEATURE [PartDesign::Fillet] Fillet
  Base = -> Pad001 [Edge1,Edge2,Edge5]
  BaseFeature = -> Pad001
  Placement = pos=(0,0,0) rot=(1,1,1;2.0944rad)
  Radius = 6
  Refine = true
  SupportTransform = false
  Suppressed = false
  UseAllEdges = false
FEATURE [PartDesign::Body] Body  label="FrontWheelStopperBody"
  AllowCompound = false
  Group = -> [Sketch,Pad,Sketch001,Pad001,Fillet]
  Origin = -> Origin001
  Tip = -> Fillet
FEATURE [App::Part] Part  label="FrontWheelStopperPart"
  Group = -> [Body]
  Origin = -> Origin
---- part ../Parts/LidarPlate.FCStd = doc fcstd_acf3c6f62157 ----
FCSTD DOCUMENT  (FreeCAD 1.0R39319 (Git))
Label: LidarPlate
License: All rights reserved
LicenseURL: https://en.wikipedia.org/wiki/All_rights_reserved
objects: Sketcher::SketchObject×2, PartDesign::Pad×2, PartDesign::SubShapeBinder×1, PartDesign::Fillet×1, PartDesign::Body×1, App::Part×1
note: 15 computed .brp shape members not serialized (recipe doc carries the construction recipe); baked Part::Feature solids carry a one-line shape summary decoded from their .brp
EXTERNAL_REF file=Chassis.FCStd obj=Part

FEATURE [PartDesign::SubShapeBinder] Binder
  BindCopyOnChange = 0
  BindMode = 0
  ClaimChildren = false
  Context = -> Part [Body.Binder.]
  Fuse = false
  MakeFace = true
  OffsetFill = false
  OffsetIntersection = false
  OffsetJoinType = 0
  OffsetOpenResult = false
  PartialLoad = false
  Placement = pos=(0,135,0) rot=(0,0,1;0rad)
  Refine = true
  Relative = true
  Support = -> [<external Chassis.FCStd>#Part[Body.Sketch017.]]
  _Version = 2
FEATURE [Sketcher::SketchObject] Sketch
  ArcFitTolerance = 1e-06
  AttachmentSupport = -> [XY_Plane001]
  ExternalGeometry = -> [Binder]
  FullyConstrained = true
  MakeInternals = false
  MapMode = 5
  sketch-geometry (26):
    g0: LineSegment [constr] StartX=-46 StartY=-28 StartZ=0 EndX=46 EndY=-28 EndZ=0
    g1: LineSegment [constr] StartX=46 StartY=-28 StartZ=0 EndX=46 EndY=27 EndZ=0
    g2: LineSegment StartX=46 StartY=27 StartZ=0 EndX=-46 EndY=27 EndZ=0
    g3: LineSegment StartX=-46 StartY=27 StartZ=0 EndX=-46 EndY=-28 EndZ=0
    g4: GeomPoint [constr] X=-1e-15 Y=-0.5 Z=0
    g5: Circle CenterX=20.85 CenterY=15.85 CenterZ=0 NormalX=0 NormalY=0 NormalZ=1 AngleXU=0 Radius=1.5
    g6: Circle CenterX=-20.85 CenterY=-25.85 CenterZ=0 NormalX=0 NormalY=0 NormalZ=1 AngleXU=0 Radius=1.5
    g7: Circle CenterX=20.85 CenterY=-25.85 CenterZ=0 NormalX=0 NormalY=0 NormalZ=1 AngleXU=0 Radius=1.5
    g8: Circle CenterX=-20.85 CenterY=15.85 CenterZ=0 NormalX=0 NormalY=0 NormalZ=1 AngleXU=0 Radius=1.5
    g9: LineSegment [constr] StartX=-20.85 StartY=15.85 StartZ=0 EndX=20.85 EndY=15.85 EndZ=0
    g10: LineSegment [constr] StartX=20.85 StartY=15.85 StartZ=0 EndX=20.85 EndY=-25.85 EndZ=0
    g11: LineSegment [constr] StartX=20.85 StartY=-25.85 StartZ=0 EndX=-20.85 EndY=-25.85 EndZ=0
    g12: LineSegment [constr] StartX=-20.85 StartY=-25.85 StartZ=0 EndX=-20.85 EndY=15.85 EndZ=0
    g13: Circle CenterX=48.85 CenterY=-0.5 CenterZ=0 NormalX=0 NormalY=0 NormalZ=1 AngleXU=0 Radius=6.75
    g14: LineSegment StartX=46 StartY=27 StartZ=0 EndX=60 EndY=27 EndZ=0
    g15: LineSegment StartX=60 StartY=27 StartZ=0 EndX=60 EndY=-28 EndZ=0
    g16: LineSegment [constr] StartX=46 StartY=-28 StartZ=0 EndX=60 EndY=-28 EndZ=0
    g17: LineSegment [constr] StartX=-1e-15 StartY=-0.5 StartZ=0 EndX=60 EndY=-0.5 EndZ=0
    g18: Circle CenterX=-40 CenterY=21 CenterZ=0 NormalX=0 NormalY=0 NormalZ=1 AngleXU=0 Radius=1.5
    g19: Circle CenterX=40 CenterY=21 CenterZ=0 NormalX=0 NormalY=0 NormalZ=1 AngleXU=0 Radius=1.5
    g20: Circle CenterX=-40 CenterY=-22 CenterZ=0 NormalX=0 NormalY=0 NormalZ=1 AngleXU=0 Radius=1.5
    g21: Circle CenterX=40 CenterY=-22 CenterZ=0 NormalX=0 NormalY=0 NormalZ=1 AngleXU=0 Radius=1.5
    g22: GeomPoint X=0 Y=-5 Z=0
    g23: LineSegment StartX=-46 StartY=-28 StartZ=0 EndX=-46 EndY=-32 EndZ=0
    g24: LineSegment StartX=-46 StartY=-32 StartZ=0 EndX=60 EndY=-32 EndZ=0
    g25: LineSegment StartX=60 StartY=-28 StartZ=0 EndX=60 EndY=-32 EndZ=0
  constraints (62):
    c: Coincident(g0,g1)
    c: Coincident(g1,g2)
    c: Coincident(g2,g3)
    c: Coincident(g3,g0)
    c: Horizontal(g0)
    c: Horizontal(g2)
    c: Vertical(g1)
    c: Vertical(g3)
    c: Symmetric(g2,g0,g4)
    c: DistanceX(g0,g0) = 92
    c: DistanceY(g1,g1) = 55
    c: Diameter(g8) = 3
    c: Equal(g8,g5)
    c: Equal(g5,g6)
    c: Equal(g6,g7)
    c: Coincident(g9,g8)
    c: Coincident(g9,g5)
    c: Coincident(g10,g5)
    c: Coincident(g10,g7)
    c: Coincident(g11,g7)
    c: Coincident(g11,g6)
    c: Horizontal(g11)
    c: Coincident(g12,g6)
    c: Coincident(g12,g8)
    c: Horizontal(g9)
    c: Vertical(g10)
    c: Vertical(g12)
    c: Equal(g9,g12)
    c: DistanceX(g9,g9) = 41.7
    c: Diameter(g13) = 13.5
    c: Coincident(g14,g1)
    c: Horizontal(g14)
    c: Coincident(g15,g14)
    c: Vertical(g15)
    c: Coincident(g16,g0)
    c: Coincident(g16,g15)
    c: Horizontal(g16)
    c: DistanceX(g16,g16) = 14
    c: Coincident(g17,g4)
    c: Symmetric(g15,g15,g17)
    c: PointOnObject(g13,g17)
    c: Distance(g13,g10) = 28
    c: Diameter(g18) = 3
    c: Coincident(g18,g-3)
    c: Coincident(g19,g-4)
    c: Coincident(g20,g-5)
    c: Coincident(g21,g-6)
    c: Equal(g18,g19)
    c: Equal(g19,g20)
    c: Equal(g20,g21)
    c: Symmetric(g19,g20,g4)
    c: PointOnObject(g22,g-2)
    c: Symmetric(g6,g5,g22)
    c: DistanceY(g22,g4) = 4.5
    c: Coincident(g23,g0)
    c: Vertical(g23)
    c: Coincident(g24,g23)
    c: Coincident(g25,g15)
    c: Coincident(g25,g24)
    c: Vertical(g25)
    c: Horizontal(g24)
    c: DistanceY(g25,g25) = 4
FEATURE [PartDesign::Pad] Pad
  Direction = (0,0,1)
  Length = 3
  Length2 = 10
  Profile = -> Sketch
  ReferenceAxis = -> Sketch [N_Axis]
  Refine = true
  Suppressed = false
  Type = 0
FEATURE [Sketcher::SketchObject] Sketch001
  ArcFitTolerance = 1e-06
  AttachmentSupport = -> [Pad]
  ExternalGeometry = -> [Sketch]
  FullyConstrained = true
  MakeInternals = false
  MapMode = 5
  Placement = pos=(0,0,0) rot=(1,0,0;3.14159rad)
  sketch-geometry (8):
    g0: Circle CenterX=-40 CenterY=22 CenterZ=0 NormalX=0 NormalY=0 NormalZ=1 AngleXU=0 Radius=4
    g1: Circle CenterX=40 CenterY=22 CenterZ=0 NormalX=0 NormalY=0 NormalZ=1 AngleXU=0 Radius=4
    g2: Circle CenterX=-40 CenterY=-21 CenterZ=0 NormalX=0 NormalY=0 NormalZ=1 AngleXU=0 Radius=4
    g3: Circle CenterX=40 CenterY=-21 CenterZ=0 NormalX=0 NormalY=0 NormalZ=1 AngleXU=0 Radius=4
    g4: Circle CenterX=-40 CenterY=22 CenterZ=0 NormalX=0 NormalY=0 NormalZ=1 AngleXU=0 Radius=1.5
    g5: Circle CenterX=40 CenterY=22 CenterZ=0 NormalX=0 NormalY=0 NormalZ=1 AngleXU=0 Radius=1.5
    g6: Circle CenterX=-40 CenterY=-21 CenterZ=0 NormalX=0 NormalY=0 NormalZ=1 AngleXU=0 Radius=1.5
    g7: Circle CenterX=40 CenterY=-21 CenterZ=0 NormalX=0 NormalY=0 NormalZ=1 AngleXU=0 Radius=1.5
  constraints (16):
    c: Coincident(g0,g-3)
    c: Coincident(g1,g-4)
    c: Coincident(g2,g-5)
    c: Coincident(g3,g-6)
    c: Diameter(g0) = 8
    c: Equal(g0,g1)
    c: Equal(g1,g2)
    c: Equal(g2,g3)
    c: Coincident(g4,g0)
    c: Coincident(g5,g1)
    c: Coincident(g6,g2)
    c: Coincident(g7,g3)
    c: Equal(g-3,g4)
    c: Equal(g5,g-4)
    c: Equal(g6,g-5)
    c: Equal(g7,g-6)
FEATURE [PartDesign::Pad] Pad001
  BaseFeature = -> Pad
  Direction = (0,0,-1)
  Length = 4
  Length2 = 10
  Profile = -> Sketch001
  ReferenceAxis = -> Sketch001 [N_Axis]
  Refine = true
  Suppressed = false
  Type = 0
FEATURE [PartDesign::Fillet] Fillet
  Base = -> Pad001 [Edge5,Edge1,Edge2,Edge9]
  BaseFeature = -> Pad001
  Radius = 2
  Refine = true
  SupportTransform = false
  Suppressed = false
  UseAllEdges = false
FEATURE [PartDesign::Body] Body  label="LidarPlateBody"
  AllowCompound = false
  Group = -> [Binder,Sketch,Pad,Sketch001,Pad001,Fillet]
  Origin = -> Origin001
  Tip = -> Fillet
FEATURE [App::Part] Part  label="LidarPlatePart"
  Group = -> [Body]
  Origin = -> Origin
---- part ../Parts/MotorGear.FCStd = doc fcstd_910bcae697cb ----
FCSTD DOCUMENT  (FreeCAD 1.0R39285 (Git))
Label: MotorGear
License: All rights reserved
LicenseURL: https://en.wikipedia.org/wiki/All_rights_reserved
objects: PartDesign::Pad×3, Sketcher::SketchObject×3, PartDesign::Pocket×2, Part::Feature×1, PartDesign::FeatureBase×1, PartDesign::Chamfer×1, PartDesign::Body×1, App::Part×1
note: 28 computed .brp shape members not serialized (recipe doc carries the construction recipe); baked Part::Feature solids carry a one-line shape summary decoded from their .brp

FEATURE [Part::Feature] Solid  label="Part 1"
  shape: bbox 25.58 x 25.58 x 7.711 mm, 1760 faces (baked)
FEATURE [PartDesign::FeatureBase] BaseFeature
  BaseFeature = -> Solid
  Suppressed = false
FEATURE [PartDesign::Pad] Pad
  AlongSketchNormal = false
  BaseFeature = -> BaseFeature
  Direction = (0,0,1)
  Length = 10
  Length2 = 10
  Profile = -> BaseFeature [Edge322]
  Refine = true
  Suppressed = false
  Type = 3
  UpToFace = -> BaseFeature [Face19]
FEATURE [PartDesign::Pad] Pad001
  AlongSketchNormal = false
  BaseFeature = -> Pad
  Direction = (0,0,1)
  Length = 10
  Length2 = 10
  Profile = -> Pad [Edge1]
  Refine = true
  Suppressed = false
  Type = 3
  UpToFace = -> Pad [Face1545]
FEATURE [Sketcher::SketchObject] Sketch
  ArcFitTolerance = 1e-06
  AttachmentSupport = -> [Pad001]
  FullyConstrained = true
  MakeInternals = false
  MapMode = 5
  Placement = pos=(0,0,-3.85) rot=(1,0,0;3.14159rad)
  sketch-geometry (1):
    g0: Circle CenterX=0 CenterY=0 CenterZ=0 NormalX=0 NormalY=0 NormalZ=1 AngleXU=0 Radius=6
  constraints (2):
    c: Coincident(g0,g-3)
    c: Diameter(g0) = 12
FEATURE [PartDesign::Pocket] Pocket
  BaseFeature = -> Pad001
  Direction = (0,0,1)
  Length = 2
  Length2 = 5
  Profile = -> Sketch
  ReferenceAxis = -> Sketch [N_Axis]
  Refine = true
  Suppressed = false
  Type = 0
FEATURE [Sketcher::SketchObject] Sketch002
  ArcFitTolerance = 1e-06
  AttachmentSupport = -> [Pocket]
  FullyConstrained = true
  MakeInternals = false
  MapMode = 5
  Placement = pos=(0,0,-3.85) rot=(1,0,0;3.14159rad)
  sketch-geometry (1):
    g0: Circle CenterX=0 CenterY=0 CenterZ=0 NormalX=0 NormalY=0 NormalZ=1 AngleXU=0 Radius=3
  constraints (2):
    c: Coincident(g0,g-1)
    c: Diameter(g0) = 6
FEATURE [PartDesign::Pad] Pad004
  AlongSketchNormal = false
  BaseFeature = -> Pocket
  Direction = (0,0,-1)
  Length = 7
  Length2 = 10
  Profile = -> Sketch002
  ReferenceAxis = -> Sketch002 [N_Axis]
  Suppressed = false
  Type = 0
FEATURE [Sketcher::SketchObject] Sketch001
  ArcFitTolerance = 1e-06
  AttachmentSupport = -> [Pad004]
  FullyConstrained = true
  MakeInternals = false
  MapMode = 5
  Placement = pos=(0,0,3.85) rot=(0,0,1;0rad)
  sketch-geometry (5):
    g0: ArcOfCircle CenterX=0 CenterY=0 CenterZ=0 NormalX=0 NormalY=0 NormalZ=1 AngleXU=0 Radius=1.65 StartAngle=5.84506 EndAngle=9.8629
    g1: LineSegment StartX=-0.9 StartY=-1.1 StartZ=0 EndX=0.9 EndY=-1.1 EndZ=0
    g2: ArcOfCircle CenterX=-1.29658 CenterY=-1.0478 CenterZ=0 NormalX=0 NormalY=0 NormalZ=1 AngleXU=0 Radius=0.4 StartAngle=2.08741 EndAngle=6.15231
    g3: ArcOfCircle CenterX=1.29658 CenterY=-1.0478 CenterZ=0 NormalX=0 NormalY=0 NormalZ=1 AngleXU=0 Radius=0.4 StartAngle=3.27247 EndAngle=7.33737
    g4: LineSegment [constr] StartX=-1.49416 StartY=-0.7 StartZ=0 EndX=1.49416 EndY=-0.7 EndZ=0
  constraints (15):
    c: Coincident(g0,g-1)
    c: Diameter(g0) = 3.3
    c: Distance(g0,g1) = 1.1
    c: Coincident(g2,g1)
    c: Coincident(g2,g0)
    c: Coincident(g3,g1)
    c: Coincident(g3,g0)
    c: Equal(g2,g3)
    c: Symmetric(g1,g1,g-2)
    c: Radius(g2) = 0.4
    c: DistanceX(g1,g1) = 1.8
    c: Coincident(g4,g0)
    c: Coincident(g4,g0)
    c: Horizontal(g4)
    c: DistanceY(g1,g0) = 0.4
FEATURE [PartDesign::Pocket] Pocket001
  BaseFeature = -> Pad004
  Direction = (0,0,-1)
  Length = 11
  Length2 = 5
  Profile = -> Sketch001
  ReferenceAxis = -> Sketch001 [N_Axis]
  Refine = true
  Suppressed = false
  Type = 0
FEATURE [PartDesign::Chamfer] Chamfer
  Angle = 60
  Base = -> Pocket001 [Edge4,Edge6,Edge5,Edge7]
  BaseFeature = -> Pocket001
  ChamferType = 2
  FlipDirection = false
  Size = 0.4
  Size2 = 1
  SupportTransform = false
  Suppressed = false
  UseAllEdges = false
FEATURE [PartDesign::Body] Body  label="MotorGearBody"
  AllowCompound = false
  BaseFeature = -> Solid
  Group = -> [BaseFeature,Pad,Pad001,Sketch,Pocket,Pad004,Sketch002,Sketch001,Pocket001,Chamfer]
  Origin = -> Origin
  Tip = -> Chamfer
FEATURE [App::Part] Part  label="MotorGearPart"
  Group = -> [Solid,Body]
  Origin = -> Origin001
---- part ../Parts/MotorHolder.FCStd = doc fcstd_153913d49564 ----
FCSTD DOCUMENT  (FreeCAD 1.0R39319 (Git))
Label: MotorHolder
License: All rights reserved
LicenseURL: https://en.wikipedia.org/wiki/All_rights_reserved
objects: Sketcher::SketchObject×2, PartDesign::SubShapeBinder×1, PartDesign::Pad×1, PartDesign::Pocket×1, PartDesign::Body×1, App::Part×1
note: 12 computed .brp shape members not serialized (recipe doc carries the construction recipe); baked Part::Feature solids carry a one-line shape summary decoded from their .brp
EXTERNAL_REF file=MotorPlate.FCStd obj=Part

FEATURE [PartDesign::SubShapeBinder] Binder  label="MotorPlateBody"
  BindCopyOnChange = 0
  BindMode = 0
  ClaimChildren = false
  Context = -> Part [Body.Binder.]
  Fuse = false
  MakeFace = true
  OffsetFill = false
  OffsetIntersection = false
  OffsetJoinType = 0
  OffsetOpenResult = false
  PartialLoad = false
  Placement = pos=(-5,0,0) rot=(0,0,1;0rad)
  Refine = true
  Relative = true
  Support = -> [<external MotorPlate.FCStd>#Part[Body.]]
  _Version = 2
FEATURE [Sketcher::SketchObject] Sketch
  ArcFitTolerance = 1e-06
  AttachmentSupport = -> [YZ_Plane001]
  ExternalGeometry = -> [Binder]
  FullyConstrained = true
  MakeInternals = false
  MapMode = 5
  Placement = pos=(0,0,0) rot=(0.57735,0.57735,0.57735;2.0944rad)
  sketch-geometry (13):
    g0: LineSegment StartX=-9 StartY=-15 StartZ=0 EndX=1.8e-15 EndY=-15 EndZ=0
    g1: LineSegment StartX=1.8e-15 StartY=-15 StartZ=0 EndX=1.8e-15 EndY=-25 EndZ=0
    g2: LineSegment StartX=1.8e-15 StartY=-25 StartZ=0 EndX=12 EndY=-25 EndZ=0
    g3: LineSegment StartX=12 StartY=-25 StartZ=0 EndX=12 EndY=-15 EndZ=0
    g4: LineSegment StartX=12 StartY=-15 StartZ=0 EndX=21 EndY=-15 EndZ=0
    g5: LineSegment [constr] StartX=6 StartY=-15 StartZ=0 EndX=6 EndY=-27 EndZ=0
    g6: LineSegment StartX=-9 StartY=-15 StartZ=0 EndX=-9 EndY=-18 EndZ=0
    g7: LineSegment StartX=-9 StartY=-18 StartZ=0 EndX=-2 EndY=-18 EndZ=0
    g8: LineSegment StartX=-2 StartY=-18 StartZ=0 EndX=-2 EndY=-27 EndZ=0
    g9: LineSegment StartX=-2 StartY=-27 StartZ=0 EndX=14 EndY=-27 EndZ=0
    g10: LineSegment StartX=14 StartY=-27 StartZ=0 EndX=14 EndY=-18 EndZ=0
    g11: LineSegment StartX=14 StartY=-18 StartZ=0 EndX=21 EndY=-18 EndZ=0
    g12: LineSegment StartX=21 StartY=-18 StartZ=0 EndX=21 EndY=-15 EndZ=0
  constraints (32):
    c: Coincident(g0,g-3)
    c: PointOnObject(g0,g-3)
    c: Coincident(g1,g0)
    c: Coincident(g2,g1)
    c: Coincident(g3,g2)
    c: PointOnObject(g3,g-3)
    c: Coincident(g4,g3)
    c: Coincident(g4,g-3)
    c: Symmetric(g-3,g-3,g5)
    c: Symmetric(g0,g3,g5)
    c: Symmetric(g1,g2,g5)
    c: Vertical(g1)
    c: Coincident(g6,g0)
    c: Vertical(g6)
    c: Coincident(g7,g6)
    c: Horizontal(g7)
    c: Coincident(g8,g7)
    c: Vertical(g8)
    c: Coincident(g9,g8)
    c: Coincident(g10,g9)
    c: Coincident(g11,g10)
    c: Coincident(g12,g11)
    c: Coincident(g12,g4)
    c: Symmetric(g6,g11,g5)
    c: Symmetric(g7,g10,g5)
    c: Symmetric(g8,g9,g5)
    c: PointOnObject(g5,g9)
    c: DistanceY(g6,g6) = 3
    c: Distance(g1,g8) = 2
    c: DistanceX(g0,g3) = 12
    c: DistanceY(g8,g1) = 2
    c: DistanceY(g1,g1) = 10
FEATURE [PartDesign::Pad] Pad
  Direction = (1,0,0)
  Length = 10
  Length2 = 10
  Placement = pos=(0,0,0) rot=(1,1,1;2.0944rad)
  Profile = -> Sketch
  ReferenceAxis = -> Sketch [N_Axis]
  Refine = true
  Suppressed = false
  Type = 0
FEATURE [Sketcher::SketchObject] Sketch001
  ArcFitTolerance = 1e-06
  AttachmentSupport = -> [Pad]
  ExternalGeometry = -> [Binder]
  FullyConstrained = true
  MakeInternals = false
  MapMode = 5
  Placement = pos=(1.7e-15,-5e-15,-15) rot=(0,0,-1;1.5708rad)
  sketch-geometry (2):
    g0: Circle CenterX=6 CenterY=5 CenterZ=0 NormalX=0 NormalY=0 NormalZ=1 AngleXU=0 Radius=1.6
    g1: Circle CenterX=-18 CenterY=5 CenterZ=0 NormalX=0 NormalY=0 NormalZ=1 AngleXU=0 Radius=1.6
  constraints (4):
    c: Coincident(g0,g-3)
    c: Coincident(g1,g-4)
    c: Diameter(g1) = 3.2
    c: Equal(g1,g0)
FEATURE [PartDesign::Pocket] Pocket
  BaseFeature = -> Pad
  Direction = (0,0,-1)
  Length = 0
  Length2 = 5
  Placement = pos=(0,0,0) rot=(1,1,1;2.0944rad)
  Profile = -> Sketch001
  ReferenceAxis = -> Sketch001 [N_Axis]
  Refine = true
  Suppressed = false
  Type = 3
  UpToFace = -> Pad [Face11]
FEATURE [PartDesign::Body] Body  label="MotorHolderBody"
  AllowCompound = false
  Group = -> [Binder,Sketch,Pad,Sketch001,Pocket]
  Origin = -> Origin001
  Tip = -> Pocket
FEATURE [App::Part] Part  label="MotorHolderPart"
  Group = -> [Body]
  Origin = -> Origin
---- part ../Parts/MotorPlate.FCStd = doc fcstd_dda2ee011445 ----
FCSTD DOCUMENT  (FreeCAD 1.0R39319 (Git))
Label: MotorPlate
License: All rights reserved
LicenseURL: https://en.wikipedia.org/wiki/All_rights_reserved
objects: Sketcher::SketchObject×3, PartDesign::Pad×2, PartDesign::SubShapeBinder×1, PartDesign::Pocket×1, PartDesign::Body×1, App::Part×1
note: 17 computed .brp shape members not serialized (recipe doc carries the construction recipe); baked Part::Feature solids carry a one-line shape summary decoded from their .brp
EXTERNAL_REF file=Chassis.FCStd obj=Part

FEATURE [PartDesign::SubShapeBinder] Binder  label="ChassisBody"
  BindCopyOnChange = 0
  BindMode = 0
  ClaimChildren = false
  Context = -> Part [Body.Binder.]
  Fuse = false
  MakeFace = true
  OffsetFill = false
  OffsetIntersection = false
  OffsetJoinType = 0
  OffsetOpenResult = false
  PartialLoad = false
  Placement = pos=(0,200,0) rot=(0,0,1;0rad)
  Refine = true
  Relative = true
  Support = -> [<external Chassis.FCStd>#Part[Body.]]
  _Version = 2
FEATURE [Sketcher::SketchObject] Sketch
  ArcFitTolerance = 1e-06
  AttachmentSupport = -> [XY_Plane001]
  ExternalGeometry = -> [Binder]
  FullyConstrained = true
  MakeInternals = false
  MapMode = 5
  sketch-geometry (12):
    g0: LineSegment StartX=-23 StartY=21 StartZ=0 EndX=23 EndY=21 EndZ=0
    g1: LineSegment StartX=23 StartY=21 StartZ=0 EndX=23 EndY=13.5 EndZ=0
    g2: LineSegment StartX=23 StartY=13.5 StartZ=0 EndX=16 EndY=13.5 EndZ=0
    g3: LineSegment StartX=16 StartY=13.5 StartZ=0 EndX=16 EndY=-1.5 EndZ=0
    g4: LineSegment StartX=16 StartY=-1.5 StartZ=0 EndX=23 EndY=-1.5 EndZ=0
    g5: LineSegment StartX=23 StartY=-1.5 StartZ=0 EndX=23 EndY=-22 EndZ=0
    g6: LineSegment StartX=23 StartY=-22 StartZ=0 EndX=-23 EndY=-22 EndZ=0
    g7: LineSegment StartX=-23 StartY=-22 StartZ=0 EndX=-23 EndY=21 EndZ=0
    g8: Circle CenterX=-19.5 CenterY=18 CenterZ=0 NormalX=0 NormalY=0 NormalZ=1 AngleXU=0 Radius=1.65
    g9: Circle CenterX=19.5 CenterY=18 CenterZ=0 NormalX=0 NormalY=0 NormalZ=1 AngleXU=0 Radius=1.65
    g10: Circle CenterX=-19.5 CenterY=-19 CenterZ=0 NormalX=0 NormalY=0 NormalZ=1 AngleXU=0 Radius=1.65
    g11: Circle CenterX=19.5 CenterY=-19 CenterZ=0 NormalX=0 NormalY=0 NormalZ=1 AngleXU=0 Radius=1.65
  constraints (24):
    c: Coincident(g0,g-4)
    c: Coincident(g0,g-11)
    c: Coincident(g1,g0)
    c: Coincident(g1,g-12)
    c: Coincident(g2,g1)
    c: Coincident(g2,g-12)
    c: Coincident(g3,g2)
    c: Coincident(g3,g-15)
    c: Coincident(g4,g3)
    c: Coincident(g4,g-16)
    c: Coincident(g5,g4)
    c: Coincident(g5,g-17)
    c: Coincident(g6,g5)
    c: Coincident(g6,g-6)
    c: Coincident(g7,g6)
    c: Coincident(g7,g0)
    c: Coincident(g8,g-8)
    c: Coincident(g9,g-13)
    c: Coincident(g10,g-7)
    c: Coincident(g11,g-18)
    c: Diameter(g9) = 3.3
    c: Equal(g9,g8)
    c: Equal(g8,g10)
    c: Equal(g10,g11)
FEATURE [PartDesign::Pad] Pad
  Direction = (0,0,1)
  Length = 5
  Length2 = 10
  Profile = -> Sketch
  ReferenceAxis = -> Sketch [N_Axis]
  Refine = true
  Reversed = true
  Suppressed = false
  Type = 0
FEATURE [Sketcher::SketchObject] Sketch001
  ArcFitTolerance = 1e-06
  AttachmentSupport = -> [Pad]
  ExternalGeometry = -> [Sketch]
  FullyConstrained = true
  MakeInternals = false
  MapMode = 5
  Placement = pos=(0,0,-5) rot=(1,0,0;3.14159rad)
  sketch-geometry (6):
    g0: LineSegment StartX=15 StartY=9 StartZ=0 EndX=5 EndY=9 EndZ=0
    g1: LineSegment StartX=5 StartY=9 StartZ=0 EndX=5 EndY=-21 EndZ=0
    g2: LineSegment StartX=5 StartY=-21 StartZ=0 EndX=15 EndY=-21 EndZ=0
    g3: LineSegment StartX=15 StartY=-21 StartZ=0 EndX=15 EndY=9 EndZ=0
    g4: GeomPoint [constr] X=10 Y=-6 Z=0
    g5: LineSegment [constr] StartX=16 StartY=-6 StartZ=0 EndX=-23 EndY=-6 EndZ=0
  constraints (16):
    c: Coincident(g0,g1)
    c: Coincident(g1,g2)
    c: Coincident(g2,g3)
    c: Coincident(g3,g0)
    c: Horizontal(g0)
    c: Horizontal(g2)
    c: Vertical(g1)
    c: Vertical(g3)
    c: Symmetric(g2,g0,g4)
    c: PointOnObject(g1,g-3)
    c: Symmetric(g-5,g-5,g5)
    c: PointOnObject(g5,g-4)
    c: Horizontal(g5)
    c: PointOnObject(g4,g5)
    c: DistanceX(g0,g0) = 10
    c: Distance(g0,g-4) = 28
FEATURE [PartDesign::Pad] Pad001
  BaseFeature = -> Pad
  Direction = (0,0,-1)
  Length = 10
  Length2 = 10
  Profile = -> Sketch001
  ReferenceAxis = -> Sketch001 [N_Axis]
  Refine = true
  Suppressed = false
  Type = 0
FEATURE [Sketcher::SketchObject] Sketch002
  ArcFitTolerance = 1e-06
  AttachmentSupport = -> [Pad001]
  ExternalGeometry = -> [Sketch001]
  FullyConstrained = true
  MakeInternals = false
  MapMode = 5
  Placement = pos=(0,0,-15) rot=(1,0,0;3.14159rad)
  sketch-geometry (3):
    g0: LineSegment [constr] StartX=10 StartY=9 StartZ=0 EndX=10 EndY=-21 EndZ=0
    g1: Circle CenterX=10 CenterY=6 CenterZ=0 NormalX=0 NormalY=0 NormalZ=1 AngleXU=0 Radius=1.5
    g2: Circle CenterX=10 CenterY=-18 CenterZ=0 NormalX=0 NormalY=0 NormalZ=1 AngleXU=0 Radius=1.5
  constraints (8):
    c: Symmetric(g-3,g-3,g0)
    c: Symmetric(g-4,g-4,g0)
    c: Diameter(g1) = 3
    c: PointOnObject(g1,g0)
    c: Diameter(g2) = 3
    c: PointOnObject(g2,g0)
    c: Distance(g1,g-3) = 3
    c: Distance(g2,g-4) = 3
FEATURE [PartDesign::Pocket] Pocket
  BaseFeature = -> Pad001
  Direction = (0,0,1)
  Length = 0
  Length2 = 5
  Profile = -> Sketch002
  ReferenceAxis = -> Sketch002 [N_Axis]
  Refine = true
  Suppressed = false
  Type = 3
  UpToFace = -> Pad001 [Face2]
FEATURE [PartDesign::Body] Body  label="MotorPlateBody"
  AllowCompound = false
  Group = -> [Binder,Sketch,Pad,Sketch001,Pad001,Sketch002,Pocket]
  Origin = -> Origin001
  Tip = -> Pocket
FEATURE [App::Part] Part  label="MotorPlatePart"
  Group = -> [Body]
  Origin = -> Origin
---- part ../Parts/TBoneLinkage/TBoneLinkageBottom.FCStd = doc fcstd_ef4fcdcf9c16 ----
FCSTD DOCUMENT  (FreeCAD 1.0R39285 (Git))
Label: TBoneLinkageBottom
License: All rights reserved
LicenseURL: https://en.wikipedia.org/wiki/All_rights_reserved
objects: Sketcher::SketchObject×5, PartDesign::Pad×4, App::Link×1, PartDesign::Pocket×1, PartDesign::Body×1, App::Part×1
note: 26 computed .brp shape members not serialized (recipe doc carries the construction recipe); baked Part::Feature solids carry a one-line shape summary decoded from their .brp
EXTERNAL_REF file=../../Models/SteeringAckermannModel.FCStd obj=Spreadsheet

FEATURE [App::Link] Link  label="SteeringAckermannSpreadsheet"
  LinkedObject = -> <external ../../Models/SteeringAckermannModel.FCStd>#Spreadsheet
FEATURE [Sketcher::SketchObject] Sketch
  ArcFitTolerance = 1e-06
  AttachmentSupport = -> [XY_Plane001]
  FullyConstrained = true
  MakeInternals = false
  MapMode = 5
  expr: Constraints[4] = <<SteeringAckermannSpreadsheet>>.servolinkagelength
  expr: Constraints[5] = <<SteeringAckermannSpreadsheet>>.servolinkagesep
  sketch-geometry (8):
    g0: LineSegment [constr] StartX=0 StartY=0 StartZ=0 EndX=0 EndY=-12 EndZ=0
    g1: LineSegment [constr] StartX=-5 StartY=-12 StartZ=0 EndX=5 EndY=-12 EndZ=0
    g2: ArcOfCircle CenterX=0 CenterY=0 CenterZ=0 NormalX=0 NormalY=0 NormalZ=1 AngleXU=0 Radius=4.1 StartAngle=0.394791 EndAngle=2.7468
    g3: ArcOfCircle CenterX=-5 CenterY=-12 CenterZ=0 NormalX=0 NormalY=0 NormalZ=1 AngleXU=0 Radius=4.1 StartAngle=2.7468 EndAngle=4.71239
    g4: ArcOfCircle CenterX=5 CenterY=-12 CenterZ=0 NormalX=0 NormalY=0 NormalZ=1 AngleXU=0 Radius=4.1 StartAngle=4.71239 EndAngle=6.67798
    g5: LineSegment StartX=-8.78462 StartY=-10.4231 StartZ=0 EndX=-3.78462 EndY=1.57692 EndZ=0
    g6: LineSegment StartX=3.78462 StartY=1.57692 StartZ=0 EndX=8.78462 EndY=-10.4231 EndZ=0
    g7: LineSegment StartX=5 StartY=-16.1 StartZ=0 EndX=-5 EndY=-16.1 EndZ=0
  constraints (18):
    c: Coincident(g0,g-1)
    c: Vertical(g0)
    c: Symmetric(g1,g1,g0)
    c: Horizontal(g1)
    c: DistanceY(g0,g0) = 12
    c: DistanceX(g1,g1) = 10
    c: Coincident(g2,g0)
    c: Coincident(g3,g1)
    c: Coincident(g4,g1)
    c: Horizontal(g7)
    c: Tangent(g5,g2) = 1.5708
    c: Tangent(g5,g3) = 1.5708
    c: Tangent(g7,g3) = 1.5708
    c: Tangent(g7,g4) = 1.5708
    c: Tangent(g6,g4) = 1.5708
    c: Tangent(g6,g2) = 1.5708
    c: Radius(g2) = 4.1
    c: Radius(g3) = 4.1
FEATURE [PartDesign::Pad] Pad
  Direction = (0,0,1)
  Length = 2
  Length2 = 10
  Profile = -> Sketch
  ReferenceAxis = -> Sketch [N_Axis]
  Refine = true
  Suppressed = false
  Type = 0
FEATURE [Sketcher::SketchObject] Sketch001
  ArcFitTolerance = 1e-06
  AttachmentSupport = -> [Pad]
  ExternalGeometry = -> [Sketch]
  FullyConstrained = true
  MakeInternals = false
  MapMode = 5
  Placement = pos=(0,0,2) rot=(0,0,1;0rad)
  sketch-geometry (2):
    g0: Circle CenterX=-5 CenterY=-12 CenterZ=0 NormalX=0 NormalY=0 NormalZ=1 AngleXU=0 Radius=2.5
    g1: Circle CenterX=5 CenterY=-12 CenterZ=0 NormalX=0 NormalY=0 NormalZ=1 AngleXU=0 Radius=2.5
  constraints (4):
    c: Coincident(g0,g-3)
    c: Coincident(g1,g-4)
    c: Diameter(g0) = 5
    c: Equal(g0,g1)
FEATURE [PartDesign::Pad] Pad001
  BaseFeature = -> Pad
  Direction = (0,0,1)
  Length = 0.5
  Length2 = 10
  Profile = -> Sketch001
  ReferenceAxis = -> Sketch001 [N_Axis]
  Refine = true
  Suppressed = false
  Type = 0
FEATURE [Sketcher::SketchObject] Sketch002
  ArcFitTolerance = 1e-06
  AttachmentSupport = -> [Pad001]
  ExternalGeometry = -> [Sketch]
  FullyConstrained = true
  MakeInternals = false
  MapMode = 5
  Placement = pos=(0,0,2.5) rot=(0,0,1;0rad)
  sketch-geometry (2):
    g0: Circle CenterX=-5 CenterY=-12 CenterZ=0 NormalX=0 NormalY=0 NormalZ=1 AngleXU=0 Radius=1.5
    g1: Circle CenterX=5 CenterY=-12 CenterZ=0 NormalX=0 NormalY=0 NormalZ=1 AngleXU=0 Radius=1.5
  constraints (4):
    c: Diameter(g0) = 3
    c: Coincident(g0,g-3)
    c: Coincident(g1,g-4)
    c: Equal(g0,g1)
FEATURE [PartDesign::Pad] Pad002
  BaseFeature = -> Pad001
  Direction = (0,0,1)
  Length = 4.5
  Length2 = 10
  Profile = -> Sketch002
  ReferenceAxis = -> Sketch002 [N_Axis]
  Refine = true
  Suppressed = false
  Type = 0
FEATURE [Sketcher::SketchObject] Sketch003
  ArcFitTolerance = 1e-06
  AttachmentSupport = -> [Pad002]
  ExternalGeometry = -> [Sketch]
  FullyConstrained = true
  MakeInternals = false
  MapMode = 5
  Placement = pos=(0,0,2) rot=(0,0,1;0rad)
  sketch-geometry (6):
    g0: ArcOfCircle CenterX=0 CenterY=0 CenterZ=0 NormalX=0 NormalY=0 NormalZ=1 AngleXU=0 Radius=4.1 StartAngle=0.394791 EndAngle=2.7468
    g1: LineSegment StartX=-3.78462 StartY=1.57692 StartZ=0 EndX=-6.47692 EndY=-4.88462 EndZ=0
    g2: LineSegment StartX=3.78462 StartY=1.57692 StartZ=0 EndX=6.47692 EndY=-4.88462 EndZ=0
    g3: LineSegment StartX=-6.47692 StartY=-4.88462 StartZ=0 EndX=-9e-16 EndY=-7.58333 EndZ=0
    g4: LineSegment StartX=-9e-16 StartY=-7.58333 StartZ=0 EndX=6.47692 EndY=-4.88462 EndZ=0
    g5: Circle CenterX=0 CenterY=0 CenterZ=0 NormalX=0 NormalY=0 NormalZ=1 AngleXU=0 Radius=1
  constraints (14):
    c: Coincident(g0,g-1)
    c: Coincident(g3,g1)
    c: Coincident(g4,g2)
    c: Tangent(g1,g0) = -1.5708
    c: Tangent(g2,g0) = 1.5708
    c: Coincident(g0,g-6)
    c: PointOnObject(g2,g-7)
    c: Equal(g1,g2)
    c: Distance(g1,g1) = 7
    c: Perpendicular(g3,g1)
    c: Coincident(g3,g4)
    c: Equal(g3,g4)
    c: Diameter(g5) = 2
    c: Coincident(g5,g0)
FEATURE [PartDesign::Pad] Pad003
  BaseFeature = -> Pad002
  Direction = (0,0,1)
  Length = 3
  Length2 = 10
  Profile = -> Sketch003
  ReferenceAxis = -> Sketch003 [N_Axis]
  Refine = true
  Suppressed = false
  Type = 0
FEATURE [Sketcher::SketchObject] Sketch004
  ArcFitTolerance = 1e-06
  AttachmentSupport = -> [Pad003]
  ExternalGeometry = -> [Sketch]
  FullyConstrained = true
  MakeInternals = false
  MapMode = 5
  Placement = pos=(0,0,0) rot=(1,0,0;3.14159rad)
  sketch-geometry (1):
    g0: Circle CenterX=0 CenterY=0 CenterZ=0 NormalX=0 NormalY=0 NormalZ=1 AngleXU=0 Radius=2.5
  constraints (2):
    c: Diameter(g0) = 5
    c: Coincident(g0,g-1)
FEATURE [PartDesign::Pocket] Pocket
  BaseFeature = -> Pad003
  Direction = (0,0,1)
  Length = 4
  Length2 = 5
  Profile = -> Sketch004
  ReferenceAxis = -> Sketch004 [N_Axis]
  Refine = true
  Suppressed = false
  Type = 0
FEATURE [PartDesign::Body] Body  label="TBoneLinkageBottomBody"
  AllowCompound = false
  Group = -> [Sketch,Pad,Sketch001,Pad001,Sketch002,Pad002,Sketch003,Pad003,Sketch004,Pocket]
  Origin = -> Origin001
  Tip = -> Pocket
FEATURE [App::Part] Part  label="TBoneLinkageBottomPart"
  Group = -> [Body]
  Origin = -> Origin
---- part ../Parts/TBoneLinkage/TBoneLinkageTop.FCStd = doc fcstd_5407f23f83f5 ----
FCSTD DOCUMENT  (FreeCAD 1.0R39285 (Git))
Label: TBoneLinkageTop
License: All rights reserved
LicenseURL: https://en.wikipedia.org/wiki/All_rights_reserved
objects: Sketcher::SketchObject×2, PartDesign::Pad×2, PartDesign::SubShapeBinder×1, PartDesign::Body×1, App::Part×1
note: 12 computed .brp shape members not serialized (recipe doc carries the construction recipe); baked Part::Feature solids carry a one-line shape summary decoded from their .brp
EXTERNAL_REF file=TBoneLinkageBottom.FCStd obj=Part

FEATURE [PartDesign::SubShapeBinder] Binder  label="TBoneLinkageBottomSketch"
  BindCopyOnChange = 0
  BindMode = 0
  ClaimChildren = false
  Context = -> Part [Body.Binder.]
  Fuse = false
  MakeFace = true
  OffsetFill = false
  OffsetIntersection = false
  OffsetJoinType = 0
  OffsetOpenResult = false
  PartialLoad = false
  Refine = true
  Relative = true
  Support = -> [<external TBoneLinkageBottom.FCStd>#Part[Body.Sketch.]]
  _Version = 2
FEATURE [Sketcher::SketchObject] Sketch
  ArcFitTolerance = 1e-06
  AttachmentSupport = -> [XY_Plane001]
  ExternalGeometry = -> [Binder]
  FullyConstrained = true
  MakeInternals = false
  MapMode = 5
  sketch-geometry (9):
    g0: ArcOfCircle CenterX=0 CenterY=0 CenterZ=0 NormalX=0 NormalY=0 NormalZ=1 AngleXU=0 Radius=4.1 StartAngle=0.394791 EndAngle=2.7468
    g1: ArcOfCircle CenterX=-5 CenterY=-12 CenterZ=0 NormalX=0 NormalY=0 NormalZ=1 AngleXU=0 Radius=4.1 StartAngle=2.7468 EndAngle=4.71239
    g2: ArcOfCircle CenterX=5 CenterY=-12 CenterZ=0 NormalX=0 NormalY=0 NormalZ=1 AngleXU=0 Radius=4.1 StartAngle=4.71239 EndAngle=6.67798
    g3: LineSegment StartX=-3.78462 StartY=1.57692 StartZ=0 EndX=-8.78462 EndY=-10.4231 EndZ=0
    g4: LineSegment StartX=-5.00001 StartY=-16.1 StartZ=0 EndX=5 EndY=-16.1 EndZ=0
    g5: LineSegment StartX=8.78462 StartY=-10.4231 StartZ=0 EndX=3.78462 EndY=1.57692 EndZ=0
    g6: Circle CenterX=-5 CenterY=-12 CenterZ=0 NormalX=0 NormalY=0 NormalZ=1 AngleXU=0 Radius=1.64
    g7: Circle CenterX=5 CenterY=-12 CenterZ=0 NormalX=0 NormalY=0 NormalZ=1 AngleXU=0 Radius=1.64
    g8: Circle CenterX=0 CenterY=0 CenterZ=0 NormalX=0 NormalY=0 NormalZ=1 AngleXU=0 Radius=1.9
  constraints (17):
    c: Coincident(g0,g-1)
    c: Coincident(g1,g-6)
    c: Coincident(g2,g-7)
    c: Coincident(g4,g1)
    c: Tangent(g3,g0) = -1.5708
    c: Tangent(g3,g1) = -1.5708
    c: Tangent(g4,g2) = -1.5708
    c: Tangent(g5,g2) = -1.5708
    c: Tangent(g5,g0) = -1.5708
    c: Coincident(g0,g-5)
    c: Coincident(g2,g-8)
    c: Diameter(g6) = 3.28
    c: Coincident(g6,g1)
    c: Coincident(g7,g2)
    c: Equal(g6,g7)
    c: Diameter(g8) = 3.8
    c: Coincident(g8,g0)
FEATURE [PartDesign::Pad] Pad
  Direction = (0,0,1)
  Length = 2
  Length2 = 10
  Profile = -> Sketch
  ReferenceAxis = -> Sketch [N_Axis]
  Refine = true
  Reversed = true
  Suppressed = false
  Type = 0
FEATURE [Sketcher::SketchObject] Sketch001
  ArcFitTolerance = 1e-06
  AttachmentSupport = -> [Pad]
  ExternalGeometry = -> [Sketch]
  FullyConstrained = true
  MakeInternals = false
  MapMode = 5
  Placement = pos=(0,0,-2) rot=(1,0,0;3.14159rad)
  sketch-geometry (4):
    g0: Circle CenterX=-5 CenterY=12 CenterZ=0 NormalX=0 NormalY=0 NormalZ=1 AngleXU=0 Radius=1.64
    g1: Circle CenterX=5 CenterY=12 CenterZ=0 NormalX=0 NormalY=0 NormalZ=1 AngleXU=0 Radius=1.64
    g2: Circle CenterX=-5 CenterY=12 CenterZ=0 NormalX=0 NormalY=0 NormalZ=1 AngleXU=0 Radius=2.5
    g3: Circle CenterX=5 CenterY=12 CenterZ=0 NormalX=0 NormalY=0 NormalZ=1 AngleXU=0 Radius=2.5
  constraints (8):
    c: Coincident(g0,g-3)
    c: Coincident(g1,g-4)
    c: Equal(g0,g-3)
    c: Equal(g1,g-4)
    c: Coincident(g2,g0)
    c: Coincident(g3,g1)
    c: Diameter(g2) = 5
    c: Equal(g2,g3)
FEATURE [PartDesign::Pad] Pad001
  BaseFeature = -> Pad
  Direction = (0,0,-1)
  Length = 0.5
  Length2 = 10
  Profile = -> Sketch001
  ReferenceAxis = -> Sketch001 [N_Axis]
  Refine = true
  Suppressed = false
  Type = 0
FEATURE [PartDesign::Body] Body  label="TBoneLinkageTopBody"
  AllowCompound = false
  Group = -> [Binder,Sketch,Pad,Sketch001,Pad001]
  Origin = -> Origin001
  Tip = -> Pad001
FEATURE [App::Part] Part  label="TBoneLinkageTopPart"
  Group = -> [Body]
  Origin = -> Origin
---- part ../Parts/TransferLinkage/TransferLinkageLeft.FCStd = doc fcstd_a7fe9f0c62bb ----
FCSTD DOCUMENT  (FreeCAD 1.0R39285 (Git))
Label: TransferLinkageLeft
License: All rights reserved
LicenseURL: https://en.wikipedia.org/wiki/All_rights_reserved
objects: Sketcher::SketchObject×1, App::Link×1, PartDesign::Pad×1, PartDesign::Body×1, App::Part×1
note: 6 computed .brp shape members not serialized (recipe doc carries the construction recipe); baked Part::Feature solids carry a one-line shape summary decoded from their .brp
EXTERNAL_REF file=../../Models/SteeringAckermannModel.FCStd obj=Spreadsheet

FEATURE [Sketcher::SketchObject] Sketch
  ArcFitTolerance = 1e-06
  AttachmentSupport = -> [XY_Plane001]
  FullyConstrained = true
  MakeInternals = false
  MapMode = 5
  expr: Constraints[4] = <<SteeringAckermannSpreadsheet>>.transferlinkagelength
  sketch-geometry (9):
    g0: Circle CenterX=0 CenterY=0 CenterZ=0 NormalX=0 NormalY=0 NormalZ=1 AngleXU=0 Radius=1.66
    g1: Circle CenterX=-32 CenterY=0 CenterZ=0 NormalX=0 NormalY=0 NormalZ=1 AngleXU=0 Radius=1.66
    g2: ArcOfCircle CenterX=0 CenterY=0 CenterZ=0 NormalX=0 NormalY=0 NormalZ=1 AngleXU=0 Radius=2.5 StartAngle=4.71239 EndAngle=7.85398
    g3: LineSegment StartX=8e-16 StartY=2.5 StartZ=0 EndX=-32 EndY=2.5 EndZ=0
    g4: LineSegment StartX=-5e-16 StartY=-2.5 StartZ=0 EndX=-15.88 EndY=-2.5 EndZ=0
    g5: ArcOfCircle CenterX=-32 CenterY=0 CenterZ=0 NormalX=0 NormalY=0 NormalZ=1 AngleXU=0 Radius=2.5 StartAngle=1.5708 EndAngle=5.01328
    g6: LineSegment StartX=-31.2591 StartY=-2.38768 StartZ=0 EndX=-26.1999 EndY=-0.817746 EndZ=0
    g7: ArcOfCircle CenterX=-25.9035 CenterY=-1.77282 CenterZ=0 NormalX=0 NormalY=0 NormalZ=1 AngleXU=0 Radius=1 StartAngle=1.39871 EndAngle=1.87169
    g8: LineSegment StartX=-25.7323 StartY=-0.787589 StartZ=0 EndX=-15.88 EndY=-2.5 EndZ=0
  constraints (21):
    c: Diameter(g0) = 3.32
    c: Coincident(g0,g-1)
    c: Diameter(g1) = 3.32
    c: PointOnObject(g1,g-1)
    c: DistanceX(g1,g0) = 32
    c: Coincident(g2,g0)
    c: Radius(g2) = 2.5
    c: Coincident(g5,g1)
    c: Tangent(g3,g2) = -1.5708
    c: Tangent(g4,g2) = 1.5708
    c: Tangent(g5,g3) = -1.5708
    c: Radius(g5) = 2.5
    c: Distance(g6,g6) = 5.29715
    c: Tangent(g6,g5) = -1.5708
    c: Radius(g7) = 1
    c: Tangent(g7,g6) = 1.5708
    c: Coincident(g8,g4)
    c: Distance(g8,g8) = 10
    c: Tangent(g8,g7) = 1.5708
    c: Parallel(g4,g3)
    c: DistanceX(g4,g4) = 15.88
FEATURE [App::Link] Link  label="SteeringAckermannSpreadsheet"
  LinkedObject = -> <external ../../Models/SteeringAckermannModel.FCStd>#Spreadsheet
FEATURE [PartDesign::Pad] Pad
  Direction = (0,0,1)
  Length = 2
  Length2 = 10
  Profile = -> Sketch
  ReferenceAxis = -> Sketch [N_Axis]
  Refine = true
  Suppressed = false
  Type = 0
FEATURE [PartDesign::Body] Body  label="TransferLinkageLeftBody"
  AllowCompound = false
  Group = -> [Sketch,Pad]
  Origin = -> Origin001
  Tip = -> Pad
FEATURE [App::Part] Part  label="TransferLinkageLeftPart"
  Group = -> [Body]
  Origin = -> Origin
---- part ../Parts/TransferLinkage/TransferLinkageRight.FCStd = doc fcstd_15382c82bdbc ----
FCSTD DOCUMENT  (FreeCAD 1.0R39285 (Git))
Label: TransferLinkageRight
License: All rights reserved
LicenseURL: https://en.wikipedia.org/wiki/All_rights_reserved
objects: PartDesign::SubShapeBinder×1, Part::Mirroring×1, App::Part×1
note: 2 computed .brp shape members not serialized (recipe doc carries the construction recipe); baked Part::Feature solids carry a one-line shape summary decoded from their .brp
EXTERNAL_REF file=TransferLinkageLeft.FCStd obj=Part

FEATURE [PartDesign::SubShapeBinder] Binder  label="TransferLinkageLeftBody"
  BindCopyOnChange = 0
  BindMode = 0
  ClaimChildren = false
  Context = -> Part [Binder.]
  Fuse = false
  MakeFace = true
  OffsetFill = false
  OffsetIntersection = false
  OffsetJoinType = 0
  OffsetOpenResult = false
  PartialLoad = false
  Refine = true
  Relative = true
  Support = -> [<external TransferLinkageLeft.FCStd>#Part[Body.]]
  _Version = 2
FEATURE [Part::Mirroring] Part__Mirroring  label="TransferLinkageRightBody"
  Base = (0,0,0)
  Normal = (1,0,0)
  Source = -> Binder
FEATURE [App::Part] Part  label="TransferLinkageRightPart"
  Group = -> [Binder,Part__Mirroring]
  Origin = -> Origin
---- part ../Parts/Wheel.FCStd = doc fcstd_22f719742fde ----
FCSTD DOCUMENT  (FreeCAD 1.0R39109 (Git))
Label: Wheel
License: All rights reserved
LicenseURL: https://en.wikipedia.org/wiki/All_rights_reserved
objects: Sketcher::SketchObject×5, PartDesign::Pad×4, PartDesign::Pocket×1, PartDesign::Body×1, App::Part×1
note: 26 computed .brp shape members not serialized (recipe doc carries the construction recipe); baked Part::Feature solids carry a one-line shape summary decoded from their .brp

FEATURE [Sketcher::SketchObject] Sketch
  ArcFitTolerance = 1e-06
  AttachmentSupport = -> [YZ_Plane001]
  FullyConstrained = true
  MakeInternals = false
  MapMode = 5
  Placement = pos=(0,0,0) rot=(0.57735,0.57735,0.57735;2.0944rad)
  sketch-geometry (2):
    g0: Circle CenterX=0 CenterY=0 CenterZ=0 NormalX=0 NormalY=0 NormalZ=1 AngleXU=0 Radius=17.5
    g1: Circle CenterX=0 CenterY=0 CenterZ=0 NormalX=0 NormalY=0 NormalZ=1 AngleXU=0 Radius=27.5
  constraints (4):
    c: Diameter(g0) = 35
    c: Coincident(g0,g-1)
    c: Coincident(g1,g0)
    c: Diameter(g1) = 55
FEATURE [PartDesign::Pad] Pad
  Direction = (1,0,0)
  Length = 25
  Length2 = 10
  Placement = pos=(0,0,0) rot=(1,1,1;2.0944rad)
  Profile = -> Sketch
  ReferenceAxis = -> Sketch [N_Axis]
  Refine = true
  Reversed = true
  Suppressed = false
  Type = 0
FEATURE [Sketcher::SketchObject] Sketch001
  ArcFitTolerance = 1e-06
  AttachmentSupport = -> [YZ_Plane001]
  FullyConstrained = true
  MakeInternals = false
  MapMode = 5
  Placement = pos=(0,0,0) rot=(0.57735,0.57735,0.57735;2.0944rad)
  sketch-geometry (9):
    g0: Circle CenterX=0 CenterY=0 CenterZ=0 NormalX=0 NormalY=0 NormalZ=1 AngleXU=0 Radius=17.5
    g1: Circle CenterX=0 CenterY=0 CenterZ=0 NormalX=0 NormalY=0 NormalZ=1 AngleXU=0 Radius=4.55
    g2: LineSegment [constr] StartX=0 StartY=10 StartZ=0 EndX=-8.66025 EndY=-5 EndZ=0
    g3: LineSegment [constr] StartX=-8.66025 StartY=-5 StartZ=0 EndX=8.66025 EndY=-5 EndZ=0
    g4: LineSegment [constr] StartX=8.66025 StartY=-5 StartZ=0 EndX=0 EndY=10 EndZ=0
    g5: Circle [constr] CenterX=0 CenterY=0 CenterZ=0 NormalX=0 NormalY=0 NormalZ=1 AngleXU=0 Radius=10
    g6: Circle CenterX=0 CenterY=10 CenterZ=0 NormalX=0 NormalY=0 NormalZ=1 AngleXU=0 Radius=1.5
    g7: Circle CenterX=-8.66025 CenterY=-5 CenterZ=0 NormalX=0 NormalY=0 NormalZ=1 AngleXU=0 Radius=1.5
    g8: Circle CenterX=8.66025 CenterY=-5 CenterZ=0 NormalX=0 NormalY=0 NormalZ=1 AngleXU=0 Radius=1.5
  constraints (21):
    c: Diameter(g0) = 35
    c: Coincident(g0,g-1)
    c: Diameter(g1) = 9.1
    c: Coincident(g1,g0)
    c: Coincident(g2,g3)
    c: Coincident(g3,g4)
    c: Coincident(g4,g2)
    c: Equal(g2,g3)
    c: Equal(g2,g4)
    c: PointOnObject(g2,g5)
    c: PointOnObject(g3,g5)
    c: PointOnObject(g4,g5)
    c: Coincident(g5,g0)
    c: PointOnObject(g4,g-2)
    c: Diameter(g6) = 3
    c: Coincident(g6,g2)
    c: Diameter(g7) = 3
    c: Coincident(g7,g2)
    c: Diameter(g8) = 3
    c: Coincident(g8,g3)
    c: DistanceY(g0,g2) = 10
FEATURE [PartDesign::Pad] Pad001
  BaseFeature = -> Pad
  Direction = (1,0,0)
  Length = 16
  Length2 = 10
  Placement = pos=(0,0,0) rot=(1,1,1;2.0944rad)
  Profile = -> Sketch001
  ReferenceAxis = -> Sketch001 [N_Axis]
  Refine = true
  Reversed = true
  Suppressed = false
  Type = 0
FEATURE [Sketcher::SketchObject] Sketch002
  ArcFitTolerance = 1e-06
  AttachmentSupport = -> [YZ_Plane001]
  FullyConstrained = true
  MakeInternals = false
  MapMode = 5
  Placement = pos=(0,0,0) rot=(0.57735,0.57735,0.57735;2.0944rad)
  sketch-geometry (1):
    g0: Circle CenterX=0 CenterY=0 CenterZ=0 NormalX=0 NormalY=0 NormalZ=1 AngleXU=0 Radius=17.5
  constraints (2):
    c: Diameter(g0) = 35
    c: Coincident(g0,g-1)
FEATURE [PartDesign::Pocket] Pocket
  BaseFeature = -> Pad001
  Direction = (-1,0,0)
  Length = 13
  Length2 = 5
  Placement = pos=(0,0,0) rot=(1,1,1;2.0944rad)
  Profile = -> Sketch002
  ReferenceAxis = -> Sketch002 [N_Axis]
  Refine = true
  Suppressed = false
  Type = 0
FEATURE [Sketcher::SketchObject] Sketch003
  ArcFitTolerance = 1e-06
  AttachmentSupport = -> [Pocket]
  FullyConstrained = true
  MakeInternals = false
  MapMode = 5
  Placement = pos=(-13,2.9e-15,-1.4e-15) rot=(0.57735,0.57735,0.57735;2.0944rad)
  sketch-geometry (2):
    g0: Circle CenterX=0 CenterY=0 CenterZ=0 NormalX=0 NormalY=0 NormalZ=1 AngleXU=0 Radius=4.55
    g1: Circle CenterX=0 CenterY=0 CenterZ=0 NormalX=0 NormalY=0 NormalZ=1 AngleXU=0 Radius=5.55
  constraints (4):
    c: Diameter(g0) = 9.1
    c: Coincident(g0,g-1)
    c: Coincident(g1,g0)
    c: Diameter(g1) = 11.1
FEATURE [PartDesign::Pad] Pad002
  BaseFeature = -> Pocket
  Direction = (1,0,0)
  Length = 2
  Length2 = 10
  Placement = pos=(0,0,0) rot=(1,1,1;2.0944rad)
  Profile = -> Sketch003
  ReferenceAxis = -> Sketch003 [N_Axis]
  Refine = true
  Suppressed = false
  Type = 0
FEATURE [Sketcher::SketchObject] Sketch004
  ArcFitTolerance = 1e-06
  AttachmentSupport = -> [Pad002]
  FullyConstrained = true
  MakeInternals = false
  MapMode = 5
  Placement = pos=(-16,1.07e-14,-5.3e-15) rot=(0.57735,0.57735,-0.57735;4.18879rad)
  sketch-geometry (2):
    g0: Circle CenterX=0 CenterY=0 CenterZ=0 NormalX=0 NormalY=0 NormalZ=1 AngleXU=0 Radius=4.55
    g1: Circle CenterX=0 CenterY=0 CenterZ=0 NormalX=0 NormalY=0 NormalZ=1 AngleXU=0 Radius=5.55
  constraints (4):
    c: Diameter(g0) = 9.1
    c: Coincident(g0,g-1)
    c: Diameter(g1) = 11.1
    c: Coincident(g1,g0)
FEATURE [PartDesign::Pad] Pad003
  BaseFeature = -> Pad002
  Direction = (-1,0,0)
  Length = 2
  Length2 = 10
  Placement = pos=(0,0,0) rot=(1,1,1;2.0944rad)
  Profile = -> Sketch004
  ReferenceAxis = -> Sketch004 [N_Axis]
  Refine = true
  Suppressed = false
  Type = 0
FEATURE [PartDesign::Body] Body  label="WheelBody"
  AllowCompound = false
  Group = -> [Sketch,Pad,Sketch001,Pad001,Sketch002,Pocket,Sketch003,Pad002,Sketch004,Pad003]
  Origin = -> Origin001
  Tip = -> Pad003
FEATURE [App::Part] Part  label="WheelPart"
  Group = -> [Body]
  Origin = -> Origin
---- part ../Parts/WheelLinkage/WheelLinkageBottomLeft.FCStd = doc fcstd_a23c7c7aa2b5 ----
FCSTD DOCUMENT  (FreeCAD 1.0R39285 (Git))
Label: WheelLinkageBottomLeft
License: All rights reserved
LicenseURL: https://en.wikipedia.org/wiki/All_rights_reserved
objects: Sketcher::SketchObject×4, PartDesign::Pad×4, App::Link×1, PartDesign::Body×1, App::Part×1
note: 21 computed .brp shape members not serialized (recipe doc carries the construction recipe); baked Part::Feature solids carry a one-line shape summary decoded from their .brp
EXTERNAL_REF file=../../Models/SteeringAckermannModel.FCStd obj=Spreadsheet

FEATURE [App::Link] Link  label="SteeringAckermannSpreadsheet"
  LinkedObject = -> <external ../../Models/SteeringAckermannModel.FCStd>#Spreadsheet
FEATURE [Sketcher::SketchObject] Sketch
  ArcFitTolerance = 1e-06
  AttachmentSupport = -> [XY_Plane001]
  FullyConstrained = true
  MakeInternals = false
  MapMode = 5
  expr: Constraints[1] = <<SteeringAckermannSpreadsheet>>.wheellinkagelength
  expr: Constraints[2] = <<SteeringAckermannSpreadsheet>>.wheellinkageangle
  sketch-geometry (9):
    g0: LineSegment [constr] StartX=0 StartY=0 StartZ=0 EndX=-2.70757 EndY=-11.6906 EndZ=0
    g1: ArcOfCircle CenterX=0 CenterY=0 CenterZ=0 NormalX=0 NormalY=0 NormalZ=1 AngleXU=0 Radius=4 StartAngle=5.97216 EndAngle=7.85398
    g2: ArcOfCircle CenterX=-2.70757 CenterY=-11.6906 CenterZ=0 NormalX=0 NormalY=0 NormalZ=1 AngleXU=0 Radius=3 StartAngle=3.3952 EndAngle=5.97216
    g3: LineSegment StartX=3.80809 StartY=-1.22412 StartZ=0 EndX=0.14849 EndY=-12.6086 EndZ=0
    g4: LineSegment StartX=-5.61162 StartY=-12.4432 StartZ=0 EndX=-7.8 EndY=-4 EndZ=0
    g5: LineSegment StartX=-7.8 StartY=-4 StartZ=0 EndX=-7.8 EndY=4 EndZ=0
    g6: LineSegment StartX=-7.8 StartY=4 StartZ=0 EndX=9e-16 EndY=4 EndZ=0
    g7: LineSegment [constr] StartX=0 StartY=0 StartZ=0 EndX=-5 EndY=0 EndZ=0
    g8: Circle CenterX=0 CenterY=0 CenterZ=0 NormalX=0 NormalY=0 NormalZ=1 AngleXU=0 Radius=1.62
  constraints (22):
    c: Coincident(g0,g-1)
    c: Distance(g0,g0) = 12
    c: Angle(g-1,g0) = 1.34321
    c: Coincident(g1,g0)
    c: Coincident(g2,g0)
    c: Coincident(g5,g4)
    c: Vertical(g5)
    c: Coincident(g6,g5)
    c: Tangent(g3,g1) = 1.5708
    c: Tangent(g3,g2) = 1.5708
    c: Tangent(g4,g2) = 1.5708
    c: Tangent(g6,g1) = 1.5708
    c: Horizontal(g6)
    c: Radius(g1) = 4
    c: Radius(g2) = 3
    c: DistanceY(g5,g5) = 8
    c: Coincident(g7,g0)
    c: PointOnObject(g7,g-1)
    c: DistanceX(g7,g7) = 5
    c: Distance(g7,g5) = 2.8
    c: Diameter(g8) = 3.24
    c: Coincident(g8,g0)
FEATURE [PartDesign::Pad] Pad
  Direction = (0,0,1)
  Length = 2
  Length2 = 10
  Profile = -> Sketch
  ReferenceAxis = -> Sketch [N_Axis]
  Refine = true
  Suppressed = false
  Type = 0
FEATURE [Sketcher::SketchObject] Sketch001
  ArcFitTolerance = 1e-06
  AttachmentSupport = -> [Pad]
  ExternalGeometry = -> [Sketch]
  FullyConstrained = true
  MakeInternals = false
  MapMode = 5
  Placement = pos=(0,0,2) rot=(0,0,1;0rad)
  sketch-geometry (1):
    g0: Circle CenterX=-2.70757 CenterY=-11.6906 CenterZ=0 NormalX=0 NormalY=0 NormalZ=1 AngleXU=0 Radius=2.5
  constraints (2):
    c: Coincident(g0,g-3)
    c: Diameter(g0) = 5
FEATURE [PartDesign::Pad] Pad001
  BaseFeature = -> Pad
  Direction = (0,0,1)
  Length = 0.5
  Length2 = 10
  Profile = -> Sketch001
  ReferenceAxis = -> Sketch001 [N_Axis]
  Refine = true
  Suppressed = false
  Type = 0
FEATURE [Sketcher::SketchObject] Sketch002
  ArcFitTolerance = 1e-06
  AttachmentSupport = -> [Pad001]
  ExternalGeometry = -> [Sketch001]
  FullyConstrained = true
  MakeInternals = false
  MapMode = 5
  Placement = pos=(0,0,2.5) rot=(0,0,1;0rad)
  sketch-geometry (1):
    g0: Circle CenterX=-2.70757 CenterY=-11.6906 CenterZ=0 NormalX=0 NormalY=0 NormalZ=1 AngleXU=0 Radius=1.5
  constraints (2):
    c: Diameter(g0) = 3
    c: Coincident(g0,g-3)
FEATURE [PartDesign::Pad] Pad002
  BaseFeature = -> Pad001
  Direction = (0,0,1)
  Length = 4.5
  Length2 = 10
  Profile = -> Sketch002
  ReferenceAxis = -> Sketch002 [N_Axis]
  Refine = true
  Suppressed = false
  Type = 0
FEATURE [Sketcher::SketchObject] Sketch003
  ArcFitTolerance = 1e-06
  AttachmentSupport = -> [Pad002]
  ExternalGeometry = -> [Sketch]
  FullyConstrained = true
  MakeInternals = false
  MapMode = 5
  Placement = pos=(0,0,2) rot=(0,0,1;0rad)
  sketch-geometry (2):
    g0: LineSegment [constr] StartX=0 StartY=0 StartZ=0 EndX=-5 EndY=0 EndZ=0
    g1: Circle CenterX=-5 CenterY=0 CenterZ=0 NormalX=0 NormalY=0 NormalZ=1 AngleXU=0 Radius=1.5
  constraints (5):
    c: Coincident(g0,g-1)
    c: PointOnObject(g0,g-1)
    c: DistanceX(g0,g0) = 5
    c: Diameter(g1) = 3
    c: Coincident(g1,g0)
FEATURE [PartDesign::Pad] Pad003
  BaseFeature = -> Pad002
  Direction = (0,0,1)
  Length = 5
  Length2 = 10
  Profile = -> Sketch003
  ReferenceAxis = -> Sketch003 [N_Axis]
  Refine = true
  Suppressed = false
  Type = 0
FEATURE [PartDesign::Body] Body  label="WheelLinkageBottomBody"
  AllowCompound = false
  Group = -> [Sketch,Pad,Sketch001,Pad001,Sketch002,Pad002,Sketch003,Pad003]
  Origin = -> Origin001
  Tip = -> Pad003
FEATURE [App::Part] Part  label="WheelLinkageBottomLeftPart"
  Group = -> [Body]
  Origin = -> Origin
---- part ../Parts/WheelLinkage/WheelLinkageBottomRight.FCStd = doc fcstd_f47131f818aa ----
FCSTD DOCUMENT  (FreeCAD 1.0R39285 (Git))
Label: WheelLinkageBottomRight
License: All rights reserved
LicenseURL: https://en.wikipedia.org/wiki/All_rights_reserved
objects: PartDesign::SubShapeBinder×1, Part::Mirroring×1, App::Part×1
note: 2 computed .brp shape members not serialized (recipe doc carries the construction recipe); baked Part::Feature solids carry a one-line shape summary decoded from their .brp
EXTERNAL_REF file=WheelLinkageBottomLeft.FCStd obj=Part

FEATURE [PartDesign::SubShapeBinder] Binder  label="WheelLinkageBottomLeftBody"
  BindCopyOnChange = 0
  BindMode = 0
  ClaimChildren = false
  Context = -> Part [Binder.]
  Fuse = false
  MakeFace = true
  OffsetFill = false
  OffsetIntersection = false
  OffsetJoinType = 0
  OffsetOpenResult = false
  PartialLoad = false
  Refine = true
  Relative = true
  Support = -> [<external WheelLinkageBottomLeft.FCStd>#Part[Body.]]
  _Version = 2
FEATURE [Part::Mirroring] Part__Mirroring  label="WheelLinkageBottomRightBody"
  Base = (0,0,0)
  Normal = (1,0,0)
  Source = -> Binder
FEATURE [App::Part] Part  label="WheelLinkageBottomRightPart"
  Group = -> [Binder,Part__Mirroring]
  Origin = -> Origin
---- part ../Parts/WheelLinkage/WheelLinkageTopRight.FCStd = doc fcstd_321a71ae4978 ----
FCSTD DOCUMENT  (FreeCAD 1.0R39285 (Git))
Label: WheelLinkageTopRight
License: All rights reserved
LicenseURL: https://en.wikipedia.org/wiki/All_rights_reserved
objects: PartDesign::SubShapeBinder×1, Part::Mirroring×1, App::Part×1
note: 2 computed .brp shape members not serialized (recipe doc carries the construction recipe); baked Part::Feature solids carry a one-line shape summary decoded from their .brp
EXTERNAL_REF file=WheelLinkageTopLeft.FCStd obj=Part

FEATURE [PartDesign::SubShapeBinder] Binder  label="WheelLinkageTopLeftBody"
  BindCopyOnChange = 0
  BindMode = 0
  ClaimChildren = false
  Context = -> Part [Binder.]
  Fuse = false
  MakeFace = true
  OffsetFill = false
  OffsetIntersection = false
  OffsetJoinType = 0
  OffsetOpenResult = false
  PartialLoad = false
  Refine = true
  Relative = true
  Support = -> [<external WheelLinkageTopLeft.FCStd>#Part[Body.]]
  _Version = 2
FEATURE [Part::Mirroring] Part__Mirroring  label="WheelLinkageTopRightBody"
  Base = (0,0,0)
  Normal = (1,0,0)
  Source = -> Binder
FEATURE [App::Part] Part  label="WheelLinkageTopRightPart"
  Group = -> [Binder,Part__Mirroring]
  Origin = -> Origin
---- part FrontAssembly.FCStd = doc fcstd_d4ffce4d0b61 ----
FCSTD DOCUMENT  (FreeCAD 1.0R39319 (Git))
Label: FrontAssembly
License: All rights reserved
LicenseURL: https://en.wikipedia.org/wiki/All_rights_reserved
objects: App::FeaturePython×19, App::Link×17, Assembly::JointGroup×1, Assembly::AssemblyObject×1
EXTERNAL_REF file=../Parts/FrontCover.FCStd obj=Part
EXTERNAL_REF file=../Parts/WheelLinkage/WheelLinkageTopLeft.FCStd obj=Body
EXTERNAL_REF file=../Parts/WheelLinkage/WheelLinkageBottomLeft.FCStd obj=Part
EXTERNAL_REF file=../Parts/WheelLinkage/WheelLinkageTopRight.FCStd obj=Part
EXTERNAL_REF file=../Parts/WheelLinkage/WheelLinkageBottomRight.FCStd obj=Part
EXTERNAL_REF file=../Parts/FrontWheelAxle/FrontWheelAxleLeft.FCStd obj=Part
EXTERNAL_REF file=../Parts/FrontWheelAxle/FrontWheelAxleRight.FCStd obj=Part
EXTERNAL_REF file=../Parts/S0004m.FCStd obj=Part
EXTERNAL_REF file=../Parts/TBoneLinkage/TBoneLinkageTop.FCStd obj=Part
EXTERNAL_REF file=../Parts/TBoneLinkage/TBoneLinkageBottom.FCStd obj=Part
EXTERNAL_REF file=../Parts/TransferLinkage/TransferLinkageLeft.FCStd obj=Part
EXTERNAL_REF file=../Parts/TransferLinkage/TransferLinkageRight.FCStd obj=Part
EXTERNAL_REF file=../Parts/FrontWheelStopper.FCStd obj=Part
EXTERNAL_REF file=../Parts/Wheel.FCStd obj=Part
EXTERNAL_REF file=../Parts/RpiCamera.FCStd obj=rpiCameraMAssembly

FEATURE [App::Link] FrontCoverPart
  LinkedObject = -> <external ../Parts/FrontCover.FCStd>#Part
FEATURE [App::FeaturePython] GroundedJoint  # Assembly grounded joint (typed FeaturePython)
  ObjectToGround = -> FrontCoverPart
FEATURE [App::Link] WheelLinkageTopLeftBody
  LinkPlacement = pos=(-34,-2e-16,0) rot=(0,0,1;0.017527rad)
  LinkedObject = -> <external ../Parts/WheelLinkage/WheelLinkageTopLeft.FCStd>#Body
  Placement = pos=(-34,-2e-16,0) rot=(0,0,1;0.017527rad)
FEATURE [App::FeaturePython] Joint  label="Revolute"  # Assembly joint (typed FeaturePython)
  Activated = true
  AngleMax = 0
  AngleMin = 0
  Detach1 = false
  Detach2 = false
  Distance = 0
  Distance2 = 0
  EnableAngleMax = false
  EnableAngleMin = false
  EnableLengthMax = false
  EnableLengthMin = false
  JointType = 1 (Revolute)
  LengthMax = 0
  LengthMin = 0
  Placement2 = pos=(-34,-2e-16,0) rot=(0,0,1;0rad)
  Reference1 = -> Assembly [WheelLinkageTopLeftBody.Edge16,WheelLinkageTopLeftBody.Edge16]
  Reference2 = -> Assembly [FrontCoverPart.Body.Edge88,FrontCoverPart.Body.Edge88]
FEATURE [App::Link] WheelLinkageBottomLeftPart
  LinkPlacement = pos=(-34,-2e-16,-7) rot=(0,0,1;0.017527rad)
  LinkedObject = -> <external ../Parts/WheelLinkage/WheelLinkageBottomLeft.FCStd>#Part
  Placement = pos=(-34,-2e-16,-7) rot=(0,0,1;0.017527rad)
FEATURE [App::FeaturePython] Joint001  label="Fixed"  # Assembly joint (typed FeaturePython)
  Activated = true
  AngleMax = 0
  AngleMin = 0
  Detach1 = false
  Detach2 = false
  Distance = 0
  Distance2 = 0
  EnableAngleMax = false
  EnableAngleMin = false
  EnableLengthMax = false
  EnableLengthMin = false
  JointType = 0 (Fixed)
  LengthMax = 0
  LengthMin = 0
  Placement1 = pos=(-5,0,7) rot=(0,0,1;0rad)
  Placement2 = pos=(-5,0,0) rot=(1,0,0;3.14159rad)
  Reference1 = -> Assembly [WheelLinkageBottomLeftPart.Body.Edge27,WheelLinkageBottomLeftPart.Body.Edge27]
  Reference2 = -> Assembly [WheelLinkageTopLeftBody.Edge15,WheelLinkageTopLeftBody.Edge15]
FEATURE [App::Link] WheelLinkageTopRightPart
  LinkPlacement = pos=(34,0,0) rot=(0,0,1;0.017627rad)
  LinkedObject = -> <external ../Parts/WheelLinkage/WheelLinkageTopRight.FCStd>#Part
  Placement = pos=(34,0,0) rot=(0,0,1;0.017627rad)
FEATURE [App::FeaturePython] Joint002  label="Revolute001"  # Assembly joint (typed FeaturePython)
  Activated = true
  AngleMax = 0
  AngleMin = 0
  Detach1 = false
  Detach2 = false
  Distance = 0
  Distance2 = 0
  EnableAngleMax = false
  EnableAngleMin = false
  EnableLengthMax = false
  EnableLengthMin = false
  JointType = 1 (Revolute)
  LengthMax = 0
  LengthMin = 0
  Placement1 = pos=(0,0,0) rot=(0,1,0;3.14159rad)
  Placement2 = pos=(34,0,0) rot=(0,0,1;0rad)
  Reference1 = -> Assembly [WheelLinkageTopRightPart.Part__Mirroring.Edge16,WheelLinkageTopRightPart.Part__Mirroring.Edge16]
  Reference2 = -> Assembly [FrontCoverPart.Body.Edge94,FrontCoverPart.Body.Edge94]
FEATURE [App::Link] WheelLinkageBottomRightPart
  LinkPlacement = pos=(34,0,-7) rot=(0,0,1;0.017627rad)
  LinkedObject = -> <external ../Parts/WheelLinkage/WheelLinkageBottomRight.FCStd>#Part
  Placement = pos=(34,0,-7) rot=(0,0,1;0.017627rad)
FEATURE [App::FeaturePython] Joint003  label="Fixed001"  # Assembly joint (typed FeaturePython)
  Activated = true
  AngleMax = 0
  AngleMin = 0
  Detach1 = false
  Detach2 = false
  Distance = 0
  Distance2 = 0
  EnableAngleMax = false
  EnableAngleMin = false
  EnableLengthMax = false
  EnableLengthMin = false
  JointType = 0 (Fixed)
  LengthMax = 0
  LengthMin = 0
  Placement1 = pos=(5,0,7) rot=(0,1,0;3.14159rad)
  Placement2 = pos=(5,0,0) rot=(0,0,1;3.14159rad)
  Reference1 = -> Assembly [WheelLinkageBottomRightPart.Part__Mirroring.Edge27,WheelLinkageBottomRightPart.Part__Mirroring.Edge27]
  Reference2 = -> Assembly [WheelLinkageTopRightPart.Part__Mirroring.Edge15,WheelLinkageTopRightPart.Part__Mirroring.Edge15]
FEATURE [App::Link] FrontWheelAxleLeftPart
  LinkPlacement = pos=(-31.0005,0.0525794,-3.5) rot=(0,0,1;0.017527rad)
  LinkedObject = -> <external ../Parts/FrontWheelAxle/FrontWheelAxleLeft.FCStd>#Part
  Placement = pos=(-31.0005,0.0525794,-3.5) rot=(0,0,1;0.017527rad)
FEATURE [App::FeaturePython] Joint004  label="Fixed002"  # Assembly joint (typed FeaturePython)
  Activated = true
  AngleMax = 0
  AngleMin = 0
  Detach1 = false
  Detach2 = false
  Distance = 0
  Distance2 = 0
  EnableAngleMax = false
  EnableAngleMin = false
  EnableLengthMax = false
  EnableLengthMin = false
  JointType = 0 (Fixed)
  LengthMax = 0
  LengthMin = 0
  Offset2 = pos=(0,0,0) rot=(0,0,-1;1.5708rad)
  Placement1 = pos=(-3,-2e-16,1.5) rot=(0,0,-1;1.5708rad)
  Placement2 = pos=(0,0,-2) rot=(0,0,-1;1.5708rad)
  Reference1 = -> Assembly [FrontWheelAxleLeftPart.Body.Edge27,FrontWheelAxleLeftPart.Body.Edge27]
  Reference2 = -> Assembly [WheelLinkageTopLeftBody.Edge22,WheelLinkageTopLeftBody.Edge22]
FEATURE [App::Link] FrontWheelAxleRightPart
  LinkPlacement = pos=(31.0005,-0.0528788,-3.5) rot=(0,0,1;0.017627rad)
  LinkedObject = -> <external ../Parts/FrontWheelAxle/FrontWheelAxleRight.FCStd>#Part
  Placement = pos=(31.0005,-0.0528788,-3.5) rot=(0,0,1;0.017627rad)
FEATURE [App::FeaturePython] Joint005  label="Fixed003"  # Assembly joint (typed FeaturePython)
  Activated = true
  AngleMax = 0
  AngleMin = 0
  Detach1 = false
  Detach2 = false
  Distance = 0
  Distance2 = 0
  EnableAngleMax = false
  EnableAngleMin = false
  EnableLengthMax = false
  EnableLengthMin = false
  JointType = 0 (Fixed)
  LengthMax = 0
  LengthMin = 0
  Offset2 = pos=(0,0,0) rot=(0,0,-1;1.5708rad)
  Placement1 = pos=(3,-2e-16,1.5) rot=(-0.707107,0.707107,0;3.14159rad)
  Placement2 = pos=(0,0,-2) rot=(-0.707107,0.707107,0;3.14159rad)
  Reference1 = -> Assembly [FrontWheelAxleRightPart.Part__Mirroring.Edge27,FrontWheelAxleRightPart.Part__Mirroring.Edge27]
  Reference2 = -> Assembly [WheelLinkageTopRightPart.Part__Mirroring.Edge22,WheelLinkageTopRightPart.Part__Mirroring.Edge22]
FEATURE [App::Link] S0004mPart
  LinkPlacement = pos=(0,-9.55,24.5) rot=(1,0,0;3.14159rad)
  LinkedObject = -> <external ../Parts/S0004m.FCStd>#Part
  Placement = pos=(0,-9.55,24.5) rot=(1,0,0;3.14159rad)
FEATURE [App::Link] TBoneLinkageTopPart
  LinkPlacement = pos=(0,-4,1e-16) rot=(0,0,1;0.016716rad)
  LinkedObject = -> <external ../Parts/TBoneLinkage/TBoneLinkageTop.FCStd>#Part
  Placement = pos=(0,-4,1e-16) rot=(0,0,1;0.016716rad)
FEATURE [App::Link] TBoneLinkageBottomPart
  LinkPlacement = pos=(2e-16,-4,-7) rot=(0,0,1;0.016716rad)
  LinkedObject = -> <external ../Parts/TBoneLinkage/TBoneLinkageBottom.FCStd>#Part
  Placement = pos=(2e-16,-4,-7) rot=(0,0,1;0.016716rad)
FEATURE [App::FeaturePython] Joint007  label="Revolute002"  # Assembly joint (typed FeaturePython)
  Activated = true
  AngleMax = 0
  AngleMin = 0
  Detach1 = false
  Detach2 = false
  Distance = 0
  Distance2 = 0
  EnableAngleMax = false
  EnableAngleMin = false
  EnableLengthMax = false
  EnableLengthMin = false
  JointType = 1 (Revolute)
  LengthMax = 0
  LengthMin = 0
  Placement1 = pos=(0,0,-2) rot=(0,0,1;0rad)
  Placement2 = pos=(0,-5.55,26.5) rot=(0,0,1;0rad)
  Reference1 = -> Assembly [TBoneLinkageTopPart.Body.Edge22,TBoneLinkageTopPart.Body.Edge22]
  Reference2 = -> Assembly [S0004mPart.Body.Edge51,S0004mPart.Body.Edge51]
FEATURE [App::FeaturePython] Joint008  label="Fixed005"  # Assembly joint (typed FeaturePython)
  Activated = true
  AngleMax = 0
  AngleMin = 0
  Detach1 = false
  Detach2 = false
  Distance = 0
  Distance2 = 0
  EnableAngleMax = false
  EnableAngleMin = false
  EnableLengthMax = false
  EnableLengthMin = false
  JointType = 0 (Fixed)
  LengthMax = 0
  LengthMin = 0
  Placement1 = pos=(-5,-12,7) rot=(0,0,1;0rad)
  Placement2 = pos=(-5,-12,0) rot=(0,0,1;0rad)
  Reference1 = -> Assembly [TBoneLinkageBottomPart.Body.Edge43,TBoneLinkageBottomPart.Body.Edge43]
  Reference2 = -> Assembly [TBoneLinkageTopPart.Body.Edge16,TBoneLinkageTopPart.Body.Edge16]
FEATURE [App::Link] TransferLinkageLeftPart
  LinkPlacement = pos=(-4.79872,-16.0819,-4.5) rot=(0,0,-1;0.136224rad)
  LinkedObject = -> <external ../Parts/TransferLinkage/TransferLinkageLeft.FCStd>#Part
  Placement = pos=(-4.79872,-16.0819,-4.5) rot=(0,0,-1;0.136224rad)
FEATURE [App::Link] TransferLinkageRightPart
  LinkPlacement = pos=(5.19989,-15.9147,-4.5) rot=(0,0,1;0.133954rad)
  LinkedObject = -> <external ../Parts/TransferLinkage/TransferLinkageRight.FCStd>#Part
  Placement = pos=(5.19989,-15.9147,-4.5) rot=(0,0,1;0.133954rad)
FEATURE [App::FeaturePython] Joint009  label="Revolute003"  # Assembly joint (typed FeaturePython)
  Activated = true
  AngleMax = 0
  AngleMin = 0
  Detach1 = false
  Detach2 = false
  Distance = 0
  Distance2 = 0
  EnableAngleMax = false
  EnableAngleMin = false
  EnableLengthMax = false
  EnableLengthMin = false
  JointType = 1 (Revolute)
  LengthMax = 0
  LengthMin = 0
  Placement1 = pos=(0,0,2) rot=(0,0,1;0rad)
  Placement2 = pos=(-5,-12,-2.5) rot=(1,0,0;3.14159rad)
  Reference1 = -> Assembly [TransferLinkageLeftPart.Body.Edge24,TransferLinkageLeftPart.Body.Edge24]
  Reference2 = -> Assembly [TBoneLinkageTopPart.Body.Edge30,TBoneLinkageTopPart.Body.Edge30]
FEATURE [App::FeaturePython] Joint010  label="Cylindrical"  # Assembly joint (typed FeaturePython)
  Activated = true
  AngleMax = 0
  AngleMin = 0
  Detach1 = false
  Detach2 = false
  Distance = 0
  Distance2 = 0
  EnableAngleMax = false
  EnableAngleMin = false
  EnableLengthMax = false
  EnableLengthMin = false
  JointType = 2 (Cylindrical)
  LengthMax = 0
  LengthMin = 0
  Placement1 = pos=(-32,0,2) rot=(0,0,1;0rad)
  Placement2 = pos=(-2.70757,-11.6906,-2.5) rot=(1,0,0;3.14159rad)
  Reference1 = -> Assembly [TransferLinkageLeftPart.Body.Edge27,TransferLinkageLeftPart.Body.Edge27]
  Reference2 = -> Assembly [WheelLinkageTopLeftBody.Edge26,WheelLinkageTopLeftBody.Edge26]
FEATURE [App::FeaturePython] Joint011  label="Revolute004"  # Assembly joint (typed FeaturePython)
  Activated = true
  AngleMax = 0
  AngleMin = 0
  Detach1 = false
  Detach2 = false
  Distance = 0
  Distance2 = 0
  EnableAngleMax = false
  EnableAngleMin = false
  EnableLengthMax = false
  EnableLengthMin = false
  JointType = 1 (Revolute)
  LengthMax = 0
  LengthMin = 0
  Placement1 = pos=(0,0,2) rot=(0,1,0;3.14159rad)
  Placement2 = pos=(5,-12,-2.5) rot=(1,0,0;3.14159rad)
  Reference1 = -> Assembly [TransferLinkageRightPart.Part__Mirroring.Edge24,TransferLinkageRightPart.Part__Mirroring.Edge24]
  Reference2 = -> Assembly [TBoneLinkageTopPart.Body.Edge31,TBoneLinkageTopPart.Body.Edge31]
FEATURE [App::FeaturePython] Joint012  label="Cylindrical001"  # Assembly joint (typed FeaturePython)
  Activated = true
  AngleMax = 0
  AngleMin = 0
  Detach1 = false
  Detach2 = false
  Distance = 0
  Distance2 = 0
  EnableAngleMax = false
  EnableAngleMin = false
  EnableLengthMax = false
  EnableLengthMin = false
  JointType = 2 (Cylindrical)
  LengthMax = 0
  LengthMin = 0
  Placement1 = pos=(32,0,2) rot=(0,1,0;3.14159rad)
  Placement2 = pos=(2.70757,-11.6906,-2.5) rot=(0,0,1;3.14159rad)
  Reference1 = -> Assembly [TransferLinkageRightPart.Part__Mirroring.Edge27,TransferLinkageRightPart.Part__Mirroring.Edge27]
  Reference2 = -> Assembly [WheelLinkageTopRightPart.Part__Mirroring.Edge26,WheelLinkageTopRightPart.Part__Mirroring.Edge26]
FEATURE [App::Link] FrontWheelStopperPart
  LinkPlacement = pos=(-42.9986,-0.157738,-3.5) rot=(0,0,1;0.017527rad)
  LinkedObject = -> <external ../Parts/FrontWheelStopper.FCStd>#Part
  Placement = pos=(-42.9986,-0.157738,-3.5) rot=(0,0,1;0.017527rad)
FEATURE [App::Link] FrontWheelStopperPart001
  LinkPlacement = pos=(42.9986,0.158636,-3.5) rot=(0,0,1;3.15922rad)
  LinkedObject = -> <external ../Parts/FrontWheelStopper.FCStd>#Part
  Placement = pos=(42.9986,0.158636,-3.5) rot=(0,0,1;3.15922rad)
FEATURE [App::FeaturePython] Joint013  label="Fixed006"  # Assembly joint (typed FeaturePython)
  Activated = true
  AngleMax = 0
  AngleMin = 0
  Detach1 = false
  Detach2 = false
  Distance = 0
  Distance2 = 0
  EnableAngleMax = false
  EnableAngleMin = false
  EnableLengthMax = false
  EnableLengthMin = false
  JointType = 0 (Fixed)
  LengthMax = 0
  LengthMin = 0
  Placement1 = pos=(-2,-2e-16,1.8e-15) rot=(0.57735,0.57735,0.57735;2.0944rad)
  Placement2 = pos=(-14,3e-15,7.1e-15) rot=(0.57735,0.57735,-0.57735;4.18879rad)
  Reference1 = -> Assembly [FrontWheelStopperPart.Body.Edge22,FrontWheelStopperPart.Body.Edge22]
  Reference2 = -> Assembly [FrontWheelAxleLeftPart.Body.Edge20,FrontWheelAxleLeftPart.Body.Edge20]
FEATURE [App::Link] WheelPart
  LinkPlacement = pos=(-35.9997,-0.035053,-3.5) rot=(0,0,1;0.017527rad)
  LinkedObject = -> <external ../Parts/Wheel.FCStd>#Part
  Placement = pos=(-35.9997,-0.035053,-3.5) rot=(0,0,1;0.017527rad)
FEATURE [App::Link] WheelPart001
  LinkPlacement = pos=(35.9997,0.0352525,-3.5) rot=(0,0,1;3.15922rad)
  LinkedObject = -> <external ../Parts/Wheel.FCStd>#Part
  Placement = pos=(35.9997,0.0352525,-3.5) rot=(0,0,1;3.15922rad)
FEATURE [App::FeaturePython] Joint014  label="Fixed007"  # Assembly joint (typed FeaturePython)
  Activated = true
  AngleMax = 0
  AngleMin = 0
  Detach1 = false
  Detach2 = false
  Distance = 0
  Distance2 = 0
  EnableAngleMax = false
  EnableAngleMin = false
  EnableLengthMax = false
  EnableLengthMin = false
  JointType = 0 (Fixed)
  LengthMax = 0
  LengthMin = 0
  Offset2 = pos=(0,0,0) rot=(0,0,1;3.14159rad)
  Placement1 = pos=(-2,-2e-16,1.8e-15) rot=(0.57735,0.57735,0.57735;2.0944rad)
  Placement2 = pos=(14,8.7e-15,3e-16) rot=(-0.57735,0.57735,0.57735;4.18879rad)
  Reference1 = -> Assembly [FrontWheelStopperPart001.Body.Edge22,FrontWheelStopperPart001.Body.Edge22]
  Reference2 = -> Assembly [FrontWheelAxleRightPart.Part__Mirroring.Edge6,FrontWheelAxleRightPart.Part__Mirroring.Edge6]
FEATURE [App::FeaturePython] Joint015  label="Fixed008"  # Assembly joint (typed FeaturePython)
  Activated = true
  AngleMax = 0
  AngleMin = 0
  Detach1 = false
  Detach2 = false
  Distance = 0
  Distance2 = 0
  EnableAngleMax = false
  EnableAngleMin = false
  EnableLengthMax = false
  EnableLengthMin = false
  JointType = 0 (Fixed)
  LengthMax = 0
  LengthMin = 0
  Placement1 = pos=(-11,7.8e-15,-3.9e-15) rot=(0.57735,0.57735,0.57735;2.0944rad)
  Placement2 = pos=(-16,4e-15,7.1e-15) rot=(0.57735,0.57735,-0.57735;4.18879rad)
  Reference1 = -> Assembly [WheelPart.Body.Edge25,WheelPart.Body.Edge25]
  Reference2 = -> Assembly [FrontWheelAxleLeftPart.Body.Edge33,FrontWheelAxleLeftPart.Body.Edge33]
FEATURE [App::FeaturePython] Joint016  label="Fixed009"  # Assembly joint (typed FeaturePython)
  Activated = true
  AngleMax = 0
  AngleMin = 0
  Detach1 = false
  Detach2 = false
  Distance = 0
  Distance2 = 0
  EnableAngleMax = false
  EnableAngleMin = false
  EnableLengthMax = false
  EnableLengthMin = false
  JointType = 0 (Fixed)
  LengthMax = 0
  LengthMin = 0
  Offset2 = pos=(0,0,0) rot=(0,0,1;3.14159rad)
  Placement1 = pos=(-11,7.8e-15,-3.9e-15) rot=(0.57735,0.57735,0.57735;2.0944rad)
  Placement2 = pos=(16,4e-15,7.1e-15) rot=(-0.57735,0.57735,0.57735;4.18879rad)
  Reference1 = -> Assembly [WheelPart001.Body.Edge25,WheelPart001.Body.Edge25]
  Reference2 = -> Assembly [FrontWheelAxleRightPart.Part__Mirroring.Edge33,FrontWheelAxleRightPart.Part__Mirroring.Edge33]
FEATURE [App::Link] RpiCameraPart
  LinkPlacement = pos=(-3.5e-15,11.25,15.75) rot=(0,0,1;0rad)
  LinkedObject = -> <external ../Parts/RpiCamera.FCStd>#rpiCameraMAssembly
  Placement = pos=(-3.5e-15,11.25,15.75) rot=(0,0,1;0rad)
FEATURE [App::FeaturePython] Joint017  label="Fixed010"  # Assembly joint (typed FeaturePython)
  Activated = true
  AngleMax = 0
  AngleMin = 0
  Detach1 = false
  Detach2 = false
  Distance = 0
  Distance2 = 0
  EnableAngleMax = false
  EnableAngleMin = false
  EnableLengthMax = false
  EnableLengthMin = false
  JointType = 0 (Fixed)
  LengthMax = 0
  LengthMin = 0
  Offset2 = pos=(0,0,1.7) rot=(0,0,-1;1.5708rad)
  Placement1 = pos=(10.25,0.1,3.75) rot=(-0.57735,0.57735,0.57735;2.0944rad)
  Placement2 = pos=(10.25,11.35,19.5) rot=(-0.57735,0.57735,0.57735;2.0944rad)
  Reference1 = -> Assembly [RpiCameraPart.Part__Feature.Edge767,RpiCameraPart.Part__Feature.Edge767]
  Reference2 = -> Assembly [FrontCoverPart.Body.Edge102,FrontCoverPart.Body.Edge102]
FEATURE [App::FeaturePython] Joint018  label="Fixed011"  # Assembly joint (typed FeaturePython)
  Activated = true
  AngleMax = 0
  AngleMin = 0
  Detach1 = false
  Detach2 = false
  Distance = 0
  Distance2 = 0
  EnableAngleMax = false
  EnableAngleMin = false
  EnableLengthMax = false
  EnableLengthMin = false
  JointType = 0 (Fixed)
  LengthMax = 0
  LengthMin = 0
  Placement1 = pos=(0,-21.35,8.5) rot=(0,0,1;0rad)
  Placement2 = pos=(0,11.8,16) rot=(0,0,1;0rad)
  Reference1 = -> Assembly [FrontCoverPart.Body.Edge133,FrontCoverPart.Body.Edge133]
  Reference2 = -> Assembly [S0004mPart.Body.Edge42,S0004mPart.Body.Edge42]
FEATURE [Assembly::JointGroup] Joints
  Group = -> [GroundedJoint,Joint,Joint001,Joint002,Joint003,Joint004,Joint005,Joint007,Joint008,Joint009,Joint010,Joint011,Joint012,Joint013,Joint014,Joint015,Joint016,Joint017,Joint018]
FEATURE [Assembly::AssemblyObject] Assembly  label="FrontAssembly"
  Group = -> [Joints,FrontCoverPart,GroundedJoint,WheelLinkageTopLeftBody,Joint,WheelLinkageBottomLeftPart,Joint001,WheelLinkageTopRightPart,Joint002,WheelLinkageBottomRightPart,Joint003,FrontWheelAxleLeftPart,Joint004,FrontWheelAxleRightPart,Joint005,S0004mPart,TBoneLinkageTopPart,TBoneLinkageBottomPart,Joint007,Joint008,TransferLinkageLeftPart,TransferLinkageRightPart,Joint009,Joint010,Joint011,Joint012,+11 more]
  Origin = -> Origin
  Type = Assembly
